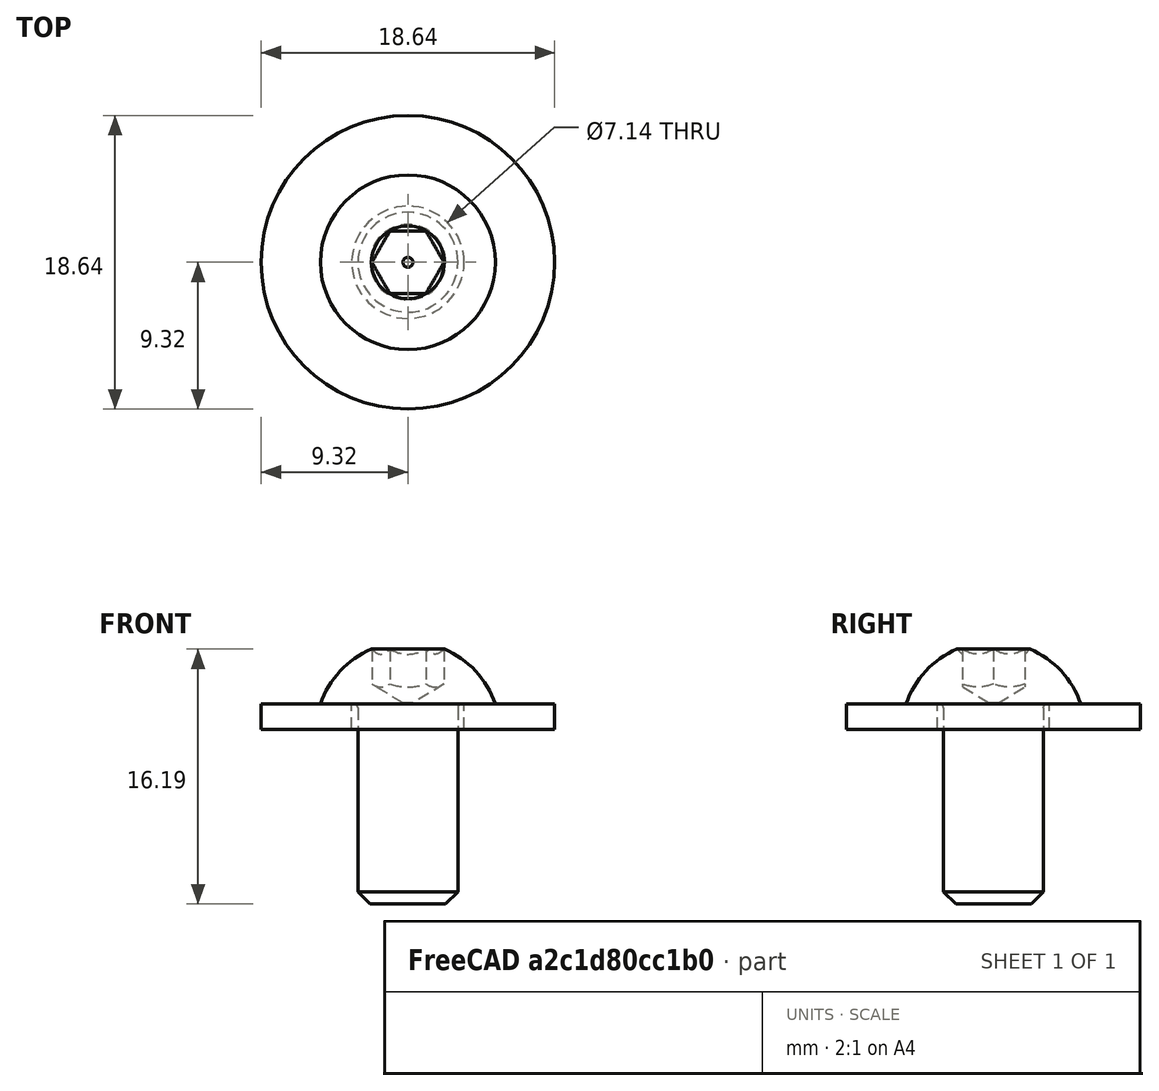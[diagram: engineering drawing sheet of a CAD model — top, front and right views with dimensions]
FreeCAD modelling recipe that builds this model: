
FCSTD DOCUMENT  (FreeCAD 2021.717R24301 +3842 (Git))
Label: X-axis
License: Creative Commons Attribution
LicenseURL: http://creativecommons.org/licenses/by/4.0/
objects: App::FeaturePython×78, Part::FeaturePython×72, App::Link×20, App::LinkElement×4, App::DocumentObjectGroup×1
note: 69 computed .brp shape members not serialized (recipe doc carries the construction recipe); baked Part::Feature solids carry a one-line shape summary decoded from their .brp
EXTERNAL_REF file=parts/HGR20.FCStd obj=Assembly001
EXTERNAL_REF file=parts/X axis plates.FCStd obj=Assembly001
EXTERNAL_REF file=parts/X axis plates.FCStd obj=Assembly
EXTERNAL_REF file=parts/Ballscrew.FCStd obj=Assembly003
EXTERNAL_REF file=parts/NEMA23-76.FCStd obj=Assembly001
EXTERNAL_REF file=parts/NEMA23-76.FCStd obj=Assembly
EXTERNAL_REF file=parts/X axis plates.FCStd obj=Assembly003
EXTERNAL_REF file=parts/HGH20CA.FCStd obj=Assembly
EXTERNAL_REF file=parts/HGH20CA.FCStd obj=Assembly001
EXTERNAL_REF file=parts/BallNut.FCStd obj=Assembly
EXTERNAL_REF file=parts/X axis plates.FCStd obj=Assembly005
EXTERNAL_REF file=parts/Extrusion.FCStd obj=Body001
EXTERNAL_REF file=parts/LimitSensor.FCStd obj=Assembly

FEATURE [App::Link] Link  label="HGR20-600"
  AutoLinkLabel = true
  AutoPlacement = true
  LinkPlacement = pos=(-97.7,1.41e-14,25.4) rot=(0,0,1;0rad)
  LinkedObject = -> <external parts/HGR20.FCStd>#Assembly001
  Placement = pos=(-97.7,1.41e-14,25.4) rot=(0,0,1;0rad)
  SyncGroupVisibility = false
  _LinkVersion = 1
FEATURE [App::Link] Link002  label="Top beam"
  AutoLinkLabel = true
  AutoPlacement = true
  LinkedObject = -> Assembly
  SyncGroupVisibility = false
  _LinkVersion = 1
FEATURE [App::Link] Link003  label="Bottom beam"
  AutoLinkLabel = true
  AutoPlacement = true
  LinkPlacement = pos=(-55.7,-2.274e-13,1.776e-13) rot=(0,0,-1;3.14159rad)
  LinkedObject = -> Assembly
  Placement = pos=(-55.7,-2.274e-13,1.776e-13) rot=(0,0,-1;3.14159rad)
  SyncGroupVisibility = false
  _LinkVersion = 1
FEATURE [App::Link] Link004  label="Left plate"
  AutoLinkLabel = true
  AutoPlacement = true
  LinkPlacement = pos=(166.3,-323.85,58.6) rot=(0,1,0;4.71239rad)
  LinkedObject = -> <external parts/X axis plates.FCStd>#Assembly001
  Placement = pos=(166.3,-323.85,58.6) rot=(0,1,0;4.71239rad)
  SyncGroupVisibility = false
  _LinkVersion = 1
FEATURE [App::Link] Link005  label="Right plate"
  AutoLinkLabel = true
  AutoPlacement = true
  LinkPlacement = pos=(166.3,69.85,58.6) rot=(0,1,0;4.71239rad)
  LinkedObject = -> <external parts/X axis plates.FCStd>#Assembly
  Placement = pos=(166.3,69.85,58.6) rot=(0,1,0;4.71239rad)
  SyncGroupVisibility = false
  _LinkVersion = 1
FEATURE [App::Link] Link006  label="Ballscrew-600"
  AutoLinkLabel = true
  AutoPlacement = true
  LinkPlacement = pos=(-27.85,251.9,-6.35) rot=(0,0,-1;3.14159rad)
  LinkedObject = -> <external parts/Ballscrew.FCStd>#Assembly003
  Placement = pos=(-27.85,251.9,-6.35) rot=(0,0,-1;3.14159rad)
  SyncGroupVisibility = false
  _LinkVersion = 1
FEATURE [App::Link] Link007  label="Coupling"
  AutoLinkLabel = true
  AutoPlacement = true
  LinkPlacement = pos=(-27.85,-296.25,18.65) rot=(-0.57735,-0.57735,-0.57735;2.0944rad)
  LinkedObject = -> <external parts/NEMA23-76.FCStd>#Assembly001
  Placement = pos=(-27.85,-296.25,18.65) rot=(-0.57735,-0.57735,-0.57735;2.0944rad)
  SyncGroupVisibility = false
  _LinkVersion = 1
FEATURE [App::Link] Link008  label="NEMA23-76"
  AutoLinkLabel = true
  AutoPlacement = true
  LinkPlacement = pos=(-27.85,-323.85,18.65) rot=(0.57735,-0.57735,0.57735;2.0944rad)
  LinkedObject = -> <external parts/NEMA23-76.FCStd>#Assembly
  Placement = pos=(-27.85,-323.85,18.65) rot=(0.57735,-0.57735,0.57735;2.0944rad)
  SyncGroupVisibility = false
  _LinkVersion = 1
FEATURE [App::Link] Link009  label="Rear plate"
  AutoLinkLabel = true
  AutoPlacement = true
  LinkPlacement = pos=(209.15,-76,-12.7) rot=(0,1,0;4.71239rad)
  LinkedObject = -> <external parts/X axis plates.FCStd>#Assembly003
  Placement = pos=(209.15,-76,-12.7) rot=(0,1,0;4.71239rad)
  SyncGroupVisibility = false
  _LinkVersion = 1
FEATURE [App::Link] Link012  label="HGH20CA-L-L"
  AutoLinkLabel = true
  AutoPlacement = true
  LinkPlacement = pos=(166.3,-274.8,202.6) rot=(-1,0,0;4.71239rad)
  LinkedObject = -> <external parts/HGH20CA.FCStd>#Assembly
  Placement = pos=(166.3,-274.8,202.6) rot=(-1,0,0;4.71239rad)
  SyncGroupVisibility = false
  _LinkVersion = 1
FEATURE [App::Link] Link013  label="HGH20CA-L-R"
  AutoLinkLabel = true
  AutoPlacement = true
  LinkPlacement = pos=(166.3,-274.8,58.6) rot=(-1,0,0;4.71239rad)
  LinkedObject = -> <external parts/HGH20CA.FCStd>#Assembly001
  Placement = pos=(166.3,-274.8,58.6) rot=(-1,0,0;4.71239rad)
  SyncGroupVisibility = false
  _LinkVersion = 1
FEATURE [App::Link] Link014  label="HGH20CA-R-L"
  AutoLinkLabel = true
  AutoPlacement = true
  LinkPlacement = pos=(166.3,274.8,58.6) rot=(1,0,0;4.71239rad)
  LinkedObject = -> Link012
  Placement = pos=(166.3,274.8,58.6) rot=(1,0,0;4.71239rad)
  SyncGroupVisibility = false
  _LinkVersion = 1
FEATURE [App::Link] Link015  label="HGH20CA-R-R"
  AutoLinkLabel = true
  AutoPlacement = true
  LinkPlacement = pos=(166.3,274.8,202.6) rot=(1,0,0;4.71239rad)
  LinkedObject = -> Link013
  Placement = pos=(166.3,274.8,202.6) rot=(1,0,0;4.71239rad)
  SyncGroupVisibility = false
  _LinkVersion = 1
FEATURE [App::Link] Link020  label="Left nut"
  AutoLinkLabel = true
  AutoPlacement = true
  LinkPlacement = pos=(219.3,-305.675,131.475) rot=(0,0.707107,0.707107;3.14159rad)
  LinkedObject = -> <external parts/BallNut.FCStd>#Assembly
  Placement = pos=(219.3,-305.675,131.475) rot=(0,0.707107,0.707107;3.14159rad)
  SyncGroupVisibility = false
  _LinkVersion = 1
FEATURE [App::Link] Link021  label="Right nut"
  AutoLinkLabel = true
  AutoPlacement = true
  LinkPlacement = pos=(219.3,305.675,131.475) rot=(1,0,0;1.5708rad)
  LinkedObject = -> <external parts/BallNut.FCStd>#Assembly
  Placement = pos=(219.3,305.675,131.475) rot=(1,0,0;1.5708rad)
  SyncGroupVisibility = false
  _LinkVersion = 1
FEATURE [App::Link] Link022  label="Gouverner left"
  AutoLinkLabel = true
  AutoPlacement = true
  LinkPlacement = pos=(166.3,-323.85,130.6) rot=(0,1,0;4.71239rad)
  LinkedObject = -> <external parts/X axis plates.FCStd>#Assembly005
  Placement = pos=(166.3,-323.85,130.6) rot=(0,1,0;4.71239rad)
  SyncGroupVisibility = false
  _LinkVersion = 1
FEATURE [App::Link] Link023  label="Gouverner right"
  AutoLinkLabel = true
  AutoPlacement = true
  LinkPlacement = pos=(166.3,323.85,130.6) rot=(0.707107,0,-0.707107;3.14159rad)
  LinkedObject = -> <external parts/X axis plates.FCStd>#Assembly005
  Placement = pos=(166.3,323.85,130.6) rot=(0.707107,0,-0.707107;3.14159rad)
  SyncGroupVisibility = false
  _LinkVersion = 1
FEATURE [App::Link] Link024  label="Extrusion"
  AutoLinkLabel = true
  AutoPlacement = true
  LinkPlacement = pos=(-85,0,0) rot=(0,0,1;0rad)
  LinkedObject = -> <external parts/Extrusion.FCStd>#Body001
  Placement = pos=(-85,0,0) rot=(0,0,1;0rad)
  SyncGroupVisibility = false
  _LinkVersion = 1
FEATURE [Part::FeaturePython] Washer  label="1/4in-Washer"  # Fasteners workbench fastener (typed FeaturePython)
  Placement = pos=(0,0,-1.6002) rot=(0,0,1;0rad)
  diameter = 11
  invert = false
  matchOuter = false
  offset = 0
  type = 1
FEATURE [Part::FeaturePython] Screw  label="1/4inx1/2in-Screw"  # Fasteners workbench fastener (typed FeaturePython)
  diameter = 11
  invert = false
  length = 4
  lengthCustom = 12.7
  matchOuter = false
  offset = 0
  thread = false
  type = 4
FEATURE [Part::FeaturePython] Parts002  # WARN: FeaturePython — macro-defined, semantics opaque (R4)
  Group = -> [Washer,Screw]
  GroupMode = 0
  _LinkVersion = 1
FEATURE [App::LinkElement] Link025_i0
  LinkPlacement = pos=(-63.4102,-234.8,-12.7) rot=(-0.57735,-0.57735,0.57735;2.0944rad)
  LinkedObject = -> Assembly002
  Placement = pos=(-63.4102,-234.8,-12.7) rot=(-0.57735,-0.57735,0.57735;2.0944rad)
  _LinkVersion = 1
FEATURE [App::LinkElement] Link025_i1
  LinkPlacement = pos=(-63.4102,-78.2667,-12.7) rot=(-0.57735,-0.57735,0.57735;2.0944rad)
  LinkedObject = -> Assembly002
  Placement = pos=(-63.4102,-78.2667,-12.7) rot=(-0.57735,-0.57735,0.57735;2.0944rad)
  _LinkVersion = 1
FEATURE [App::LinkElement] Link025_i2
  LinkPlacement = pos=(-63.4102,78.2667,-12.7) rot=(-0.57735,-0.57735,0.57735;2.0944rad)
  LinkedObject = -> Assembly002
  Placement = pos=(-63.4102,78.2667,-12.7) rot=(-0.57735,-0.57735,0.57735;2.0944rad)
  _LinkVersion = 1
FEATURE [App::LinkElement] Link025_i3
  LinkPlacement = pos=(-63.4102,234.8,-12.7) rot=(-0.57735,-0.57735,0.57735;2.0944rad)
  LinkedObject = -> Assembly002
  Placement = pos=(-63.4102,234.8,-12.7) rot=(-0.57735,-0.57735,0.57735;2.0944rad)
  _LinkVersion = 1
FEATURE [App::Link] Link025  label="1/4x1/2 screw and washer Assembly 4ct"
  AutoLinkLabel = true
  AutoPlacement = true
  ElementCount = 4
  ElementList = -> [Link025_i0,Link025_i1,Link025_i2,Link025_i3]
  LinkedObject = -> Assembly002
  SyncGroupVisibility = false
  _LinkVersion = 1
FEATURE [Part::FeaturePython] Parts  # WARN: FeaturePython — macro-defined, semantics opaque (R4)
  Group = -> [Link,Link024,Link025]
  GroupMode = 0
  _LinkVersion = 1
FEATURE [App::Link] Link026  label="Limit sensor"
  AutoLinkLabel = true
  AutoPlacement = true
  LinkPlacement = pos=(-62.4,-304.8,56.1) rot=(-1,0,0;3.14159rad)
  LinkedObject = -> <external parts/LimitSensor.FCStd>#Assembly
  Placement = pos=(-62.4,-304.8,56.1) rot=(-1,0,0;3.14159rad)
  SyncGroupVisibility = false
  _LinkVersion = 1
FEATURE [Part::FeaturePython] Parts001  # WARN: FeaturePython — macro-defined, semantics opaque (R4)
  Group = -> [Link002,Link003,Link004,Link005,Link006,Link007,Link008,Link009,Link012,Link013,Link014,Link015,Link020,Link021,Link022,Link023,Link026]
  GroupMode = 0
  _LinkVersion = 1
FEATURE [Part::FeaturePython] Assembly  label="X-beam Assembly"  # WARN: FeaturePython — macro-defined, semantics opaque (R4)
  AutoRelax = true
  BuildShape = 0
  Freeze = false
  Group = -> [Constraints,Elements,Parts]
  Verbose = false
  _LinkVersion = 1
  _SolverType = 1
  _Version = 1
FEATURE [App::FeaturePython] Constraints  # WARN: FeaturePython — macro-defined, semantics opaque (R4)
  Group = -> [Constraint,Constraint001,Constraint032,Constraint033,Constraint034,Constraint035]
  _LinkVersion = 1
  _Version = 1
FEATURE [App::FeaturePython] Elements  # WARN: FeaturePython — macro-defined, semantics opaque (R4)
  Group = -> [Element,Element001,Element002,Element003,Element007,Element008,Element012,Element013,_Element002,_Element003,_Element004,_Element005,_Element006,_Element007,_Element008,_Element009]
  _LinkVersion = 1
FEATURE [Part::FeaturePython] Element  label="center-mate@HGR20-600-Assembly"  # link proxy (typed FeaturePython)
  Detach = false
  LinkTransform = true
  LinkedObject = -> Link [1.$center-mate.]
  _LinkVersion = 1
  _Parent = -> Elements
FEATURE [Part::FeaturePython] Element001  label="extrusion center"  # link proxy (typed FeaturePython)
  Detach = false
  LinkTransform = true
  LinkedObject = -> Link024 [Sketch001.]
  _LinkVersion = 1
  _Parent = -> Elements
FEATURE [App::FeaturePython] Constraint  label="Locked"  # WARN: FeaturePython — macro-defined, semantics opaque (R4)
  Disabled = false
  Group = -> [ElementLink]
  _ConstraintType = 0
  _LinkVersion = 1
  _Parent = -> Constraints
FEATURE [App::FeaturePython] ElementLink  label="extrusion center"  # link proxy (typed FeaturePython)
  LinkTransform = true
  LinkedObject = -> Element001
  _LinkVersion = 1
  _Parent = -> Constraint
FEATURE [App::FeaturePython] Constraint001  label="Attachment"  # WARN: FeaturePython — macro-defined, semantics opaque (R4)
  Cascade = false
  Disabled = false
  Group = -> [ElementLink001,ElementLink002]
  Multiply = false
  _ConstraintType = 45
  _LinkVersion = 1
  _Parent = -> Constraints
FEATURE [App::FeaturePython] ElementLink001  label="extrusion center"  # link proxy (typed FeaturePython)
  LinkTransform = true
  LinkedObject = -> Element001
  _LinkVersion = 1
  _Parent = -> Constraint001
FEATURE [App::FeaturePython] ElementLink002  label="center-mate@HGR20-600-Assembly"  # link proxy (typed FeaturePython)
  LinkTransform = true
  LinkedObject = -> Element
  Offset = pos=(0,0,0) rot=(1,0,0;3.14159rad)
  Placement = pos=(1.42e-14,3.13e-14,50.8) rot=(1,0,0;3.14159rad)
  _LinkVersion = 1
  _Parent = -> Constraint001
FEATURE [Part::FeaturePython] Element002  label="top-cart-mate"  # link proxy (typed FeaturePython)
  Detach = false
  LinkTransform = true
  LinkedObject = -> Link [1.$top-mate.]
  _LinkVersion = 1
  _Parent = -> Elements
FEATURE [Part::FeaturePython] Element003  label="side-cart-mate"  # link proxy (typed FeaturePython)
  Detach = false
  LinkTransform = true
  LinkedObject = -> Link [1.$side-mate.]
  _LinkVersion = 1
  _Parent = -> Elements
FEATURE [Part::FeaturePython] Assembly001  label="X-axis Assembly"  # WARN: FeaturePython — macro-defined, semantics opaque (R4)
  AutoRelax = true
  BuildShape = 0
  Freeze = false
  Group = -> [Constraints001,Elements001,Parts001]
  Placement = pos=(79.15,3.69183,42.8418) rot=(-0.57735,-0.57735,0.57735;4.18879rad)
  Verbose = false
  _LinkVersion = 1
  _SolverType = 1
  _Version = 1
FEATURE [App::FeaturePython] Constraints001  # WARN: FeaturePython — macro-defined, semantics opaque (R4)
  Group = -> [Constraint002,Constraint003,Constraint004,Constraint005,Constraint011,Constraint012,Constraint013,Constraint021,Constraint022,Constraint023,Constraint024,Constraint025,Constraint026,Constraint027,Constraint028,Constraint029,Constraint036]
  _LinkVersion = 1
  _Version = 1
FEATURE [App::FeaturePython] Elements001  # WARN: FeaturePython — macro-defined, semantics opaque (R4)
  Group = -> [Element004,Element005,Element006,Element009,Element010,Element011,Element014,Element015,Element016,Element017,Element018,Element019,Element020,Element021,Element022,Element023,Element024,Element025,Element026,Element027,Element028,Element030,Element031,Element034,Element036,Element038,Element040,Element046,Element047,Element048,Element049,Element054,Element055,Element056,Element057,Element058,+9 more]
  _LinkVersion = 1
FEATURE [Part::FeaturePython] Element004  label="top-cart-mate@X-beam Assembly"  # link proxy (typed FeaturePython)
  Detach = false
  LinkTransform = true
  LinkedObject = -> Link002 [1.$top-cart-mate.]
  _LinkVersion = 1
  _Parent = -> Elements001
FEATURE [Part::FeaturePython] Element005  label="side-cart-mate@X-beam Assembly"  # link proxy (typed FeaturePython)
  Detach = false
  LinkTransform = true
  LinkedObject = -> Link002 [1.$side-cart-mate.]
  _LinkVersion = 1
  _Parent = -> Elements001
FEATURE [Part::FeaturePython] Element006  label="extrusion center@X-beam Assembly"  # link proxy (typed FeaturePython)
  Detach = false
  LinkTransform = true
  LinkedObject = -> Link002 [1.$extrusion center.]
  _LinkVersion = 1
  _Parent = -> Elements001
FEATURE [App::FeaturePython] Constraint002  label="Locked001"  # WARN: FeaturePython — macro-defined, semantics opaque (R4)
  Disabled = false
  Group = -> [ElementLink003]
  _ConstraintType = 0
  _LinkVersion = 1
  _Parent = -> Constraints001
FEATURE [App::FeaturePython] ElementLink003  label="extrusion center@X-beam Assembly"  # link proxy (typed FeaturePython)
  LinkTransform = true
  LinkedObject = -> Element006
  _LinkVersion = 1
  _Parent = -> Constraint002
FEATURE [Part::FeaturePython] Element007  label="left-point@HGR20-600-Assembly"  # link proxy (typed FeaturePython)
  Detach = false
  LinkTransform = true
  LinkedObject = -> Link [1.$left-point.]
  _LinkVersion = 1
  _Parent = -> Elements
FEATURE [Part::FeaturePython] Element008  label="right-point@HGR20-600-Assembly"  # link proxy (typed FeaturePython)
  Detach = false
  LinkTransform = true
  LinkedObject = -> Link [1.$right-point.]
  _LinkVersion = 1
  _Parent = -> Elements
FEATURE [Part::FeaturePython] Element009  label="left-point@X-beam Assembly"  # link proxy (typed FeaturePython)
  Detach = false
  LinkTransform = true
  LinkedObject = -> Link002 [1.$left-point@HGR20-600-Assembly.]
  _LinkVersion = 1
  _Parent = -> Elements001
FEATURE [Part::FeaturePython] Element010  label="right-point@X-beam Assembly"  # link proxy (typed FeaturePython)
  Detach = false
  LinkTransform = true
  LinkedObject = -> Link003 [1.$right-point@HGR20-600-Assembly.]
  _LinkVersion = 1
  _Parent = -> Elements001
FEATURE [Part::FeaturePython] Element011  label="side-cart-mate@X-beam Assembly001"  # link proxy (typed FeaturePython)
  Detach = false
  LinkTransform = true
  LinkedObject = -> Link003 [1.$side-cart-mate.]
  _LinkVersion = 1
  _Parent = -> Elements001
FEATURE [Part::FeaturePython] Element012  label="plate-mate-1"  # link proxy (typed FeaturePython)
  Detach = false
  LinkTransform = true
  LinkedObject = -> Link024 [Pocket004.Edge345]
  _LinkVersion = 1
  _Parent = -> Elements
FEATURE [Part::FeaturePython] Element013  label="plate-mate-2"  # link proxy (typed FeaturePython)
  Detach = false
  LinkTransform = true
  LinkedObject = -> Link024 [Pocket004.Edge176]
  _LinkVersion = 1
  _Parent = -> Elements
FEATURE [Part::FeaturePython] Element014  label="plate-mate-tl@X-beam Assembly"  # link proxy (typed FeaturePython)
  Detach = false
  LinkTransform = true
  LinkedObject = -> Link002 [1.$plate-mate-1.]
  _LinkVersion = 1
  _Parent = -> Elements001
FEATURE [Part::FeaturePython] Element015  label="plate-mate-tr@X-beam Assembly"  # link proxy (typed FeaturePython)
  Detach = false
  LinkTransform = true
  LinkedObject = -> Link002 [1.$plate-mate-2.]
  _LinkVersion = 1
  _Parent = -> Elements001
FEATURE [Part::FeaturePython] Element016  label="plate-mate-br@X-beam Assembly"  # link proxy (typed FeaturePython)
  Detach = false
  LinkTransform = true
  LinkedObject = -> Link003 [1.$plate-mate-1.]
  _LinkVersion = 1
  _Parent = -> Elements001
FEATURE [Part::FeaturePython] Element017  label="plate-mate-bl@X-beam Assembly"  # link proxy (typed FeaturePython)
  Detach = false
  LinkTransform = true
  LinkedObject = -> Link003 [1.$plate-mate-2.]
  _LinkVersion = 1
  _Parent = -> Elements001
FEATURE [Part::FeaturePython] Element018  label="bottom-beam-mate@Left plate Assembly"  # link proxy (typed FeaturePython)
  Detach = false
  LinkTransform = true
  LinkedObject = -> Link004 [1.$bottom-beam-mate.]
  _LinkVersion = 1
  _Parent = -> Elements001
FEATURE [Part::FeaturePython] Element019  label="top-beam-mate@Left plate Assembly"  # link proxy (typed FeaturePython)
  Detach = false
  LinkTransform = true
  LinkedObject = -> Link004 [1.$top-beam-mate.]
  _LinkVersion = 1
  _Parent = -> Elements001
FEATURE [Part::FeaturePython] Element020  label="top-beam-mate@Right plate Assembly"  # link proxy (typed FeaturePython)
  Detach = false
  LinkTransform = true
  LinkedObject = -> Link005 [1.$top-beam-mate.]
  _LinkVersion = 1
  _Parent = -> Elements001
FEATURE [App::FeaturePython] Constraint003  label="Attachment-beam-tr"  # WARN: FeaturePython — macro-defined, semantics opaque (R4)
  Cascade = false
  Disabled = false
  Group = -> [ElementLink004,ElementLink005]
  Multiply = false
  _ConstraintType = 45
  _LinkVersion = 1
  _Parent = -> Constraints001
FEATURE [App::FeaturePython] ElementLink004  label="_top-beam-mate@Right plate Assembly"  # link proxy (typed FeaturePython)
  LinkTransform = true
  LinkedObject = -> _Element010
  _LinkVersion = 1
  _Parent = -> Constraint003
FEATURE [App::FeaturePython] ElementLink005  label="plate-mate-tr@X-beam Assembly"  # link proxy (typed FeaturePython)
  LinkTransform = true
  LinkedObject = -> Element015
  Offset = pos=(0,0,0) rot=(0,0,1;1.5708rad)
  Placement = pos=(-110.4,0,85) rot=(0,-1,0;1.5708rad)
  _LinkVersion = 1
  _Parent = -> Constraint003
FEATURE [App::FeaturePython] Constraint004  label="Attachment-beam-tl"  # WARN: FeaturePython — macro-defined, semantics opaque (R4)
  Cascade = false
  Disabled = false
  Group = -> [ElementLink006,ElementLink007]
  Multiply = false
  _ConstraintType = 45
  _LinkVersion = 1
  _Parent = -> Constraints001
FEATURE [App::FeaturePython] ElementLink006  label="top-beam-mate@Left plate Assembly"  # link proxy (typed FeaturePython)
  LinkTransform = true
  LinkedObject = -> Element019
  _LinkVersion = 1
  _Parent = -> Constraint004
FEATURE [App::FeaturePython] ElementLink007  label="plate-mate-tl@X-beam Assembly"  # link proxy (typed FeaturePython)
  LinkTransform = true
  LinkedObject = -> Element014
  Offset = pos=(0,0,0) rot=(0,0,1;1.5708rad)
  Placement = pos=(-110.4,0,85) rot=(0,-1,0;1.5708rad)
  _LinkVersion = 1
  _Parent = -> Constraint004
FEATURE [App::FeaturePython] Constraint005  label="Attachment-beam-bl"  # WARN: FeaturePython — macro-defined, semantics opaque (R4)
  Cascade = false
  Disabled = false
  Group = -> [ElementLink008,ElementLink009]
  Multiply = false
  _ConstraintType = 45
  _LinkVersion = 1
  _Parent = -> Constraints001
FEATURE [App::FeaturePython] ElementLink008  label="bottom-beam-mate@Left plate Assembly"  # link proxy (typed FeaturePython)
  LinkTransform = true
  LinkedObject = -> Element018
  Offset = pos=(0,0,0) rot=(0,0,1;1.5708rad)
  Placement = pos=(29.3,0,-54.7) rot=(0,-1,0;1.5708rad)
  _LinkVersion = 1
  _Parent = -> Constraint005
FEATURE [App::FeaturePython] ElementLink009  label="plate-mate-bl@X-beam Assembly"  # link proxy (typed FeaturePython)
  LinkTransform = true
  LinkedObject = -> Element017
  Offset = pos=(0,0,0) rot=(1,0,0;3.14159rad)
  Placement = pos=(-8.53e-14,-609.6,-25.4) rot=(1,0,0;3.14159rad)
  _LinkVersion = 1
  _Parent = -> Constraint005
FEATURE [Part::FeaturePython] Element021  label="screw-mate@Coupling-Assembly"  # link proxy (typed FeaturePython)
  Detach = false
  LinkTransform = true
  LinkedObject = -> Link007 [1.$screw-mate.]
  _LinkVersion = 1
  _Parent = -> Elements001
FEATURE [Part::FeaturePython] Element022  label="coupling-mate@Ballscrew-600-Assembly"  # link proxy (typed FeaturePython)
  Detach = false
  LinkTransform = true
  LinkedObject = -> Link006 [1.$coupling-mate.]
  _LinkVersion = 1
  _Parent = -> Elements001
FEATURE [Part::FeaturePython] Element023  label="motor-mate@Coupling-Assembly"  # link proxy (typed FeaturePython)
  Detach = false
  LinkTransform = true
  LinkedObject = -> Link007 [1.$motor-mate.]
  _LinkVersion = 1
  _Parent = -> Elements001
FEATURE [Part::FeaturePython] Element024  label="coupling-mate@NEMA23-76-Assembly"  # link proxy (typed FeaturePython)
  Detach = false
  LinkTransform = true
  LinkedObject = -> Link008 [1.$coupling-mate.]
  _LinkVersion = 1
  _Parent = -> Elements001
FEATURE [Part::FeaturePython] Element025  label="plate-mate@NEMA23-76-Assembly"  # link proxy (typed FeaturePython)
  Detach = false
  LinkTransform = true
  LinkedObject = -> Link008 [1.$bracket-mate.]
  _LinkVersion = 1
  _Parent = -> Elements001
FEATURE [Part::FeaturePython] Element026  label="motor-mate@Left plate Assembly"  # link proxy (typed FeaturePython)
  Detach = false
  LinkTransform = true
  LinkedObject = -> Link004 [1.$motor-mate.]
  _LinkVersion = 1
  _Parent = -> Elements001
FEATURE [Part::FeaturePython] Element027  label="bf-base@Ballscrew-600-Assembly"  # link proxy (typed FeaturePython)
  Detach = false
  LinkTransform = true
  LinkedObject = -> Link006 [1.$bf-base.]
  _LinkVersion = 1
  _Parent = -> Elements001
FEATURE [App::FeaturePython] Constraint011  label="Attachment-motor-coupling"  # WARN: FeaturePython — macro-defined, semantics opaque (R4)
  Cascade = false
  Disabled = false
  Group = -> [ElementLink019,ElementLink020]
  Multiply = false
  _ConstraintType = 45
  _LinkVersion = 1
  _Parent = -> Constraints001
FEATURE [App::FeaturePython] ElementLink019  label="coupling-mate@NEMA23-76-Assembly"  # link proxy (typed FeaturePython)
  LinkTransform = true
  LinkedObject = -> Element024
  _LinkVersion = 1
  _Parent = -> Constraint011
FEATURE [App::FeaturePython] ElementLink020  label="motor-mate@Coupling-Assembly"  # link proxy (typed FeaturePython)
  LinkTransform = true
  LinkedObject = -> Element023
  _LinkVersion = 1
  _Parent = -> Constraint011
FEATURE [App::FeaturePython] Constraint012  label="Attachment-screw-coupling"  # WARN: FeaturePython — macro-defined, semantics opaque (R4)
  Cascade = false
  Disabled = false
  Group = -> [ElementLink021,ElementLink022]
  Multiply = false
  _ConstraintType = 45
  _LinkVersion = 1
  _Parent = -> Constraints001
FEATURE [App::FeaturePython] ElementLink021  label="coupling-mate@Ballscrew-600-Assembly"  # link proxy (typed FeaturePython)
  LinkTransform = true
  LinkedObject = -> Element022
  Offset = pos=(0,0,0) rot=(1,0,0;3.14159rad)
  Placement = pos=(1.51559e-11,-582.5,37.3) rot=(1,0,0;3.14159rad)
  _LinkVersion = 1
  _Parent = -> Constraint012
FEATURE [App::FeaturePython] ElementLink022  label="screw-mate@Coupling-Assembly"  # link proxy (typed FeaturePython)
  LinkTransform = true
  LinkedObject = -> Element021
  Offset = pos=(0,0,0) rot=(0,0,1;4.71239rad)
  Placement = pos=(-9.2,1.53936e-08,46.5) rot=(0,-1,0;1.5708rad)
  _LinkVersion = 1
  _Parent = -> Constraint012
FEATURE [Part::FeaturePython] Element028  label="side-mate@Rear plate left Assembly"  # link proxy (typed FeaturePython)
  Detach = false
  LinkTransform = true
  LinkedObject = -> Link009 [1.$side-mate-L.]
  _LinkVersion = 1
  _Parent = -> Elements001
FEATURE [Part::FeaturePython] Element030  label="rear-mate@Left plate Assembly"  # link proxy (typed FeaturePython)
  Detach = false
  LinkTransform = true
  LinkedObject = -> Link004 [1.$rear-mate.]
  _LinkVersion = 1
  _Parent = -> Elements001
FEATURE [Part::FeaturePython] Element031  label="rear-mate@Right plate Assembly"  # link proxy (typed FeaturePython)
  Detach = false
  LinkTransform = true
  LinkedObject = -> Link005 [1.$rear-mate.]
  _LinkVersion = 1
  _Parent = -> Elements001
FEATURE [App::FeaturePython] Constraint013  label="Attachment-left-rear"  # WARN: FeaturePython — macro-defined, semantics opaque (R4)
  Cascade = false
  Disabled = false
  Group = -> [ElementLink023,ElementLink024]
  Multiply = false
  _ConstraintType = 45
  _LinkVersion = 1
  _Parent = -> Constraints001
FEATURE [App::FeaturePython] ElementLink023  label="rear-mate@Left plate Assembly"  # link proxy (typed FeaturePython)
  LinkTransform = true
  LinkedObject = -> Element030
  Offset = pos=(0,0,0) rot=(1,0,0;3.14159rad)
  Placement = pos=(-55.7,-609.6,-1.634e-13) rot=(0,0,1;3.14159rad)
  _LinkVersion = 1
  _Parent = -> Constraint013
FEATURE [App::FeaturePython] ElementLink024  label="side-mate@Rear plate left Assembly"  # link proxy (typed FeaturePython)
  LinkTransform = true
  LinkedObject = -> Element028
  Offset = pos=(0,0,0) rot=(0,0,1;1.5708rad)
  Placement = pos=(-40.55,5.68e-14,15.15) rot=(0,-1,0;1.5708rad)
  _LinkVersion = 1
  _Parent = -> Constraint013
FEATURE [Part::FeaturePython] Element034  label="shim-L-L@HGH20CA-L-Assembly"  # link proxy (typed FeaturePython)
  Detach = false
  LinkTransform = true
  LinkedObject = -> Link012 [1.$shim-tr.]
  _LinkVersion = 1
  _Parent = -> Elements001
FEATURE [Part::FeaturePython] Element036  label="shim-L-R@HGH20CA-R-Assembly"  # link proxy (typed FeaturePython)
  Detach = false
  LinkTransform = true
  LinkedObject = -> Link013 [1.$shim-br.]
  _LinkVersion = 1
  _Parent = -> Elements001
FEATURE [Part::FeaturePython] Element038  label="shim-R-L@HGH20CA-L-Assembly"  # link proxy (typed FeaturePython)
  Detach = false
  LinkTransform = true
  LinkedObject = -> Link014 [1.$shim-tr.]
  _LinkVersion = 1
  _Parent = -> Elements001
FEATURE [Part::FeaturePython] Element040  label="shim-R-R@HGH20CA-R-Assembly"  # link proxy (typed FeaturePython)
  Detach = false
  LinkTransform = true
  LinkedObject = -> Link015 [1.$shim-br.]
  _LinkVersion = 1
  _Parent = -> Elements001
FEATURE [Part::FeaturePython] Element046  label="shim-R-L@Right plate Assembly"  # link proxy (typed FeaturePython)
  Detach = false
  LinkTransform = true
  LinkedObject = -> Link005 [1.$cart-L.]
  _LinkVersion = 1
  _Parent = -> Elements001
FEATURE [Part::FeaturePython] Element047  label="shim-R-R@Right plate Assembly"  # link proxy (typed FeaturePython)
  Detach = false
  LinkTransform = true
  LinkedObject = -> Link005 [1.$cart-R.]
  _LinkVersion = 1
  _Parent = -> Elements001
FEATURE [Part::FeaturePython] Element048  label="shim-L-L@Left plate Assembly"  # link proxy (typed FeaturePython)
  Detach = false
  LinkTransform = true
  LinkedObject = -> Link004 [1.$cart-L.]
  _LinkVersion = 1
  _Parent = -> Elements001
FEATURE [Part::FeaturePython] Element049  label="shim-L-R@Left plate Assembly"  # link proxy (typed FeaturePython)
  Detach = false
  LinkTransform = true
  LinkedObject = -> Link004 [1.$cart-R.]
  _LinkVersion = 1
  _Parent = -> Elements001
FEATURE [App::FeaturePython] Constraint021  label="Attachment-cart-R-R"  # WARN: FeaturePython — macro-defined, semantics opaque (R4)
  Cascade = false
  Disabled = false
  Group = -> [ElementLink039,ElementLink040]
  Multiply = false
  _ConstraintType = 45
  _LinkVersion = 1
  _Parent = -> Constraints001
FEATURE [App::FeaturePython] ElementLink039  label="shim-R-R@Right plate Assembly"  # link proxy (typed FeaturePython)
  LinkTransform = true
  LinkedObject = -> Element047
  Offset = pos=(0,0,0) rot=(1,0,0;3.14159rad)
  Placement = pos=(364.6,609.6,2.274e-13) rot=(0,0,1;3.14159rad)
  _LinkVersion = 1
  _Parent = -> Constraint021
FEATURE [App::FeaturePython] ElementLink040  label="shim-R-R@HGH20CA-R-Assembly"  # link proxy (typed FeaturePython)
  LinkTransform = true
  LinkedObject = -> Element040
  Offset = pos=(0,0,0) rot=(0,0,1;1.5708rad)
  Placement = pos=(-38.3,1.705e-13,402.9) rot=(0,1,0;1.5708rad)
  _LinkVersion = 1
  _Parent = -> Constraint021
FEATURE [App::FeaturePython] Constraint022  label="Attachment-cart-R-L"  # WARN: FeaturePython — macro-defined, semantics opaque (R4)
  Cascade = false
  Disabled = false
  Group = -> [ElementLink041,ElementLink042]
  Multiply = false
  _ConstraintType = 45
  _LinkVersion = 1
  _Parent = -> Constraints001
FEATURE [App::FeaturePython] ElementLink041  label="shim-R-L@Right plate Assembly"  # link proxy (typed FeaturePython)
  LinkTransform = true
  LinkedObject = -> Element046
  Offset = pos=(0,0,0) rot=(1,0,0;3.14159rad)
  Placement = pos=(364.6,609.6,2.274e-13) rot=(0,0,1;3.14159rad)
  _LinkVersion = 1
  _Parent = -> Constraint022
FEATURE [App::FeaturePython] ElementLink042  label="shim-R-L@HGH20CA-L-Assembly"  # link proxy (typed FeaturePython)
  LinkTransform = true
  LinkedObject = -> Element038
  Offset = pos=(0,0,0) rot=(0,0,1;1.5708rad)
  Placement = pos=(141.7,5.68e-14,222.9) rot=(0,1,0;1.5708rad)
  _LinkVersion = 1
  _Parent = -> Constraint022
FEATURE [App::FeaturePython] Constraint023  label="Attachment-cart-L-R"  # WARN: FeaturePython — macro-defined, semantics opaque (R4)
  Cascade = false
  Disabled = false
  Group = -> [ElementLink043,ElementLink044]
  Multiply = false
  _ConstraintType = 45
  _LinkVersion = 1
  _Parent = -> Constraints001
FEATURE [App::FeaturePython] ElementLink043  label="shim-L-R@Left plate Assembly"  # link proxy (typed FeaturePython)
  LinkTransform = true
  LinkedObject = -> Element049
  Placement = pos=(1.137e-13,0,-7.1e-15) rot=(0,0,1;0rad)
  _LinkVersion = 1
  _Parent = -> Constraint023
FEATURE [App::FeaturePython] ElementLink044  label="shim-L-R@HGH20CA-R-Assembly"  # link proxy (typed FeaturePython)
  LinkTransform = true
  LinkedObject = -> Element036
  Offset = pos=(0,0,0) rot=(0,0,1;4.71239rad)
  Placement = pos=(141.7,5.68e-14,222.9) rot=(0,1,0;1.5708rad)
  _LinkVersion = 1
  _Parent = -> Constraint023
FEATURE [App::FeaturePython] Constraint024  label="Attachment-cart-L-L"  # WARN: FeaturePython — macro-defined, semantics opaque (R4)
  Cascade = false
  Disabled = false
  Group = -> [ElementLink045,ElementLink046]
  Multiply = false
  _ConstraintType = 45
  _LinkVersion = 1
  _Parent = -> Constraints001
FEATURE [App::FeaturePython] ElementLink045  label="shim-L-L@HGH20CA-L-Assembly"  # link proxy (typed FeaturePython)
  LinkTransform = true
  LinkedObject = -> Element034
  Offset = pos=(0,0,0) rot=(0,0,1;3.14159rad)
  Placement = pos=(364.6,-4.547e-13,441.2) rot=(0,1,0;3.14159rad)
  _LinkVersion = 1
  _Parent = -> Constraint024
FEATURE [App::FeaturePython] ElementLink046  label="shim-L-L@Left plate Assembly"  # link proxy (typed FeaturePython)
  LinkTransform = true
  LinkedObject = -> Element048
  Offset = pos=(0,0,0) rot=(0,0,1;4.71239rad)
  Placement = pos=(-38.3,-5.68e-14,402.9) rot=(0,1,0;1.5708rad)
  _LinkVersion = 1
  _Parent = -> Constraint024
FEATURE [Part::FeaturePython] Element054  label="point@HGH20CA-R-Assembly"  # link proxy (typed FeaturePython)
  Detach = false
  LinkTransform = true
  LinkedObject = -> Link015 [1.$point.]
  _LinkVersion = 1
  _Parent = -> Elements001
FEATURE [Part::FeaturePython] Element055  label="side-mate@HGH20CA-R-Assembly"  # link proxy (typed FeaturePython)
  Detach = false
  LinkTransform = true
  LinkedObject = -> Link015 [1.$side-mate.]
  _LinkVersion = 1
  _Parent = -> Elements001
FEATURE [Part::FeaturePython] Element056  label="top-mate@HGH20CA-R-Assembly"  # link proxy (typed FeaturePython)
  Detach = false
  LinkTransform = true
  LinkedObject = -> Link015 [1.$top-mate.]
  _LinkVersion = 1
  _Parent = -> Elements001
FEATURE [Part::FeaturePython] Element057  label="plate-mate@Gouverner Assembly Left"  # link proxy (typed FeaturePython)
  Detach = false
  LinkTransform = true
  LinkedObject = -> Link022 [1.$plate-mate.]
  _LinkVersion = 1
  _Parent = -> Elements001
FEATURE [Part::FeaturePython] Element058  label="nut-mate@Gouverner Assembly Left"  # link proxy (typed FeaturePython)
  Detach = false
  LinkTransform = true
  LinkedObject = -> Link022 [1.$nut-mate.]
  _LinkVersion = 1
  _Parent = -> Elements001
FEATURE [Part::FeaturePython] Element059  label="plate-mate@Gouverner Assembly Right"  # link proxy (typed FeaturePython)
  Detach = false
  LinkTransform = true
  LinkedObject = -> Link023 [1.$plate-mate.]
  _LinkVersion = 1
  _Parent = -> Elements001
FEATURE [Part::FeaturePython] Element060  label="nut-mate@Gouverner Assembly Right"  # link proxy (typed FeaturePython)
  Detach = false
  LinkTransform = true
  LinkedObject = -> Link023 [1.$nut-mate.]
  _LinkVersion = 1
  _Parent = -> Elements001
FEATURE [Part::FeaturePython] Element061  label="gov-mate@Left plate Assembly"  # link proxy (typed FeaturePython)
  Detach = false
  LinkTransform = true
  LinkedObject = -> Link004 [1.$gov-mate.]
  _LinkVersion = 1
  _Parent = -> Elements001
FEATURE [Part::FeaturePython] Element062  label="gov-mate@Right plate Assembly"  # link proxy (typed FeaturePython)
  Detach = false
  LinkTransform = true
  LinkedObject = -> Link005 [1.$gov-mate.]
  _LinkVersion = 1
  _Parent = -> Elements001
FEATURE [App::FeaturePython] Constraint025  label="Attachment-governer-left"  # WARN: FeaturePython — macro-defined, semantics opaque (R4)
  Cascade = false
  Disabled = false
  Group = -> [ElementLink047,ElementLink048]
  Multiply = false
  _ConstraintType = 45
  _LinkVersion = 1
  _Parent = -> Constraints001
FEATURE [App::FeaturePython] ElementLink047  label="gov-mate@Left plate Assembly"  # link proxy (typed FeaturePython)
  LinkTransform = true
  LinkedObject = -> Element061
  _LinkVersion = 1
  _Parent = -> Constraint025
FEATURE [App::FeaturePython] ElementLink048  label="plate-mate@Gouverner Assembly Left"  # link proxy (typed FeaturePython)
  LinkTransform = true
  LinkedObject = -> Element057
  _LinkVersion = 1
  _Parent = -> Constraint025
FEATURE [App::FeaturePython] Constraint026  label="Attachment-governer-right"  # WARN: FeaturePython — macro-defined, semantics opaque (R4)
  Cascade = false
  Disabled = false
  Group = -> [ElementLink049,ElementLink050]
  Multiply = false
  _ConstraintType = 45
  _LinkVersion = 1
  _Parent = -> Constraints001
FEATURE [App::FeaturePython] ElementLink049  label="gov-mate@Right plate Assembly"  # link proxy (typed FeaturePython)
  LinkTransform = true
  LinkedObject = -> Element062
  _LinkVersion = 1
  _Parent = -> Constraint026
FEATURE [App::FeaturePython] ElementLink050  label="plate-mate@Gouverner Assembly Right"  # link proxy (typed FeaturePython)
  LinkTransform = true
  LinkedObject = -> Element059
  _LinkVersion = 1
  _Parent = -> Constraint026
FEATURE [Part::FeaturePython] Element063  label="gov-mate@NUT Assembly"  # link proxy (typed FeaturePython)
  Detach = false
  LinkTransform = true
  LinkedObject = -> Link020 [1.$gov-mate.]
  _LinkVersion = 1
  _Parent = -> Elements001
FEATURE [App::FeaturePython] Constraint027  label="Attachment-nut-governer-left"  # WARN: FeaturePython — macro-defined, semantics opaque (R4)
  Cascade = false
  Disabled = false
  Group = -> [ElementLink051,ElementLink052]
  Multiply = false
  _ConstraintType = 45
  _LinkVersion = 1
  _Parent = -> Constraints001
FEATURE [App::FeaturePython] ElementLink051  label="gov-mate@NUT Assembly"  # link proxy (typed FeaturePython)
  LinkTransform = true
  LinkedObject = -> Element063
  _LinkVersion = 1
  _Parent = -> Constraint027
FEATURE [App::FeaturePython] ElementLink052  label="nut-mate@Gouverner Assembly Left"  # link proxy (typed FeaturePython)
  LinkTransform = true
  LinkedObject = -> Element058
  Offset = pos=(0,0,0) rot=(0,0,1;1.5708rad)
  Placement = pos=(341.9,2.274e-13,-56.7) rot=(0,-1,0;1.5708rad)
  _LinkVersion = 1
  _Parent = -> Constraint027
FEATURE [Part::FeaturePython] Element064  label="gov-mate-r@NUT Assembly"  # link proxy (typed FeaturePython)
  Detach = false
  LinkTransform = true
  LinkedObject = -> Link021 [1.$gov-mate-r.]
  _LinkVersion = 1
  _Parent = -> Elements001
FEATURE [App::FeaturePython] Constraint028  label="Attachment-nut-governer-right"  # WARN: FeaturePython — macro-defined, semantics opaque (R4)
  Cascade = false
  Disabled = false
  Group = -> [ElementLink053,ElementLink054]
  Multiply = false
  _ConstraintType = 45
  _LinkVersion = 1
  _Parent = -> Constraints001
FEATURE [App::FeaturePython] ElementLink053  label="gov-mate-r@NUT Assembly"  # link proxy (typed FeaturePython)
  LinkTransform = true
  LinkedObject = -> Element064
  _LinkVersion = 1
  _Parent = -> Constraint028
FEATURE [App::FeaturePython] ElementLink054  label="nut-mate@Gouverner Assembly Right"  # link proxy (typed FeaturePython)
  LinkTransform = true
  LinkedObject = -> Element060
  Offset = pos=(0,0,0) rot=(0,0,1;4.71239rad)
  Placement = pos=(317.9,-5.68e-14,-80.7) rot=(0,-1,0;1.5708rad)
  _LinkVersion = 1
  _Parent = -> Constraint028
FEATURE [App::FeaturePython] Constraint029  label="Attachment-stepper-plate"  # WARN: FeaturePython — macro-defined, semantics opaque (R4)
  Cascade = false
  Disabled = false
  Group = -> [ElementLink055,ElementLink056]
  Multiply = false
  _ConstraintType = 45
  _LinkVersion = 1
  _Parent = -> Constraints001
FEATURE [App::FeaturePython] ElementLink055  label="plate-mate@NEMA23-76-Assembly"  # link proxy (typed FeaturePython)
  LinkTransform = true
  LinkedObject = -> Element025
  _LinkVersion = 1
  _Parent = -> Constraint029
FEATURE [App::FeaturePython] ElementLink056  label="motor-mate@Left plate Assembly"  # link proxy (typed FeaturePython)
  LinkTransform = true
  LinkedObject = -> Element026
  Offset = pos=(0,0,0) rot=(1,0,0;3.14159rad)
  Placement = pos=(-55.7,-647.7,-1.705e-13) rot=(0,0,1;3.14159rad)
  _LinkVersion = 1
  _Parent = -> Constraint029
FEATURE [App::DocumentObjectGroup] Group  label="Components"
  ExportMode = 1
  Group = -> [Assembly,Assembly002]
  _GroupVersion = 1
FEATURE [Part::FeaturePython] Assembly002  label="1/4x1/2 screw and washer Assembly"  # WARN: FeaturePython — macro-defined, semantics opaque (R4)
  AutoRelax = true
  BuildShape = 0
  Freeze = false
  Group = -> [Constraints002,Elements002,Parts002]
  Verbose = false
  _LinkVersion = 1
  _SolverType = 1
  _Version = 1
FEATURE [App::FeaturePython] Constraints002  # WARN: FeaturePython — macro-defined, semantics opaque (R4)
  Group = -> [Constraint030,Constraint031]
  _LinkVersion = 1
  _Version = 1
FEATURE [App::FeaturePython] Elements002  # WARN: FeaturePython — macro-defined, semantics opaque (R4)
  Group = -> [_Element,_Element001,Element065]
  _LinkVersion = 1
FEATURE [App::FeaturePython] Constraint030  label="Locked002"  # WARN: FeaturePython — macro-defined, semantics opaque (R4)
  Disabled = false
  Group = -> [ElementLink057]
  _ConstraintType = 0
  _LinkVersion = 1
  _Parent = -> Constraints002
FEATURE [App::FeaturePython] ElementLink057  label="_Element"  # link proxy (typed FeaturePython)
  LinkTransform = true
  LinkedObject = -> _Element
  _LinkVersion = 1
  _Parent = -> Constraint030
FEATURE [Part::FeaturePython] _Element  # link proxy (typed FeaturePython)
  Detach = false
  LinkTransform = true
  LinkedObject = -> Screw [Edge4]
  _LinkVersion = 1
  _Parent = -> Elements002
FEATURE [App::FeaturePython] Constraint031  label="Attachment001"  # WARN: FeaturePython — macro-defined, semantics opaque (R4)
  Cascade = false
  Disabled = false
  Group = -> [ElementLink058,ElementLink059]
  Multiply = false
  _ConstraintType = 45
  _LinkVersion = 1
  _Parent = -> Constraints002
FEATURE [App::FeaturePython] ElementLink058  label="_Element001"  # link proxy (typed FeaturePython)
  LinkTransform = true
  LinkedObject = -> _Element001
  _LinkVersion = 1
  _Parent = -> Constraint031
FEATURE [Part::FeaturePython] _Element001  # link proxy (typed FeaturePython)
  Detach = false
  LinkTransform = true
  LinkedObject = -> Washer [Edge1]
  _LinkVersion = 1
  _Parent = -> Elements002
FEATURE [App::FeaturePython] ElementLink059  label="_Element"  # link proxy (typed FeaturePython)
  LinkTransform = true
  LinkedObject = -> _Element
  _LinkVersion = 1
  _Parent = -> Constraint031
FEATURE [Part::FeaturePython] Element065  label="mate"  # link proxy (typed FeaturePython)
  Detach = false
  LinkTransform = true
  LinkedObject = -> Washer [Edge5]
  _LinkVersion = 1
  _Parent = -> Elements002
FEATURE [App::FeaturePython] Constraint032  label="Attachment002"  # WARN: FeaturePython — macro-defined, semantics opaque (R4)
  Cascade = false
  Disabled = false
  Group = -> [ElementLink060,ElementLink061]
  Multiply = false
  _ConstraintType = 45
  _LinkVersion = 1
  _Parent = -> Constraints
FEATURE [App::FeaturePython] ElementLink060  label="_Element002"  # link proxy (typed FeaturePython)
  LinkTransform = true
  LinkedObject = -> _Element002
  Offset = pos=(0,0,0) rot=(1,0,0;3.14159rad)
  Placement = pos=(-123.62,0,-25.4) rot=(0,1,0;3.14159rad)
  _LinkVersion = 1
  _Parent = -> Constraint032
FEATURE [Part::FeaturePython] _Element002  # link proxy (typed FeaturePython)
  Detach = false
  LinkTransform = true
  LinkedObject = -> Link025 [Link025_i0.1.$mate.]
  _LinkVersion = 1
  _Parent = -> Elements
FEATURE [App::FeaturePython] ElementLink061  label="_Element003"  # link proxy (typed FeaturePython)
  LinkTransform = true
  LinkedObject = -> _Element003
  _LinkVersion = 1
  _Parent = -> Constraint032
FEATURE [Part::FeaturePython] _Element003  # link proxy (typed FeaturePython)
  Detach = false
  LinkTransform = true
  LinkedObject = -> Link024 [Sketch007.Edge2]
  _LinkVersion = 1
  _Parent = -> Elements
FEATURE [App::FeaturePython] Constraint033  label="Attachment003"  # WARN: FeaturePython — macro-defined, semantics opaque (R4)
  Cascade = false
  Disabled = false
  Group = -> [ElementLink062,ElementLink063]
  Multiply = false
  _ConstraintType = 45
  _LinkVersion = 1
  _Parent = -> Constraints
FEATURE [App::FeaturePython] ElementLink062  label="_Element004"  # link proxy (typed FeaturePython)
  LinkTransform = true
  LinkedObject = -> _Element004
  Offset = pos=(0,0,0) rot=(1,0,0;3.14159rad)
  Placement = pos=(-123.62,0,-25.4) rot=(0,1,0;3.14159rad)
  _LinkVersion = 1
  _Parent = -> Constraint033
FEATURE [Part::FeaturePython] _Element004  # link proxy (typed FeaturePython)
  Detach = false
  LinkTransform = true
  LinkedObject = -> Link025 [Link025_i1.1.$mate.]
  _LinkVersion = 1
  _Parent = -> Elements
FEATURE [App::FeaturePython] ElementLink063  label="_Element005"  # link proxy (typed FeaturePython)
  LinkTransform = true
  LinkedObject = -> _Element005
  _LinkVersion = 1
  _Parent = -> Constraint033
FEATURE [Part::FeaturePython] _Element005  # link proxy (typed FeaturePython)
  Detach = false
  LinkTransform = true
  LinkedObject = -> Link024 [Sketch007.Edge6]
  _LinkVersion = 1
  _Parent = -> Elements
FEATURE [App::FeaturePython] Constraint034  label="Attachment004"  # WARN: FeaturePython — macro-defined, semantics opaque (R4)
  Cascade = false
  Disabled = false
  Group = -> [ElementLink064,ElementLink065]
  Multiply = false
  _ConstraintType = 45
  _LinkVersion = 1
  _Parent = -> Constraints
FEATURE [App::FeaturePython] ElementLink064  label="_Element006"  # link proxy (typed FeaturePython)
  LinkTransform = true
  LinkedObject = -> _Element006
  Offset = pos=(0,0,0) rot=(1,0,0;3.14159rad)
  Placement = pos=(-123.62,0,-25.4) rot=(0,1,0;3.14159rad)
  _LinkVersion = 1
  _Parent = -> Constraint034
FEATURE [Part::FeaturePython] _Element006  # link proxy (typed FeaturePython)
  Detach = false
  LinkTransform = true
  LinkedObject = -> Link025 [Link025_i2.1.$mate.]
  _LinkVersion = 1
  _Parent = -> Elements
FEATURE [App::FeaturePython] ElementLink065  label="_Element007"  # link proxy (typed FeaturePython)
  LinkTransform = true
  LinkedObject = -> _Element007
  _LinkVersion = 1
  _Parent = -> Constraint034
FEATURE [Part::FeaturePython] _Element007  # link proxy (typed FeaturePython)
  Detach = false
  LinkTransform = true
  LinkedObject = -> Link024 [Sketch007.Edge4]
  _LinkVersion = 1
  _Parent = -> Elements
FEATURE [App::FeaturePython] Constraint035  label="Attachment005"  # WARN: FeaturePython — macro-defined, semantics opaque (R4)
  Cascade = false
  Disabled = false
  Group = -> [ElementLink066,ElementLink067]
  Multiply = false
  _ConstraintType = 45
  _LinkVersion = 1
  _Parent = -> Constraints
FEATURE [App::FeaturePython] ElementLink066  label="_Element008"  # link proxy (typed FeaturePython)
  LinkTransform = true
  LinkedObject = -> _Element008
  Offset = pos=(0,0,0) rot=(1,0,0;3.14159rad)
  Placement = pos=(-123.62,0,-25.4) rot=(0,1,0;3.14159rad)
  _LinkVersion = 1
  _Parent = -> Constraint035
FEATURE [Part::FeaturePython] _Element008  # link proxy (typed FeaturePython)
  Detach = false
  LinkTransform = true
  LinkedObject = -> Link025 [Link025_i3.1.$mate.]
  _LinkVersion = 1
  _Parent = -> Elements
FEATURE [App::FeaturePython] ElementLink067  label="_Element009"  # link proxy (typed FeaturePython)
  LinkTransform = true
  LinkedObject = -> _Element009
  _LinkVersion = 1
  _Parent = -> Constraint035
FEATURE [Part::FeaturePython] _Element009  # link proxy (typed FeaturePython)
  Detach = false
  LinkTransform = true
  LinkedObject = -> Link024 [Sketch007.Edge1]
  _LinkVersion = 1
  _Parent = -> Elements
FEATURE [Part::FeaturePython] Element066  label="limit-mate@Left plate Assembly"  # link proxy (typed FeaturePython)
  Detach = false
  LinkTransform = true
  LinkedObject = -> Link004 [1.$limit-mate.]
  _LinkVersion = 1
  _Parent = -> Elements001
FEATURE [Part::FeaturePython] Element067  label="mate l@Limit sensor Assembly"  # link proxy (typed FeaturePython)
  Detach = false
  LinkTransform = true
  LinkedObject = -> Link026 [1.$mate l.]
  _LinkVersion = 1
  _Parent = -> Elements001
FEATURE [App::FeaturePython] Constraint036  label="Attachment-limit-sensor"  # WARN: FeaturePython — macro-defined, semantics opaque (R4)
  Cascade = false
  Disabled = false
  Group = -> [ElementLink068,ElementLink069]
  Multiply = false
  _ConstraintType = 45
  _LinkVersion = 1
  _Parent = -> Constraints001
FEATURE [App::FeaturePython] ElementLink068  label="mate l@Limit sensor Assembly"  # link proxy (typed FeaturePython)
  LinkTransform = true
  LinkedObject = -> Element067
  Offset = pos=(0,0,0) rot=(0,0,1;1.5708rad)
  Placement = pos=(-22.8,0,114) rot=(0,-1,0;1.5708rad)
  _LinkVersion = 1
  _Parent = -> Constraint036
FEATURE [App::FeaturePython] ElementLink069  label="limit-mate@Left plate Assembly"  # link proxy (typed FeaturePython)
  LinkTransform = true
  LinkedObject = -> Element066
  Offset = pos=(0,0,0) rot=(1,0,0;3.14159rad)
  Placement = pos=(-136.8,-609.6,-1.563e-13) rot=(0,0,1;3.14159rad)
  _LinkVersion = 1
  _Parent = -> Constraint036
FEATURE [Part::FeaturePython] _Element010  label="_top-beam-mate@Right plate Assembly"  # link proxy (typed FeaturePython)
  Detach = false
  LinkTransform = true
  LinkedObject = -> Link005 [1.$Element044.]
  _LinkVersion = 0
  _Parent = -> Elements001

RESOLVED EXTERNAL PARTS (link-assembly join: the EXTERNAL_REF files above that resolve inside this repo's crawl, each included once):
---- part parts/BallNut.FCStd = doc fcstd_aec63517059e ----
FCSTD DOCUMENT  (FreeCAD 2021.614R24301 +3747 (Git))
Label: BallNut
License: Creative Commons Attribution
LicenseURL: http://creativecommons.org/licenses/by/4.0/
objects: App::FeaturePython×25, Part::FeaturePython×22, Sketcher::SketchObject×9, PartDesign::Pocket×6, App::LinkElement×6, PartDesign::Pad×3, App::Link×3, PartDesign::Chamfer×2, PartDesign::Body×2, PartDesign::Plane×1, PartDesign::Line×1, App::DocumentObjectGroup×1
note: 67 computed .brp shape members not serialized (recipe doc carries the construction recipe); baked Part::Feature solids carry a one-line shape summary decoded from their .brp

FEATURE [Sketcher::SketchObject] Sketch
  FullyConstrained = true
  MapMode = 5
  Placement = pos=(0,0,0) rot=(1,0,0;1.5708rad)
  Support = -> [XZ_Plane]
  sketch-geometry (9):
    g0: Circle CenterX=0 CenterY=0 CenterZ=0 NormalX=0 NormalY=0 NormalZ=1 AngleXU=0 Radius=14
    g1: LineSegment StartX=-26.125 StartY=-20 StartZ=0 EndX=26.125 EndY=-20 EndZ=0
    g2: LineSegment StartX=26.125 StartY=-20 StartZ=0 EndX=26.125 EndY=8 EndZ=0
    g3: LineSegment StartX=26.125 StartY=8 StartZ=0 EndX=14 EndY=20 EndZ=0
    g4: LineSegment StartX=14 StartY=20 StartZ=0 EndX=-14 EndY=20 EndZ=0
    g5: LineSegment StartX=-14 StartY=20 StartZ=0 EndX=-26.125 EndY=8 EndZ=0
    g6: LineSegment StartX=-26.125 StartY=8 StartZ=0 EndX=-26.125 EndY=-20 EndZ=0
    g7: GeomPoint [constr] X=0 Y=-20 Z=0
    g8: GeomPoint [constr] X=2e-16 Y=20 Z=0
  constraints (21):
    c: Coincident(g0,g-1)
    c: Horizontal(g1)
    c: Coincident(g1,g2)
    c: Vertical(g2)
    c: Coincident(g2,g3)
    c: Coincident(g3,g4)
    c: Horizontal(g4)
    c: Coincident(g4,g5)
    c: Coincident(g5,g6)
    c: Coincident(g6,g1)
    c: Vertical(g6)
    c: Horizontal(g5,g2)
    c: PointOnObject(g7,g-2)
    c: Symmetric(g4,g3,g8)
    c: Symmetric(g1,g1,g7)
    c: DistanceY(g1,g3) = 40
    c: Symmetric(g8,g7,g0)
    c: DistanceX(g1,g1) = 52.25
    c: DistanceY(g2,g2) = 28
    c: DistanceX(g4,g4) = 28
    c: Diameter(g0) = 28
FEATURE [PartDesign::Pad] Pad
  ClaimChildren = false
  Direction = (1,1,1)
  Fit = 0
  FitJoin = 0
  InnerFit = 0
  InnerFitJoin = 0
  InnerTaperAngle = 0
  InnerTaperAngleRev = 0
  Length = 40.25
  Length2 = 100
  Linearize = true
  Midplane = true
  NewSolid = false
  Placement = pos=(0,0,0) rot=(1,0,0;1.5708rad)
  Profile = -> Sketch
  Refine = true
  Suppress = false
  Type = 0
FEATURE [Sketcher::SketchObject] Sketch001
  FullyConstrained = true
  MapMode = 5
  Placement = pos=(0,-20.125,4.4e-15) rot=(1,0,0;1.5708rad)
  Support = -> [Pad]
  sketch-geometry (8):
    g0: Circle CenterX=-19 CenterY=0 CenterZ=0 NormalX=0 NormalY=0 NormalZ=1 AngleXU=0 Radius=2.1
    g1: Circle CenterX=19 CenterY=0 CenterZ=0 NormalX=0 NormalY=0 NormalZ=1 AngleXU=0 Radius=2.1
    g2: Circle CenterX=13.435 CenterY=-13.435 CenterZ=0 NormalX=0 NormalY=0 NormalZ=1 AngleXU=0 Radius=2.1
    g3: Circle CenterX=-13.435 CenterY=-13.435 CenterZ=0 NormalX=0 NormalY=0 NormalZ=1 AngleXU=0 Radius=2.1
    g4: Circle CenterX=-13.435 CenterY=13.435 CenterZ=0 NormalX=0 NormalY=0 NormalZ=1 AngleXU=0 Radius=2.1
    g5: Circle CenterX=13.435 CenterY=13.435 CenterZ=0 NormalX=0 NormalY=0 NormalZ=1 AngleXU=0 Radius=2.1
    g6: Circle [constr] CenterX=0 CenterY=0 CenterZ=0 NormalX=0 NormalY=0 NormalZ=1 AngleXU=0 Radius=19
    g7: LineSegment [constr] StartX=0 StartY=0 StartZ=0 EndX=13.435 EndY=13.435 EndZ=0
  constraints (22):
    c: PointOnObject(g0,g-1)
    c: PointOnObject(g1,g-1)
    c: Coincident(g6,g-1)
    c: Diameter(g6) = 38
    c: Equal(g1,g5)
    c: Equal(g5,g4)
    c: Equal(g4,g0)
    c: Equal(g0,g3)
    c: Equal(g3,g2)
    c: PointOnObject(g5,g6)
    c: PointOnObject(g4,g6)
    c: PointOnObject(g0,g6)
    c: PointOnObject(g1,g6)
    c: PointOnObject(g2,g6)
    c: PointOnObject(g3,g6)
    c: Vertical(g4,g3)
    c: Vertical(g5,g2)
    c: Horizontal(g4,g5)
    c: Diameter(g4) = 4.2
    c: Coincident(g7,g6)
    c: Coincident(g7,g5)
    c: Angle(g-1,g7) = 0.785398
FEATURE [PartDesign::Pocket] Pocket
  BaseFeature = -> Pad
  ClaimChildren = false
  Fit = 0
  FitJoin = 0
  InnerFit = 0
  InnerFitJoin = 0
  InnerTaperAngle = 0
  InnerTaperAngleRev = 0
  Length = 16
  Length2 = 100
  Linearize = true
  NewSolid = false
  Placement = pos=(0,0,0) rot=(1,0,0;1.5708rad)
  Profile = -> Sketch001
  Refine = true
  Suppress = false
  Type = 0
FEATURE [Sketcher::SketchObject] Sketch002
  FullyConstrained = true
  MapMode = 5
  Placement = pos=(0,-8.8e-15,-20) rot=(1,0,0;3.14159rad)
  Support = -> [Pocket]
  sketch-geometry (4):
    g0: Circle CenterX=-20 CenterY=12 CenterZ=0 NormalX=0 NormalY=0 NormalZ=1 AngleXU=0 Radius=2.1
    g1: Circle CenterX=20 CenterY=12 CenterZ=0 NormalX=0 NormalY=0 NormalZ=1 AngleXU=0 Radius=2.1
    g2: Circle CenterX=-20 CenterY=-12 CenterZ=0 NormalX=0 NormalY=0 NormalZ=1 AngleXU=0 Radius=2.1
    g3: Circle CenterX=20 CenterY=-12 CenterZ=0 NormalX=0 NormalY=0 NormalZ=1 AngleXU=0 Radius=2.1
  constraints (11):
    c: Equal(g3,g1)
    c: Equal(g1,g0)
    c: Equal(g0,g2)
    c: Diameter(g0) = 4.2
    c: Symmetric(g0,g3,g-1)
    c: Horizontal(g0,g1)
    c: Vertical(g0,g2)
    c: Vertical(g1,g3)
    c: Horizontal(g3,g2)
    c: DistanceY(g2,g0) = 24
    c: DistanceX(g0,g1) = 40
FEATURE [PartDesign::Pocket] Pocket001
  BaseFeature = -> Pocket
  ClaimChildren = false
  Fit = 0
  FitJoin = 0
  InnerFit = 0
  InnerFitJoin = 0
  InnerTaperAngle = 0
  InnerTaperAngleRev = 0
  Length = 16
  Length2 = 100
  Linearize = true
  NewSolid = false
  Placement = pos=(0,0,0) rot=(1,0,0;1.5708rad)
  Profile = -> Sketch002
  Refine = true
  Suppress = false
  Type = 0
FEATURE [PartDesign::Chamfer] Chamfer
  Angle = 45
  Base = -> Pocket001 [Edge10,Edge2,Edge15,Edge14,Edge13,Edge12,Edge37,Edge9,Edge1,Edge4,Edge28,Edge38,Edge16,Edge3,Edge17,Edge19,Edge20,Edge18,Edge11,Edge25,Edge22,Edge21,Edge24,Edge26,Edge27,Edge23,Edge5,Edge7,Edge8,Edge6]
  BaseFeature = -> Pocket001
  ChamferType = 0
  FlipDirection = false
  NewSolid = false
  Placement = pos=(0,0,0) rot=(1,0,0;1.5708rad)
  Refine = true
  Size = 1
  Size2 = 1
  SupportTransform = false
  Suppress = false
FEATURE [Sketcher::SketchObject] Sketch003
  FullyConstrained = true
  MapMode = 5
  Placement = pos=(0,0,0) rot=(1,0,0;1.5708rad)
  Support = -> [XZ_Plane001]
  sketch-geometry (1):
    g0: Circle CenterX=0 CenterY=0 CenterZ=0 NormalX=0 NormalY=0 NormalZ=1 AngleXU=0 Radius=14
  constraints (2):
    c: Coincident(g0,g-1)
    c: Diameter(g0) = 28
FEATURE [PartDesign::Pad] Pad001
  ClaimChildren = false
  Direction = (1,1,1)
  Fit = 0
  FitJoin = 0
  InnerFit = 0
  InnerFitJoin = 0
  InnerTaperAngle = 0
  InnerTaperAngleRev = 0
  Length = 32
  Length2 = 100
  Linearize = true
  Midplane = true
  NewSolid = false
  Placement = pos=(0,0,0) rot=(1,0,0;1.5708rad)
  Profile = -> Sketch003
  Refine = true
  Suppress = false
  Type = 0
FEATURE [Sketcher::SketchObject] Sketch004
  FullyConstrained = true
  MapMode = 5
  Placement = pos=(0,-16,3.5e-15) rot=(1,0,0;1.5708rad)
  Support = -> [Pad001]
  sketch-geometry (12):
    g0: ArcOfCircle CenterX=0 CenterY=0 CenterZ=0 NormalX=0 NormalY=0 NormalZ=1 AngleXU=0 Radius=24 StartAngle=2.15648 EndAngle=4.1267
    g1: Circle [constr] CenterX=0 CenterY=0 CenterZ=0 NormalX=0 NormalY=0 NormalZ=1 AngleXU=0 Radius=19
    g2: LineSegment StartX=-13.2665 StartY=20 StartZ=0 EndX=13.2665 EndY=20 EndZ=0
    g3: LineSegment StartX=-13.2665 StartY=-20 StartZ=0 EndX=13.2665 EndY=-20 EndZ=0
    g4: ArcOfCircle CenterX=0 CenterY=0 CenterZ=0 NormalX=0 NormalY=0 NormalZ=1 AngleXU=0 Radius=24 StartAngle=5.29807 EndAngle=7.2683
    g5: Circle CenterX=-19 CenterY=0 CenterZ=0 NormalX=0 NormalY=0 NormalZ=1 AngleXU=0 Radius=2.75
    g6: Circle CenterX=-13.435 CenterY=13.435 CenterZ=0 NormalX=0 NormalY=0 NormalZ=1 AngleXU=0 Radius=2.75
    g7: Circle CenterX=13.435 CenterY=13.435 CenterZ=0 NormalX=0 NormalY=0 NormalZ=1 AngleXU=0 Radius=2.75
    g8: Circle CenterX=19 CenterY=0 CenterZ=0 NormalX=0 NormalY=0 NormalZ=1 AngleXU=0 Radius=2.75
    g9: Circle CenterX=13.435 CenterY=-13.435 CenterZ=0 NormalX=0 NormalY=0 NormalZ=1 AngleXU=0 Radius=2.75
    g10: Circle CenterX=-13.435 CenterY=-13.435 CenterZ=0 NormalX=0 NormalY=0 NormalZ=1 AngleXU=0 Radius=2.75
    g11: LineSegment [constr] StartX=0 StartY=0 StartZ=0 EndX=13.435 EndY=13.435 EndZ=0
  constraints (34):
    c: Coincident(g0,g-1)
    c: Coincident(g1,g0)
    c: Diameter(g1) = 38
    c: Diameter(g0) = 48
    c: Horizontal(g2)
    c: Horizontal(g3)
    c: Symmetric(g3,g2,g0)
    c: DistanceY(g3,g2) = 40
    c: Coincident(g0,g2)
    c: Coincident(g4,g2)
    c: Equal(g0,g4)
    c: Coincident(g0,g3)
    c: PointOnObject(g4,g3)
    c: Coincident(g0,g4)
    c: PointOnObject(g5,g1)
    c: PointOnObject(g6,g1)
    c: PointOnObject(g7,g1)
    c: PointOnObject(g8,g1)
    c: PointOnObject(g9,g1)
    c: PointOnObject(g8,g-1)
    c: PointOnObject(g5,g-1)
    c: PointOnObject(g10,g1)
    c: Vertical(g10,g6)
    c: Vertical(g7,g9)
    c: Horizontal(g7,g6)
    c: Equal(g7,g8)
    c: Equal(g8,g9)
    c: Equal(g9,g6)
    c: Equal(g6,g5)
    c: Equal(g5,g10)
    c: Diameter(g6) = 5.5
    c: Coincident(g11,g0)
    c: Coincident(g11,g7)
    c: Angle(g-1,g11) = 0.785398
FEATURE [PartDesign::Pad] Pad002
  BaseFeature = -> Pad001
  ClaimChildren = false
  Direction = (1,1,1)
  Fit = 0
  FitJoin = 0
  InnerFit = 0
  InnerFitJoin = 0
  InnerTaperAngle = 0
  InnerTaperAngleRev = 0
  Length = 10
  Length2 = 100
  Linearize = true
  NewSolid = false
  Placement = pos=(0,0,0) rot=(1,0,0;1.5708rad)
  Profile = -> Sketch004
  Refine = true
  Suppress = false
  Type = 0
FEATURE [Sketcher::SketchObject] Sketch005
  FullyConstrained = true
  MapMode = 5
  Placement = pos=(0,-26,2.03e-14) rot=(1,0,0;1.5708rad)
  Support = -> [Pad002]
  sketch-geometry (1):
    g0: Circle CenterX=0 CenterY=0 CenterZ=0 NormalX=0 NormalY=0 NormalZ=1 AngleXU=0 Radius=8
  constraints (2):
    c: Coincident(g0,g-1)
    c: Diameter(g0) = 16
FEATURE [PartDesign::Pocket] Pocket002
  BaseFeature = -> Pad002
  ClaimChildren = false
  Fit = 0
  FitJoin = 0
  InnerFit = 0
  InnerFitJoin = 0
  InnerTaperAngle = 0
  InnerTaperAngleRev = 0
  Length = 5
  Length2 = 100
  Linearize = true
  NewSolid = false
  Placement = pos=(0,0,0) rot=(1,0,0;1.5708rad)
  Profile = -> Sketch005
  Refine = true
  Suppress = false
  Type = 1
FEATURE [Sketcher::SketchObject] Sketch006
  FullyConstrained = true
  MapMode = 5
  Placement = pos=(0,-26,2.03e-14) rot=(1,0,0;1.5708rad)
  Support = -> [Pocket002]
  sketch-geometry (1):
    g0: Circle CenterX=0 CenterY=0 CenterZ=0 NormalX=0 NormalY=0 NormalZ=1 AngleXU=0 Radius=11
  constraints (2):
    c: Coincident(g0,g-1)
    c: Diameter(g0) = 22
FEATURE [PartDesign::Pocket] Pocket003
  BaseFeature = -> Pocket002
  ClaimChildren = false
  Fit = 0
  FitJoin = 0
  InnerFit = 0
  InnerFitJoin = 0
  InnerTaperAngle = 0
  InnerTaperAngleRev = 0
  Length = 1
  Length2 = 100
  Linearize = true
  NewSolid = false
  Placement = pos=(0,0,0) rot=(1,0,0;1.5708rad)
  Profile = -> Sketch006
  Refine = true
  Suppress = false
  Type = 0
FEATURE [Sketcher::SketchObject] Sketch007
  FullyConstrained = true
  MapMode = 5
  Placement = pos=(0,16,-3.5e-15) rot=(-1,0,0;1.5708rad)
  Support = -> [Pocket003]
  sketch-geometry (1):
    g0: Circle CenterX=0 CenterY=0 CenterZ=0 NormalX=0 NormalY=0 NormalZ=1 AngleXU=0 Radius=11
  constraints (2):
    c: Coincident(g0,g-1)
    c: Diameter(g0) = 22
FEATURE [PartDesign::Pocket] Pocket004
  BaseFeature = -> Pocket003
  ClaimChildren = false
  Fit = 0
  FitJoin = 0
  InnerFit = 0
  InnerFitJoin = 0
  InnerTaperAngle = 0
  InnerTaperAngleRev = 0
  Length = 1
  Length2 = 100
  Linearize = true
  NewSolid = false
  Placement = pos=(0,0,0) rot=(1,0,0;1.5708rad)
  Profile = -> Sketch007
  Refine = true
  Suppress = false
  Type = 0
FEATURE [PartDesign::Plane] DatumPlane
  AttachmentOffset = pos=(0,0,0) rot=(1,0,0;0.392699rad)
  Length = 42
  MapMode = 5
  MinimumLength = 10
  MinimumWidth = 10
  Placement = pos=(0,0,0) rot=(0.639338,0.639338,0.427192;2.33414rad)
  ResizeMode = 0
  Support = -> [YZ_Plane001]
  Width = 55.324
FEATURE [Sketcher::SketchObject] Sketch008
  ExternalGeometry = -> [Pocket004]
  FullyConstrained = true
  MapMode = 5
  Placement = pos=(0,0,0) rot=(0.485653,-0.485653,-0.726831;1.88458rad)
  Support = -> [DatumPlane]
  sketch-geometry (3):
    g0: Circle CenterX=21 CenterY=0 CenterZ=0 NormalX=0 NormalY=0 NormalZ=1 AngleXU=0 Radius=2.5
    g1: LineSegment [constr] StartX=16 StartY=13.4007 StartZ=0 EndX=21 EndY=0 EndZ=0
    g2: LineSegment [constr] StartX=21 StartY=0 StartZ=0 EndX=26 EndY=13.4007 EndZ=0
  constraints (7):
    c: PointOnObject(g0,g-1)
    c: Coincident(g1,g-3)
    c: Coincident(g1,g0)
    c: Coincident(g2,g0)
    c: Coincident(g2,g-4)
    c: Equal(g2,g1)
    c: Diameter(g0) = 5
FEATURE [PartDesign::Pocket] Pocket005
  BaseFeature = -> Pocket004
  ClaimChildren = false
  Fit = 0
  FitJoin = 0
  InnerFit = 0
  InnerFitJoin = 0
  InnerTaperAngle = 0
  InnerTaperAngleRev = 0
  Length = 5
  Length2 = 100
  Linearize = true
  NewSolid = false
  Placement = pos=(0,0,0) rot=(1,0,0;1.5708rad)
  Profile = -> Sketch008
  Refine = true
  Reversed = true
  Suppress = false
  Type = 1
FEATURE [PartDesign::Chamfer] Chamfer001
  Angle = 45
  Base = -> Pocket005 [Edge35,Edge43,Edge24,Edge25,Edge26,Edge22,Edge21,Edge20,Edge23,Edge14,Edge16,Edge17,Edge11,Edge12,Edge13]
  BaseFeature = -> Pocket005
  ChamferType = 0
  FlipDirection = false
  NewSolid = false
  Placement = pos=(0,0,0) rot=(1,0,0;1.5708rad)
  Refine = true
  Size = 0.5
  Size2 = 1
  SupportTransform = false
  Suppress = false
FEATURE [PartDesign::Body] Body001  label="SFU1605"
  AutoGroupSolids = false
  ExportMode = 0
  Group = -> [Sketch003,Pad001,Sketch004,Pad002,Sketch005,Pocket002,Sketch006,Pocket003,Sketch007,Pocket004,DatumPlane,Sketch008,Pocket005,Chamfer001]
  Origin = -> Origin001
  Placement = pos=(0,-5,0) rot=(0,0,1;0rad)
  Tip = -> Chamfer001
  _ExportChildren = -> [Pad001,Pad002,Pocket002,Pocket003,Pocket004,DatumPlane,Pocket005,Chamfer001]
  _GroupVersion = 1
FEATURE [App::Link] Link  label="Link(SFU1605)"
  AutoLinkLabel = true
  LinkPlacement = pos=(4e-16,-5,-2.7e-15) rot=(0,0,1;0rad)
  LinkedObject = -> Body001
  Placement = pos=(4e-16,-5,-2.7e-15) rot=(0,0,1;0rad)
  SyncGroupVisibility = false
  _LinkVersion = 1
FEATURE [App::Link] Link001  label="Link001(DSG16)"
  AutoLinkLabel = true
  LinkPlacement = pos=(0,-0.875,-9.7e-15) rot=(0,0,1;0rad)
  LinkedObject = -> Body
  Placement = pos=(0,-0.875,-9.7e-15) rot=(0,0,1;0rad)
  SyncGroupVisibility = false
  _LinkVersion = 1
FEATURE [PartDesign::Line] DatumLine
  AttacherType = Attacher::AttachEngineLine
  Length = 40.25
  MapMode = 19
  MinimumLength = 10
  Placement = pos=(0,-19.125,4e-15) rot=(1,0,0;1.5708rad)
  ResizeMode = 0
  Support = -> [Chamfer]
FEATURE [PartDesign::Body] Body  label="DSG16"
  AutoGroupSolids = false
  ExportMode = 0
  Group = -> [Sketch,Pad,Sketch001,Pocket,Sketch002,Pocket001,Chamfer,DatumLine]
  Origin = -> Origin
  Tip = -> Chamfer
  _ExportChildren = -> [Pad,Pocket,Pocket001,Chamfer,DatumLine]
  _GroupVersion = 1
FEATURE [Part::FeaturePython] Screw  label="M5x20-Screw"  # Fasteners workbench fastener (typed FeaturePython)
  Placement = pos=(0,-51,0) rot=(0,0,1;0rad)
  diameter = 3
  invert = false
  length = 5
  lengthCustom = 20
  matchOuter = false
  offset = 0
  thread = false
  type = 39
FEATURE [App::DocumentObjectGroup] Group  label="Components"
  ExportMode = 1
  Group = -> [Body,Body001,Screw]
  _GroupVersion = 1
FEATURE [App::LinkElement] Link002_i0
  LinkPlacement = pos=(-13.435,20,13.435) rot=(1,0,0;1.5708rad)
  LinkedObject = -> Screw
  Placement = pos=(-13.435,20,13.435) rot=(1,0,0;1.5708rad)
  _LinkVersion = 0
FEATURE [App::LinkElement] Link002_i1
  LinkPlacement = pos=(13.435,20,13.435) rot=(1,0,0;1.5708rad)
  LinkedObject = -> Screw
  Placement = pos=(13.435,20,13.435) rot=(1,0,0;1.5708rad)
  _LinkVersion = 0
FEATURE [App::LinkElement] Link002_i2
  LinkPlacement = pos=(19,20,6.78e-14) rot=(1,0,0;1.5708rad)
  LinkedObject = -> Screw
  Placement = pos=(19,20,6.78e-14) rot=(1,0,0;1.5708rad)
  _LinkVersion = 0
FEATURE [App::LinkElement] Link002_i3
  LinkPlacement = pos=(13.435,20,-13.435) rot=(1,0,0;1.5708rad)
  LinkedObject = -> Screw
  Placement = pos=(13.435,20,-13.435) rot=(1,0,0;1.5708rad)
  _LinkVersion = 0
FEATURE [App::LinkElement] Link002_i4
  LinkPlacement = pos=(-19,20,6.78e-14) rot=(1,0,0;1.5708rad)
  LinkedObject = -> Screw
  Placement = pos=(-19,20,6.78e-14) rot=(1,0,0;1.5708rad)
  _LinkVersion = 0
FEATURE [App::LinkElement] Link002_i5
  LinkPlacement = pos=(-13.435,20,-13.435) rot=(1,0,0;1.5708rad)
  LinkedObject = -> Screw
  Placement = pos=(-13.435,20,-13.435) rot=(1,0,0;1.5708rad)
  _LinkVersion = 0
FEATURE [App::Link] Link002  label="M5x20-Screw 6ct"
  AutoLinkLabel = true
  ElementCount = 6
  ElementList = -> [Link002_i0,Link002_i1,Link002_i2,Link002_i3,Link002_i4,Link002_i5]
  LinkPlacement = pos=(0,-51,0) rot=(0,0,1;0rad)
  LinkedObject = -> Screw
  Placement = pos=(0,-51,0) rot=(0,0,1;0rad)
  SyncGroupVisibility = false
  _LinkVersion = 1
FEATURE [Part::FeaturePython] Parts  # WARN: FeaturePython — macro-defined, semantics opaque (R4)
  Group = -> [Link,Link001,Link002]
  GroupMode = 0
  _LinkVersion = 1
FEATURE [Part::FeaturePython] Assembly  label="NUT Assembly"  # WARN: FeaturePython — macro-defined, semantics opaque (R4)
  AutoRelax = true
  BuildShape = 0
  Freeze = false
  Group = -> [Constraints,Elements,Parts]
  Verbose = false
  _LinkVersion = 1
  _SolverType = 1
  _Version = 1
FEATURE [App::FeaturePython] Constraints  # WARN: FeaturePython — macro-defined, semantics opaque (R4)
  Group = -> [Constraint006,Constraint007,Constraint,Constraint008,Constraint009,Constraint010,Constraint011,Constraint012]
  _LinkVersion = 1
  _Version = 1
FEATURE [App::FeaturePython] Elements  # WARN: FeaturePython — macro-defined, semantics opaque (R4)
  Group = -> [_Element012,_Element013,_Element014,Element,Element001,Element002,Element003,_Element,_Element015,_Element016,_Element017,_Element018,_Element019,_Element020,_Element021,_Element022,_Element023,_Element024,_Element025]
  _LinkVersion = 1
FEATURE [App::FeaturePython] Constraint006  label="Attachment006"  # WARN: FeaturePython — macro-defined, semantics opaque (R4)
  Cascade = false
  Disabled = false
  Group = -> [ElementLink012,ElementLink013]
  Multiply = false
  _ConstraintType = 45
  _LinkVersion = 1
  _Parent = -> Constraints
FEATURE [App::FeaturePython] ElementLink012  label="_Element012"  # link proxy (typed FeaturePython)
  LinkTransform = true
  LinkedObject = -> _Element012
  _LinkVersion = 1
  _Parent = -> Constraint006
FEATURE [Part::FeaturePython] _Element012  # link proxy (typed FeaturePython)
  Detach = false
  LinkTransform = true
  LinkedObject = -> Link001 [Chamfer.Edge58]
  _LinkVersion = 1
  _Parent = -> Elements
FEATURE [App::FeaturePython] ElementLink013  label="Nut-mate"  # link proxy (typed FeaturePython)
  LinkTransform = true
  LinkedObject = -> _Element013
  _LinkVersion = 1
  _Parent = -> Constraint006
FEATURE [Part::FeaturePython] _Element013  label="Nut-mate"  # link proxy (typed FeaturePython)
  Detach = false
  LinkTransform = true
  LinkedObject = -> Link [Chamfer001.Edge6]
  _LinkVersion = 1
  _Parent = -> Elements
FEATURE [App::FeaturePython] Constraint007  label="Locked"  # WARN: FeaturePython — macro-defined, semantics opaque (R4)
  Disabled = false
  Group = -> [ElementLink014]
  _ConstraintType = 0
  _LinkVersion = 1
  _Parent = -> Constraints
FEATURE [App::FeaturePython] ElementLink014  label="_Element014"  # link proxy (typed FeaturePython)
  LinkTransform = true
  LinkedObject = -> _Element014
  _LinkVersion = 1
  _Parent = -> Constraint007
FEATURE [Part::FeaturePython] _Element014  # link proxy (typed FeaturePython)
  Detach = false
  LinkTransform = true
  LinkedObject = -> Link001 [Chamfer.Face1]
  _LinkVersion = 1
  _Parent = -> Elements
FEATURE [Part::FeaturePython] Element  label="gov-mate"  # link proxy (typed FeaturePython)
  Detach = false
  LinkTransform = true
  LinkedObject = -> Link001 [Chamfer.Edge7]
  _LinkVersion = 1
  _Parent = -> Elements
FEATURE [Part::FeaturePython] Element001  label="Axis"  # link proxy (typed FeaturePython)
  Detach = false
  LinkTransform = true
  LinkedObject = -> Link001 [DatumLine.]
  _LinkVersion = 1
  _Parent = -> Elements
FEATURE [Part::FeaturePython] Element002  label="gov-mate-r"  # link proxy (typed FeaturePython)
  Detach = false
  LinkTransform = true
  LinkedObject = -> Link001 [Chamfer.Edge5]
  _LinkVersion = 1
  _Parent = -> Elements
FEATURE [Part::FeaturePython] Element003  label="shim-mate"  # link proxy (typed FeaturePython)
  Detach = false
  LinkTransform = true
  LinkedObject = -> Link001 [Chamfer.Edge8]
  _LinkVersion = 1
  _Parent = -> Elements
FEATURE [App::FeaturePython] Constraint  label="Attachment"  # WARN: FeaturePython — macro-defined, semantics opaque (R4)
  Cascade = false
  Disabled = false
  Group = -> [ElementLink,ElementLink015]
  Multiply = false
  _ConstraintType = 45
  _LinkVersion = 0
  _Parent = -> Constraints
FEATURE [App::FeaturePython] ElementLink  label="_Element"  # link proxy (typed FeaturePython)
  LinkTransform = true
  LinkedObject = -> _Element
  _LinkVersion = 0
  _Parent = -> Constraint
FEATURE [Part::FeaturePython] _Element  # link proxy (typed FeaturePython)
  Detach = false
  LinkTransform = true
  LinkedObject = -> Link002 [0.Edge4]
  _LinkVersion = 0
  _Parent = -> Elements
FEATURE [App::FeaturePython] ElementLink015  label="_Element015"  # link proxy (typed FeaturePython)
  LinkTransform = true
  LinkedObject = -> _Element015
  _LinkVersion = 0
  _Parent = -> Constraint
FEATURE [Part::FeaturePython] _Element015  # link proxy (typed FeaturePython)
  Detach = false
  LinkTransform = true
  LinkedObject = -> Link [Chamfer001.Edge40]
  _LinkVersion = 0
  _Parent = -> Elements
FEATURE [App::FeaturePython] Constraint008  label="Attachment007"  # WARN: FeaturePython — macro-defined, semantics opaque (R4)
  Cascade = false
  Disabled = false
  Group = -> [ElementLink016,ElementLink017]
  Multiply = false
  _ConstraintType = 45
  _LinkVersion = 0
  _Parent = -> Constraints
FEATURE [App::FeaturePython] ElementLink016  label="_Element016"  # link proxy (typed FeaturePython)
  LinkTransform = true
  LinkedObject = -> _Element016
  _LinkVersion = 0
  _Parent = -> Constraint008
FEATURE [Part::FeaturePython] _Element016  # link proxy (typed FeaturePython)
  Detach = false
  LinkTransform = true
  LinkedObject = -> Link002 [1.Edge4]
  _LinkVersion = 0
  _Parent = -> Elements
FEATURE [App::FeaturePython] ElementLink017  label="_Element017"  # link proxy (typed FeaturePython)
  LinkTransform = true
  LinkedObject = -> _Element017
  _LinkVersion = 0
  _Parent = -> Constraint008
FEATURE [Part::FeaturePython] _Element017  # link proxy (typed FeaturePython)
  Detach = false
  LinkTransform = true
  LinkedObject = -> Link [Chamfer001.Edge39]
  _LinkVersion = 0
  _Parent = -> Elements
FEATURE [App::FeaturePython] Constraint009  label="Attachment008"  # WARN: FeaturePython — macro-defined, semantics opaque (R4)
  Cascade = false
  Disabled = false
  Group = -> [ElementLink018,ElementLink019]
  Multiply = false
  _ConstraintType = 45
  _LinkVersion = 0
  _Parent = -> Constraints
FEATURE [App::FeaturePython] ElementLink018  label="_Element018"  # link proxy (typed FeaturePython)
  LinkTransform = true
  LinkedObject = -> _Element018
  _LinkVersion = 0
  _Parent = -> Constraint009
FEATURE [Part::FeaturePython] _Element018  # link proxy (typed FeaturePython)
  Detach = false
  LinkTransform = true
  LinkedObject = -> Link002 [2.Edge4]
  _LinkVersion = 0
  _Parent = -> Elements
FEATURE [App::FeaturePython] ElementLink019  label="_Element019"  # link proxy (typed FeaturePython)
  LinkTransform = true
  LinkedObject = -> _Element019
  _LinkVersion = 0
  _Parent = -> Constraint009
FEATURE [Part::FeaturePython] _Element019  # link proxy (typed FeaturePython)
  Detach = false
  LinkTransform = true
  LinkedObject = -> Link [Chamfer001.Edge38]
  _LinkVersion = 0
  _Parent = -> Elements
FEATURE [App::FeaturePython] Constraint010  label="Attachment009"  # WARN: FeaturePython — macro-defined, semantics opaque (R4)
  Cascade = false
  Disabled = false
  Group = -> [ElementLink020,ElementLink021]
  Multiply = false
  _ConstraintType = 45
  _LinkVersion = 0
  _Parent = -> Constraints
FEATURE [App::FeaturePython] ElementLink020  label="_Element020"  # link proxy (typed FeaturePython)
  LinkTransform = true
  LinkedObject = -> _Element020
  _LinkVersion = 0
  _Parent = -> Constraint010
FEATURE [Part::FeaturePython] _Element020  # link proxy (typed FeaturePython)
  Detach = false
  LinkTransform = true
  LinkedObject = -> Link002 [3.Edge4]
  _LinkVersion = 0
  _Parent = -> Elements
FEATURE [App::FeaturePython] ElementLink021  label="_Element021"  # link proxy (typed FeaturePython)
  LinkTransform = true
  LinkedObject = -> _Element021
  _LinkVersion = 0
  _Parent = -> Constraint010
FEATURE [Part::FeaturePython] _Element021  # link proxy (typed FeaturePython)
  Detach = false
  LinkTransform = true
  LinkedObject = -> Link [Chamfer001.Edge43]
  _LinkVersion = 0
  _Parent = -> Elements
FEATURE [App::FeaturePython] Constraint011  label="Attachment010"  # WARN: FeaturePython — macro-defined, semantics opaque (R4)
  Cascade = false
  Disabled = false
  Group = -> [ElementLink022,ElementLink023]
  Multiply = false
  _ConstraintType = 45
  _LinkVersion = 0
  _Parent = -> Constraints
FEATURE [App::FeaturePython] ElementLink022  label="_Element022"  # link proxy (typed FeaturePython)
  LinkTransform = true
  LinkedObject = -> _Element022
  _LinkVersion = 0
  _Parent = -> Constraint011
FEATURE [Part::FeaturePython] _Element022  # link proxy (typed FeaturePython)
  Detach = false
  LinkTransform = true
  LinkedObject = -> Link002 [4.Edge4]
  _LinkVersion = 0
  _Parent = -> Elements
FEATURE [App::FeaturePython] ElementLink023  label="_Element023"  # link proxy (typed FeaturePython)
  LinkTransform = true
  LinkedObject = -> _Element023
  _LinkVersion = 0
  _Parent = -> Constraint011
FEATURE [Part::FeaturePython] _Element023  # link proxy (typed FeaturePython)
  Detach = false
  LinkTransform = true
  LinkedObject = -> Link [Chamfer001.Edge41]
  _LinkVersion = 0
  _Parent = -> Elements
FEATURE [App::FeaturePython] Constraint012  label="Attachment011"  # WARN: FeaturePython — macro-defined, semantics opaque (R4)
  Cascade = false
  Disabled = false
  Group = -> [ElementLink024,ElementLink025]
  Multiply = false
  _ConstraintType = 45
  _LinkVersion = 0
  _Parent = -> Constraints
FEATURE [App::FeaturePython] ElementLink024  label="_Element024"  # link proxy (typed FeaturePython)
  LinkTransform = true
  LinkedObject = -> _Element024
  _LinkVersion = 0
  _Parent = -> Constraint012
FEATURE [Part::FeaturePython] _Element024  # link proxy (typed FeaturePython)
  Detach = false
  LinkTransform = true
  LinkedObject = -> Link002 [5.Edge4]
  _LinkVersion = 0
  _Parent = -> Elements
FEATURE [App::FeaturePython] ElementLink025  label="_Element025"  # link proxy (typed FeaturePython)
  LinkTransform = true
  LinkedObject = -> _Element025
  _LinkVersion = 0
  _Parent = -> Constraint012
FEATURE [Part::FeaturePython] _Element025  # link proxy (typed FeaturePython)
  Detach = false
  LinkTransform = true
  LinkedObject = -> Link [Chamfer001.Edge42]
  _LinkVersion = 0
  _Parent = -> Elements
---- part parts/Ballscrew.FCStd = doc fcstd_904fc7d7aa5a (101767 chars; too large to inline — full recipe in that document) ----
---- part parts/Extrusion.FCStd = doc fcstd_ad510d6255d3 (60963 chars; too large to inline — full recipe in that document) ----
---- part parts/HGH20CA.FCStd = doc fcstd_d22bc38b7fa2 ----
FCSTD DOCUMENT  (FreeCAD 2021.614R24301 +3747 (Git))
Label: HGH20CA
License: Creative Commons Attribution
LicenseURL: http://creativecommons.org/licenses/by/4.0/
objects: Part::FeaturePython×21, App::FeaturePython×20, Sketcher::SketchObject×11, PartDesign::Pad×6, PartDesign::Pocket×4, App::Link×4, PartDesign::Plane×2, PartDesign::Body×2, App::DocumentObjectGroup×2, PartDesign::Mirrored×1, PartDesign::Fillet×1, PartDesign::Line×1, PartDesign::Revolution×1
note: 74 computed .brp shape members not serialized (recipe doc carries the construction recipe); baked Part::Feature solids carry a one-line shape summary decoded from their .brp

FEATURE [Sketcher::SketchObject] Sketch
  FullyConstrained = true
  MapMode = 5
  Placement = pos=(0,0,0) rot=(1,0,0;1.5708rad)
  Support = -> [XZ_Plane]
  sketch-geometry (20):
    g0: LineSegment StartX=-21 StartY=30 StartZ=0 EndX=-11.5 EndY=30 EndZ=0
    g1: LineSegment StartX=22 StartY=29 StartZ=0 EndX=22 EndY=6.1 EndZ=0
    g2: LineSegment StartX=20.5 StartY=4.6 StartZ=0 EndX=-20.5 EndY=4.6 EndZ=0
    g3: LineSegment StartX=-21.6 StartY=5.7 StartZ=0 EndX=-21.6 EndY=22 EndZ=0
    g4: GeomPoint [constr] X=0 Y=4.6 Z=0
    g5: LineSegment StartX=-20.5 StartY=4.6 StartZ=0 EndX=-21.6 EndY=5.7 EndZ=0
    g6: LineSegment StartX=20.5 StartY=4.6 StartZ=0 EndX=22 EndY=6.1 EndZ=0
    g7: LineSegment StartX=-22 StartY=29 StartZ=0 EndX=-21 EndY=30 EndZ=0
    g8: LineSegment StartX=21 StartY=30 StartZ=0 EndX=22 EndY=29 EndZ=0
    g9: LineSegment StartX=-11.5 StartY=30 StartZ=0 EndX=-11.5 EndY=29.6 EndZ=0
    g10: LineSegment StartX=-11.5 StartY=29.6 StartZ=0 EndX=-4.25 EndY=29.6 EndZ=0
    g11: LineSegment StartX=-4.25 StartY=29.6 StartZ=0 EndX=-4.25 EndY=30 EndZ=0
    g12: LineSegment StartX=4.25 StartY=30 StartZ=0 EndX=4.25 EndY=29.6 EndZ=0
    g13: LineSegment StartX=4.25 StartY=29.6 StartZ=0 EndX=11.5 EndY=29.6 EndZ=0
    g14: LineSegment StartX=11.5 StartY=29.6 StartZ=0 EndX=11.5 EndY=30 EndZ=0
    g15: LineSegment StartX=11.5 StartY=30 StartZ=0 EndX=21 EndY=30 EndZ=0
    g16: LineSegment StartX=-4.25 StartY=30 StartZ=0 EndX=4.25 EndY=30 EndZ=0
    g17: GeomPoint [constr] X=0 Y=30 Z=0
    g18: LineSegment StartX=-21.6 StartY=22 StartZ=0 EndX=-22 EndY=22 EndZ=0
    g19: LineSegment StartX=-22 StartY=22 StartZ=0 EndX=-22 EndY=29 EndZ=0
  constraints (54):
    c: Horizontal(g0)
    c: Horizontal(g2)
    c: Vertical(g1)
    c: Vertical(g3)
    c: PointOnObject(g4,g-2)
    c: Vertical(g9)
    c: Coincident(g10,g9)
    c: Horizontal(g10)
    c: Coincident(g11,g10)
    c: Vertical(g11)
    c: Vertical(g12)
    c: Coincident(g13,g12)
    c: Horizontal(g13)
    c: Coincident(g14,g13)
    c: Vertical(g14)
    c: Coincident(g0,g7)
    c: Coincident(g15,g8)
    c: Coincident(g1,g8)
    c: Coincident(g16,g12)
    c: Coincident(g15,g14)
    c: Tangent(g0,g15)
    c: Coincident(g0,g9)
    c: Coincident(g16,g11)
    c: Tangent(g0,g16)
    c: Coincident(g1,g6)
    c: Coincident(g2,g6)
    c: Coincident(g2,g5)
    c: Coincident(g3,g5)
    c: Symmetric(g2,g2,g4)
    c: PointOnObject(g17,g-2)
    c: Symmetric(g12,g11,g17)
    c: Equal(g13,g10)
    c: Symmetric(g8,g0,g17)
    c: Horizontal(g12,g10)
    c: DistanceX(g16,g16) = 8.5
    c: DistanceX(g2,g2) = 41
    c: DistanceY(g14,g14) = 0.4
    c: DistanceX(g14,g1) = 10.5
    c: DistanceY(g1,g8) = 1
    c: DistanceY(g-1,g2) = 4.6
    c: DistanceY(g-1,g8) = 30
    c: DistanceY(g2,g1) = 1.5
    c: Horizontal(g18)
    c: Coincident(g19,g18)
    c: Vertical(g19)
    c: DistanceX(g8,g1) = 1
    c: Coincident(g3,g18)
    c: Coincident(g7,g19)
    c: Horizontal(g1,g7)
    c: DistanceX(g7,g1) = 44
    c: DistanceX(g7,g0) = 10.5
    c: DistanceY(g18,g0) = 8
    c: DistanceX(g18,g3) = 0.4
    c: Angle(g2,g5) = 2.35619
FEATURE [PartDesign::Pad] Pad
  ClaimChildren = false
  Direction = (1,1,1)
  Fit = 0
  FitJoin = 0
  InnerFit = 0
  InnerFitJoin = 0
  InnerTaperAngle = 0
  InnerTaperAngleRev = 0
  Length = 50.5
  Length2 = 100
  Linearize = true
  Midplane = true
  NewSolid = false
  Placement = pos=(0,0,0) rot=(1,0,0;1.5708rad)
  Profile = -> Sketch
  Refine = true
  Suppress = false
  Type = 0
FEATURE [Sketcher::SketchObject] Sketch001
  ExternalGeometry = -> [Pad]
  FullyConstrained = true
  MapMode = 5
  Placement = pos=(0,1.32e-14,30) rot=(0,0,1;3.14159rad)
  Support = -> [Pad]
  sketch-geometry (4):
    g0: Circle CenterX=-16 CenterY=18 CenterZ=0 NormalX=0 NormalY=0 NormalZ=1 AngleXU=0 Radius=2.5
    g1: Circle CenterX=-16 CenterY=-18 CenterZ=0 NormalX=0 NormalY=0 NormalZ=1 AngleXU=0 Radius=2.5
    g2: Circle CenterX=16 CenterY=18 CenterZ=0 NormalX=0 NormalY=0 NormalZ=1 AngleXU=0 Radius=2.5
    g3: Circle CenterX=16 CenterY=-18 CenterZ=0 NormalX=0 NormalY=0 NormalZ=1 AngleXU=0 Radius=2.5
  constraints (12):
    c: Horizontal(g3,g1)
    c: Vertical(g1,g0)
    c: Vertical(g2,g3)
    c: Horizontal(g0,g2)
    c: DistanceX(g0,g2) = 32
    c: DistanceY(g3,g2) = 36
    c: Equal(g0,g2)
    c: Equal(g2,g3)
    c: Equal(g3,g1)
    c: Symmetric(g0,g3,g-1)
    c: DistanceX(g2,g-3) = 5.6
    c: Diameter(g2) = 5
FEATURE [Sketcher::SketchObject] Sketch002
  ExternalGeometry = -> [Pad]
  FullyConstrained = true
  MapMode = 5
  Placement = pos=(0,0,0) rot=(1,0,0;1.5708rad)
  Support = -> [XZ_Plane]
  sketch-geometry (8):
    g0: LineSegment StartX=-20.6 StartY=29.1 StartZ=0 EndX=20.4 EndY=29.1 EndZ=0
    g1: LineSegment StartX=21.4 StartY=28.1 StartZ=0 EndX=21.4 EndY=5.5 EndZ=0
    g2: LineSegment StartX=20.5 StartY=4.6 StartZ=0 EndX=-20.5 EndY=4.6 EndZ=0
    g3: LineSegment StartX=-21.6 StartY=5.7 StartZ=0 EndX=-21.6 EndY=28.1 EndZ=0
    g4: LineSegment StartX=-21.6 StartY=5.7 StartZ=0 EndX=-20.5 EndY=4.6 EndZ=0
    g5: LineSegment StartX=-21.6 StartY=28.1 StartZ=0 EndX=-20.6 EndY=29.1 EndZ=0
    g6: LineSegment StartX=20.4 StartY=29.1 StartZ=0 EndX=21.4 EndY=28.1 EndZ=0
    g7: LineSegment StartX=20.5 StartY=4.6 StartZ=0 EndX=21.4 EndY=5.5 EndZ=0
  constraints (22):
    c: Horizontal(g0)
    c: Horizontal(g2)
    c: Vertical(g1)
    c: Vertical(g3)
    c: Coincident(g3,g4)
    c: Coincident(g2,g4)
    c: Coincident(g2,g-7)
    c: Coincident(g3,g-7)
    c: Coincident(g0,g5)
    c: Coincident(g3,g5)
    c: Coincident(g0,g6)
    c: Coincident(g1,g6)
    c: Horizontal(g1,g3)
    c: DistanceX(g3,g0) = 1
    c: DistanceY(g3,g0) = 1
    c: DistanceX(g0,g1) = 1
    c: DistanceY(g2,g0) = 24.5
    c: DistanceX(g3,g1) = 43
    c: Coincident(g7,g-5)
    c: PointOnObject(g7,g-5)
    c: Coincident(g1,g7)
    c: PointOnObject(g2,g7)
FEATURE [PartDesign::Pad] Pad001
  BaseFeature = -> Pad
  ClaimChildren = false
  Direction = (1,1,1)
  Fit = 0
  FitJoin = 0
  InnerFit = 0
  InnerFitJoin = 0
  InnerTaperAngle = 0
  InnerTaperAngleRev = 0
  Length = 75.8
  Length2 = 100
  Linearize = true
  Midplane = true
  NewSolid = false
  Placement = pos=(0,0,0) rot=(1,0,0;1.5708rad)
  Profile = -> Sketch002
  Refine = true
  Suppress = false
  Type = 0
FEATURE [Sketcher::SketchObject] Sketch003
  ExternalGeometry = -> [Pad001]
  FullyConstrained = true
  MapMode = 5
  Placement = pos=(0,-37.9,8.3e-15) rot=(1,0,0;1.5708rad)
  Support = -> [Pad001]
  sketch-geometry (14):
    g0: ArcOfCircle CenterX=0 CenterY=24.1 CenterZ=0 NormalX=0 NormalY=0 NormalZ=1 AngleXU=0 Radius=5.25 StartAngle=3.14159 EndAngle=6.28319
    g1: ArcOfCircle CenterX=-19.35 CenterY=15.6 CenterZ=0 NormalX=0 NormalY=0 NormalZ=1 AngleXU=0 Radius=2.75 StartAngle=4.71239 EndAngle=7.85398
    g2: ArcOfCircle CenterX=19.35 CenterY=15.6 CenterZ=0 NormalX=0 NormalY=0 NormalZ=1 AngleXU=0 Radius=2.75 StartAngle=1.5708 EndAngle=4.71239
    g3: LineSegment StartX=-5.25 StartY=24.1 StartZ=0 EndX=-5.25 EndY=29.1 EndZ=0
    g4: LineSegment StartX=5.25 StartY=24.1 StartZ=0 EndX=5.25 EndY=29.1 EndZ=0
    g5: LineSegment StartX=-5.25 StartY=29.1 StartZ=0 EndX=5.25 EndY=29.1 EndZ=0
    g6: LineSegment StartX=-19.35 StartY=18.35 StartZ=0 EndX=-21.6 EndY=18.35 EndZ=0
    g7: LineSegment StartX=-19.35 StartY=12.85 StartZ=0 EndX=-21.6 EndY=12.85 EndZ=0
    g8: LineSegment [constr] StartX=-19.35 StartY=15.6 StartZ=0 EndX=0 EndY=15.6 EndZ=0
    g9: LineSegment [constr] StartX=0 StartY=15.6 StartZ=0 EndX=19.35 EndY=15.6 EndZ=0
    g10: LineSegment StartX=19.35 StartY=18.35 StartZ=0 EndX=21.4 EndY=18.35 EndZ=0
    g11: LineSegment StartX=19.35 StartY=12.85 StartZ=0 EndX=21.4 EndY=12.85 EndZ=0
    g12: LineSegment StartX=-21.6 StartY=18.35 StartZ=0 EndX=-21.6 EndY=12.85 EndZ=0
    g13: LineSegment StartX=21.4 StartY=18.35 StartZ=0 EndX=21.4 EndY=12.85 EndZ=0
  constraints (38):
    c: PointOnObject(g0,g-2)
    c: Horizontal(g1,g2)
    c: Equal(g1,g2)
    c: Diameter(g0) = 10.5
    c: DistanceY(g0,g-3) = 5
    c: PointOnObject(g3,g-3)
    c: Vertical(g3)
    c: PointOnObject(g4,g-3)
    c: Vertical(g4)
    c: Tangent(g0,g3) = 1.5708
    c: Tangent(g0,g4) = -1.5708
    c: Coincident(g5,g3)
    c: Coincident(g5,g4)
    c: PointOnObject(g6,g-4)
    c: Horizontal(g6)
    c: PointOnObject(g7,g-4)
    c: Horizontal(g7)
    c: Diameter(g1) = 5.5
    c: Coincident(g8,g1)
    c: Horizontal(g8)
    c: Coincident(g9,g8)
    c: Coincident(g9,g2)
    c: Equal(g9,g8)
    c: PointOnObject(g10,g-5)
    c: Horizontal(g10)
    c: PointOnObject(g11,g-5)
    c: Horizontal(g11)
    c: DistanceY(g2,g-3) = 13.5
    c: DistanceX(g-4,g1) = 2.25
    c: PointOnObject(g8,g-2)
    c: Tangent(g1,g7) = 1.5708
    c: Tangent(g1,g6) = -1.5708
    c: Tangent(g2,g10) = 1.5708
    c: Tangent(g2,g11) = -1.5708
    c: Coincident(g12,g6)
    c: Coincident(g12,g7)
    c: Coincident(g13,g10)
    c: Coincident(g13,g11)
FEATURE [PartDesign::Pocket] Pocket
  BaseFeature = -> Pad001
  ClaimChildren = false
  Fit = 0
  FitJoin = 0
  InnerFit = 0
  InnerFitJoin = 0
  InnerTaperAngle = 0
  InnerTaperAngleRev = 0
  Length = 1.5
  Length2 = 100
  Linearize = true
  NewSolid = false
  Placement = pos=(0,0,0) rot=(1,0,0;1.5708rad)
  Profile = -> Sketch003
  Refine = true
  Suppress = false
  Type = 0
FEATURE [Sketcher::SketchObject] Sketch004
  ExternalGeometry = -> [Pocket]
  FullyConstrained = true
  MapMode = 5
  Placement = pos=(0,-36.4,2.95e-14) rot=(1,0,0;1.5708rad)
  Support = -> [Pocket]
  sketch-geometry (3):
    g0: Circle CenterX=-19.35 CenterY=15.6 CenterZ=0 NormalX=0 NormalY=0 NormalZ=1 AngleXU=0 Radius=1.25
    g1: Circle CenterX=19.35 CenterY=15.6 CenterZ=0 NormalX=0 NormalY=0 NormalZ=1 AngleXU=0 Radius=1.25
    g2: Circle CenterX=0 CenterY=24.1 CenterZ=0 NormalX=0 NormalY=0 NormalZ=1 AngleXU=0 Radius=2.5
  constraints (6):
    c: Coincident(g0,g-3)
    c: Coincident(g1,g-5)
    c: Coincident(g2,g-4)
    c: Diameter(g2) = 5
    c: Diameter(g1) = 2.5
    c: Equal(g1,g0)
FEATURE [PartDesign::Pocket] Pocket001
  BaseFeature = -> Pocket
  ClaimChildren = false
  Fit = 0
  FitJoin = 0
  InnerFit = 0
  InnerFitJoin = 0
  InnerTaperAngle = 0
  InnerTaperAngleRev = 0
  Length = 8
  Length2 = 100
  Linearize = true
  NewSolid = false
  Placement = pos=(0,0,0) rot=(1,0,0;1.5708rad)
  Profile = -> Sketch004
  Refine = true
  Suppress = false
  Type = 0
FEATURE [PartDesign::Mirrored] Mirrored
  BaseFeature = -> Pocket001
  CopyShape = false
  MirrorPlane = -> XZ_Plane
  NewSolid = false
  OriginalSubs = -> [Pocket001,Pocket]
  Originals = -> [Pocket001,Pocket]
  ParallelTransform = true
  Placement = pos=(0,0,0) rot=(1,0,0;1.5708rad)
  Refine = true
  SubTransform = true
  Suppress = false
  _Version = 1
FEATURE [Sketcher::SketchObject] Sketch005
  FullyConstrained = true
  MapMode = 5
  Placement = pos=(0,0,0) rot=(1,0,0;1.5708rad)
  Support = -> [XZ_Plane001]
  sketch-geometry (1):
    g0: Circle CenterX=0 CenterY=0 CenterZ=0 NormalX=0 NormalY=0 NormalZ=1 AngleXU=0 Radius=3
  constraints (2):
    c: Coincident(g0,g-1)
    c: Radius(g0) = 3
FEATURE [PartDesign::Pad] Pad002
  ClaimChildren = false
  Direction = (1,1,1)
  Fit = 0
  FitJoin = 0
  InnerFit = 0
  InnerFitJoin = 0
  InnerTaperAngle = 0
  InnerTaperAngleRev = 0
  Length = 7
  Length2 = 100
  Linearize = true
  NewSolid = false
  Placement = pos=(0,0,0) rot=(1,0,0;1.5708rad)
  Profile = -> Sketch005
  Refine = true
  Suppress = false
  Type = 0
FEATURE [Sketcher::SketchObject] Sketch006
  FullyConstrained = true
  MapMode = 5
  Placement = pos=(0,0,0) rot=(-1,0,0;1.5708rad)
  Support = -> [Pad002]
  sketch-geometry (7):
    g0: LineSegment StartX=4 StartY=-2.3094 StartZ=0 EndX=4 EndY=2.3094 EndZ=0
    g1: LineSegment StartX=4 StartY=2.3094 StartZ=0 EndX=-4e-16 EndY=4.6188 EndZ=0
    g2: LineSegment StartX=-4e-16 StartY=4.6188 StartZ=0 EndX=-4 EndY=2.3094 EndZ=0
    g3: LineSegment StartX=-4 StartY=2.3094 StartZ=0 EndX=-4 EndY=-2.3094 EndZ=0
    g4: LineSegment StartX=-4 StartY=-2.3094 StartZ=0 EndX=4e-16 EndY=-4.6188 EndZ=0
    g5: LineSegment StartX=4e-16 StartY=-4.6188 StartZ=0 EndX=4 EndY=-2.3094 EndZ=0
    g6: Circle [constr] CenterX=0 CenterY=0 CenterZ=0 NormalX=0 NormalY=0 NormalZ=1 AngleXU=0 Radius=4.6188
  constraints (16):
    c: Coincident(g0,g1)
    c: Coincident(g1,g2)
    c: Coincident(g2,g3)
    c: Coincident(g3,g4)
    c: Coincident(g4,g5)
    c: Coincident(g5,g0)
    c: Equal(g0, g1-g5) x5
    c: PointOnObject(g0,g6)
    c: PointOnObject(g1,g6)
    c: PointOnObject(g2,g6)
    c: PointOnObject(g3,g6)
    c: PointOnObject(g4,g6)
    c: PointOnObject(g5,g6)
    c: Coincident(g6,g-1)
    c: Vertical(g0)
    c: DistanceX(g2,g0) = 8
FEATURE [PartDesign::Pad] Pad003
  BaseFeature = -> Pad002
  ClaimChildren = false
  Direction = (1,1,1)
  Fit = 0
  FitJoin = 0
  InnerFit = 0
  InnerFitJoin = 0
  InnerTaperAngle = 0
  InnerTaperAngleRev = 0
  Length = 3.5
  Length2 = 100
  Linearize = true
  NewSolid = false
  Placement = pos=(0,0,0) rot=(1,0,0;1.5708rad)
  Profile = -> Sketch006
  Refine = true
  Suppress = false
  Type = 0
FEATURE [Sketcher::SketchObject] Sketch007
  FullyConstrained = true
  MapMode = 5
  Placement = pos=(0,3.5,8e-16) rot=(-1,0,0;1.5708rad)
  Support = -> [Pad003]
  sketch-geometry (1):
    g0: Circle CenterX=0 CenterY=0 CenterZ=0 NormalX=0 NormalY=0 NormalZ=1 AngleXU=0 Radius=4
  constraints (2):
    c: Coincident(g0,g-1)
    c: Radius(g0) = 4
FEATURE [PartDesign::Pad] Pad004
  BaseFeature = -> Pad003
  ClaimChildren = false
  Direction = (1,1,1)
  Fit = 0
  FitJoin = 0
  InnerFit = 0
  InnerFitJoin = 0
  InnerTaperAngle = 0
  InnerTaperAngleRev = 0
  Length = 8
  Length2 = 100
  Linearize = true
  NewSolid = false
  Placement = pos=(0,0,0) rot=(1,0,0;1.5708rad)
  Profile = -> Sketch007
  Refine = true
  Suppress = false
  Type = 0
FEATURE [PartDesign::Fillet] Fillet
  Base = -> Pad004 [Edge35]
  BaseFeature = -> Pad004
  NewSolid = false
  Placement = pos=(0,0,0) rot=(1,0,0;1.5708rad)
  Radius = 3
  Refine = true
  SupportTransform = false
  Suppress = false
FEATURE [PartDesign::Plane] DatumPlane
  AttachmentOffset = pos=(0,0,0) rot=(1,0,0;0.785398rad)
  Length = 50
  MapMode = 5
  MinimumLength = 10
  MinimumWidth = 10
  Placement = pos=(0,11.5,3e-15) rot=(-1,0,0;0.785398rad)
  ResizeMode = 0
  Support = -> [Fillet]
  Width = 70.7107
FEATURE [Sketcher::SketchObject] Sketch008
  FullyConstrained = true
  MapMode = 5
  Placement = pos=(0,11.5,3.6e-15) rot=(-1,0,0;0.785398rad)
  Support = -> [DatumPlane]
  sketch-geometry (7):
    g0: LineSegment StartX=3.5 StartY=-4.62073 StartZ=0 EndX=3.5 EndY=-0.579274 EndZ=0
    g1: LineSegment StartX=3.5 StartY=-0.579274 StartZ=0 EndX=8.273e-13 EndY=1.44145 EndZ=0
    g2: LineSegment StartX=8.273e-13 StartY=1.44145 StartZ=0 EndX=-3.5 EndY=-0.579274 EndZ=0
    g3: LineSegment StartX=-3.5 StartY=-0.579274 StartZ=0 EndX=-3.5 EndY=-4.62073 EndZ=0
    g4: LineSegment StartX=-3.5 StartY=-4.62073 StartZ=0 EndX=-8.273e-13 EndY=-6.64145 EndZ=0
    g5: LineSegment StartX=-8.273e-13 StartY=-6.64145 StartZ=0 EndX=3.5 EndY=-4.62073 EndZ=0
    g6: Circle [constr] CenterX=0 CenterY=-2.6 CenterZ=0 NormalX=0 NormalY=0 NormalZ=1 AngleXU=0 Radius=4.04145
  constraints (17):
    c: Coincident(g0,g1)
    c: Coincident(g1,g2)
    c: Coincident(g2,g3)
    c: Coincident(g3,g4)
    c: Coincident(g4,g5)
    c: Coincident(g5,g0)
    c: Equal(g0, g1-g5) x5
    c: PointOnObject(g0,g6)
    c: PointOnObject(g1,g6)
    c: PointOnObject(g2,g6)
    c: PointOnObject(g3,g6)
    c: PointOnObject(g4,g6)
    c: PointOnObject(g5,g6)
    c: PointOnObject(g6,g-2)
    c: Vertical(g0)
    c: DistanceX(g2,g0) = 7
    c: DistanceY(g6,g-1) = 2.6
FEATURE [PartDesign::Pad] Pad005
  BaseFeature = -> Fillet
  ClaimChildren = false
  Direction = (1,1,1)
  Fit = 0
  FitJoin = 0
  InnerFit = 0
  InnerFitJoin = 0
  InnerTaperAngle = 0
  InnerTaperAngleRev = 0
  Length = 2.5
  Length2 = 100
  Linearize = true
  NewSolid = false
  Placement = pos=(0,0,0) rot=(1,0,0;1.5708rad)
  Profile = -> Sketch008
  Refine = true
  Suppress = false
  Type = 0
FEATURE [PartDesign::Plane] DatumPlane001
  AttachmentOffset = pos=(0,0,0) rot=(0,1,0;1.5708rad)
  Length = 70.7107
  MapMode = 5
  MinimumLength = 10
  MinimumWidth = 10
  Placement = pos=(2e-16,7.51777,7.51777) rot=(-0.357407,0.862856,-0.357407;1.71777rad)
  ResizeMode = 0
  Support = -> [Pad005]
  Width = 70.7107
FEATURE [Sketcher::SketchObject] Sketch009
  ExternalGeometry = -> [Pad005]
  FullyConstrained = true
  MapMode = 5
  Placement = pos=(2e-16,7.51777,7.51777) rot=(-0.357407,0.862856,-0.357407;1.71777rad)
  Support = -> [DatumPlane001]
  sketch-geometry (7):
    g0: LineSegment StartX=0 StartY=8.43173 StartZ=0 EndX=-2 EndY=7.78173 EndZ=0
    g1: LineSegment StartX=-4 StartY=8.78173 StartZ=0 EndX=-5.5 EndY=7.78173 EndZ=0
    g2: LineSegment StartX=-5.5 StartY=7.78173 StartZ=0 EndX=-5.5 EndY=5.53173 EndZ=0
    g3: LineSegment StartX=-5.5 StartY=5.53173 StartZ=0 EndX=1.8e-15 EndY=5.53173 EndZ=0
    g4: LineSegment StartX=1.8e-15 StartY=5.53173 StartZ=0 EndX=0 EndY=8.43173 EndZ=0
    g5: LineSegment StartX=-4 StartY=8.78173 StartZ=0 EndX=-3.5 EndY=8.78173 EndZ=0
    g6: LineSegment StartX=-3.5 StartY=8.78173 StartZ=0 EndX=-2 EndY=7.78173 EndZ=0
  constraints (20):
    c: PointOnObject(g0,g-2)
    c: Vertical(g2)
    c: Coincident(g3,g2)
    c: Horizontal(g3)
    c: Coincident(g4,g3)
    c: Coincident(g4,g0)
    c: Symmetric(g-3,g-4,g3)
    c: DistanceY(g4,g4) = 2.9
    c: DistanceX(g3,g3) = 5.5
    c: Coincident(g2,g1)
    c: DistanceX(g1,g1) = 1.5
    c: Coincident(g5,g1)
    c: Coincident(g6,g5)
    c: Coincident(g6,g0)
    c: Horizontal(g5)
    c: DistanceX(g5,g0) = 1.5
    c: Horizontal(g1,g0)
    c: DistanceX(g1,g0) = 3.5
    c: DistanceY(g2,g2) = 2.25
    c: DistanceY(g2,g1) = 3.25
FEATURE [PartDesign::Line] DatumLine
  AttacherType = Attacher::AttachEngineLine
  Length = 70.7107
  MapMode = 29
  MinimumLength = 10
  Placement = pos=(2e-16,11.4293,3.60624) rot=(1,0,0;2.35619rad)
  ResizeMode = 0
  Support = -> [Sketch009]
FEATURE [PartDesign::Revolution] Revolution
  Angle = 360
  Axis = (0,-0.707107,-0.707107)
  Base = (2e-16,11.4293,3.60624)
  BaseFeature = -> Pad005
  ClaimChildren = false
  Fit = 0
  FitJoin = 0
  InnerFit = 0
  InnerFitJoin = 0
  NewSolid = false
  Placement = pos=(0,0,0) rot=(1,0,0;1.5708rad)
  Profile = -> Sketch009
  ReferenceAxis = -> DatumLine
  Refine = true
  Suppress = false
FEATURE [PartDesign::Body] Body001  label="Greaser"
  AutoGroupSolids = false
  ExportMode = 0
  Group = -> [Sketch005,Pad002,Sketch006,Pad003,Sketch007,Pad004,Fillet,DatumPlane,Sketch008,Pad005,DatumPlane001,Sketch009,DatumLine,Revolution]
  Origin = -> Origin001
  Placement = pos=(0.291005,-51,25.9599) rot=(-0.793353,0,0.608761;3.14159rad)
  Tip = -> Revolution
  _ExportChildren = -> [Pad002,Pad003,Pad004,Fillet,DatumPlane,Pad005,DatumPlane001,DatumLine,Revolution]
  _GroupVersion = 1
FEATURE [App::Link] Link001  label="Link001(HGH20CA)"
  AutoLinkLabel = true
  LinkedObject = -> Body
  SyncGroupVisibility = false
  _LinkVersion = 1
FEATURE [App::Link] Link002  label="Link002(Greaser)"
  AutoLinkLabel = true
  LinkPlacement = pos=(-9e-16,36.4,24.1) rot=(0,-1,0;4.45059rad)
  LinkedObject = -> Body001
  Placement = pos=(-9e-16,36.4,24.1) rot=(0,-1,0;4.45059rad)
  SyncGroupVisibility = false
  _LinkVersion = 1
FEATURE [Part::FeaturePython] Screw  label="M6x8-Screw"  # Fasteners workbench fastener (typed FeaturePython)
  Placement = pos=(0,-36.4,24.1) rot=(1,0,0;1.5708rad)
  diameter = 4
  invert = false
  length = 13
  lengthCustom = 8
  matchOuter = false
  offset = 0
  thread = false
  type = 39
FEATURE [Part::FeaturePython] Parts  # WARN: FeaturePython — macro-defined, semantics opaque (R4)
  Group = -> [Link001,Link002,Screw]
  GroupMode = 0
  _LinkVersion = 1
FEATURE [App::Link] Link003  label="Link003(Greaser)"
  AutoLinkLabel = true
  LinkPlacement = pos=(-1e-16,-36.4,24.1) rot=(-0.793353,0,-0.608761;3.14159rad)
  LinkedObject = -> Body001
  Placement = pos=(-1e-16,-36.4,24.1) rot=(-0.793353,0,-0.608761;3.14159rad)
  SyncGroupVisibility = false
  _LinkVersion = 1
FEATURE [App::Link] Link004  label="Link004(HGH20CA)"
  AutoLinkLabel = true
  LinkedObject = -> Body
  SyncGroupVisibility = false
  _LinkVersion = 1
FEATURE [Part::FeaturePython] Screw001  label="M6x8-Screw001"  # Fasteners workbench fastener (typed FeaturePython)
  Placement = pos=(0,36.4,24.1) rot=(-1,0,0;1.5708rad)
  diameter = 4
  invert = false
  length = 13
  lengthCustom = 8
  matchOuter = false
  offset = 0
  thread = false
  type = 39
FEATURE [Part::FeaturePython] Parts001  # WARN: FeaturePython — macro-defined, semantics opaque (R4)
  Group = -> [Link003,Link004,Screw001]
  GroupMode = 0
  _LinkVersion = 1
FEATURE [Sketcher::SketchObject] Sketch010
  FullyConstrained = true
  MapMode = 5
  Placement = pos=(0,0,0) rot=(1,0,0;1.5708rad)
  Support = -> [XZ_Plane]
  sketch-geometry (29):
    g0: LineSegment StartX=-9 StartY=0 StartZ=0 EndX=-10 EndY=1 EndZ=0
    g1: LineSegment StartX=-10 StartY=1 StartZ=0 EndX=-10 EndY=4 EndZ=0
    g2: LineSegment StartX=-10 StartY=4 StartZ=0 EndX=-6.6 EndY=7.45 EndZ=0
    g3: LineSegment StartX=-6.6 StartY=7.45 StartZ=0 EndX=-6.6 EndY=9.95 EndZ=0
    g4: LineSegment StartX=-6.6 StartY=9.95 StartZ=0 EndX=-7.65996 EndY=11.05 EndZ=0
    g5: ArcOfCircle CenterX=-9.8 CenterY=10.8 CenterZ=0 NormalX=0 NormalY=0 NormalZ=1 AngleXU=0 Radius=2.15459 StartAngle=0.116293 EndAngle=1.47784
    g6: LineSegment StartX=-9.6 StartY=12.9453 StartZ=0 EndX=-10 EndY=13.3453 EndZ=0
    g7: LineSegment StartX=-10 StartY=13.3453 StartZ=0 EndX=-10 EndY=14.6953 EndZ=0
    g8: LineSegment StartX=-10 StartY=14.6953 StartZ=0 EndX=-9.6 EndY=15.0953 EndZ=0
    g9: ArcOfCircle CenterX=-9.8 CenterY=17.2406 CenterZ=0 NormalX=0 NormalY=0 NormalZ=1 AngleXU=0 Radius=2.15459 StartAngle=4.80535 EndAngle=6.21789
    g10: LineSegment StartX=-7.65 StartY=17.1 StartZ=0 EndX=-7.25 EndY=17.5 EndZ=0
    g11: LineSegment StartX=-7.25 StartY=17.5 StartZ=0 EndX=0 EndY=17.5 EndZ=0
    g12: LineSegment StartX=0 StartY=17.5 StartZ=0 EndX=7.25 EndY=17.5 EndZ=0
    g13: LineSegment StartX=7.25 StartY=17.5 StartZ=0 EndX=7.65 EndY=17.1 EndZ=0
    g14: ArcOfCircle CenterX=9.8 CenterY=17.2406 CenterZ=0 NormalX=0 NormalY=0 NormalZ=1 AngleXU=0 Radius=2.15459 StartAngle=3.20688 EndAngle=4.61943
    g15: LineSegment StartX=9.6 StartY=15.0953 StartZ=0 EndX=10 EndY=14.6953 EndZ=0
    g16: LineSegment StartX=10 StartY=14.6953 StartZ=0 EndX=10 EndY=13.3453 EndZ=0
    g17: LineSegment StartX=10 StartY=13.3453 StartZ=0 EndX=9.6 EndY=12.9453 EndZ=0
    g18: ArcOfCircle CenterX=9.8 CenterY=10.8 CenterZ=0 NormalX=0 NormalY=0 NormalZ=1 AngleXU=0 Radius=2.15459 StartAngle=1.66376 EndAngle=3.0253
    g19: LineSegment StartX=7.65996 StartY=11.05 StartZ=0 EndX=6.6 EndY=9.95 EndZ=0
    g20: LineSegment StartX=6.6 StartY=9.95 StartZ=0 EndX=6.6 EndY=7.45 EndZ=0
    g21: LineSegment StartX=6.6 StartY=7.45 StartZ=0 EndX=10 EndY=4 EndZ=0
    g22: LineSegment StartX=10 StartY=4 StartZ=0 EndX=10 EndY=1 EndZ=0
    g23: LineSegment StartX=10 StartY=1 StartZ=0 EndX=9 EndY=0 EndZ=0
    g24: LineSegment StartX=-4 StartY=0 StartZ=0 EndX=-4 EndY=0.4 EndZ=0
    g25: LineSegment StartX=-4 StartY=0.4 StartZ=0 EndX=4 EndY=0.4 EndZ=0
    g26: LineSegment StartX=4 StartY=0.4 StartZ=0 EndX=4 EndY=0 EndZ=0
    g27: LineSegment StartX=-9 StartY=0 StartZ=0 EndX=-4 EndY=0 EndZ=0
    g28: LineSegment StartX=4 StartY=0 StartZ=0 EndX=9 EndY=0 EndZ=0
  constraints (89):
    c: Coincident(g0,g1)
    c: Vertical(g1)
    c: Coincident(g1,g2)
    c: Coincident(g2,g3)
    c: Vertical(g3)
    c: Coincident(g3,g4)
    c: Coincident(g5,g4)
    c: Coincident(g6,g5)
    c: Coincident(g6,g7)
    c: Vertical(g7)
    c: Coincident(g7,g8)
    c: Coincident(g9,g8)
    c: Coincident(g9,g10)
    c: Coincident(g10,g11)
    c: PointOnObject(g11,g-2)
    c: Horizontal(g11)
    c: Coincident(g11,g12)
    c: Horizontal(g12)
    c: Coincident(g12,g13)
    c: Coincident(g14,g13)
    c: Coincident(g14,g15)
    c: Coincident(g15,g16)
    c: Coincident(g16,g17)
    c: Coincident(g18,g17)
    c: Coincident(g18,g19)
    c: Coincident(g19,g20)
    c: Vertical(g20)
    c: Coincident(g20,g21)
    c: Coincident(g21,g22)
    c: Vertical(g22)
    c: Coincident(g22,g23)
    c: PointOnObject(g23,g-1)
    c: Equal(g0,g23)
    c: Equal(g22,g1)
    c: Equal(g2,g21)
    c: Equal(g20,g3)
    c: Equal(g4,g19)
    c: Equal(g5,g18)
    c: Equal(g18,g14)
    c: Equal(g14,g9)
    c: Equal(g15,g17)
    c: Vertical(g16)
    c: Equal(g16,g7)
    c: Equal(g10,g13)
    c: Equal(g12,g11)
    c: DistanceX(g10,g12) = 14.5
    c: Horizontal(g22,g0)
    c: DistanceX(g0,g22) = 20
    c: Horizontal(g2,g20)
    c: DistanceX(g0,g23) = 18
    c: DistanceY(g23,g22) = 1
    c: DistanceY(g22,g22) = 3
    c: DistanceX(g2,g20) = 13.2
    c: DistanceY(g21,g20) = 3.45
    c: DistanceY(g20,g20) = 2.5
    c: Horizontal(g18,g5)
    c: Horizontal(g18,g4)
    c: Horizontal(g9,g13)
    c: Horizontal(g9,g14)
    c: Vertical(g9,g5)
    c: DistanceX(g9,g13) = 15.3
    c: DistanceY(g13,g12) = 0.4
    c: Vertical(g15,g21)
    c: Vertical(g7,g1)
    c: Equal(g13,g15)
    c: Equal(g17,g6)
    c: Equal(g6,g8)
    c: DistanceY(g19,g18) = 1.1
    c: DistanceY(g23,g18) = 10.8
    c: DistanceX(g5,g17) = 19.2
    c: DistanceY(g23,g12) = 17.5
    c: DistanceY(g17,g16) = 0.4
    c: DistanceY(g15,g14) = 0.4
    c: DistanceY(g7,g7) = 1.35
    c: DistanceX(g-1,g18) = 9.8
    c: Coincident(g24,g25)
    c: Horizontal(g25)
    c: Coincident(g25,g26)
    c: Vertical(g26)
    c: Vertical(g24)
    c: Symmetric(g26,g24,g-1)
    c: Coincident(g27,g0)
    c: Coincident(g27,g24)
    c: Horizontal(g27)
    c: Coincident(g28,g26)
    c: Coincident(g28,g23)
    c: DistanceX(g25,g25) = 8
    c: DistanceY(g26,g26) = 0.4
    c: Symmetric(g23,g0,g-1)
FEATURE [PartDesign::Pocket] Pocket002
  BaseFeature = -> Mirrored
  ClaimChildren = false
  Fit = 0
  FitJoin = 0
  InnerFit = 0
  InnerFitJoin = 0
  InnerTaperAngle = 0
  InnerTaperAngleRev = 0
  Length = 5
  Length2 = 100
  Linearize = true
  Midplane = true
  NewSolid = false
  Placement = pos=(0,0,0) rot=(1,0,0;1.5708rad)
  Profile = -> Sketch010
  Refine = true
  Suppress = false
  Type = 1
FEATURE [PartDesign::Pocket] Pocket003
  BaseFeature = -> Pocket002
  ClaimChildren = false
  Fit = 0
  FitJoin = 0
  InnerFit = 0
  InnerFitJoin = 0
  InnerTaperAngle = 0
  InnerTaperAngleRev = 0
  Length = 9
  Length2 = 100
  Linearize = true
  NewSolid = false
  Placement = pos=(0,0,0) rot=(1,0,0;1.5708rad)
  Profile = -> Sketch001
  Refine = true
  Suppress = false
  Type = 0
FEATURE [PartDesign::Body] Body  label="HGH20CA"
  AutoGroupSolids = false
  ExportMode = 0
  Group = -> [Sketch,Pad,Sketch001,Sketch002,Pad001,Sketch003,Pocket,Sketch004,Pocket001,Mirrored,Sketch010,Pocket002,Pocket003]
  Origin = -> Origin
  Tip = -> Pocket003
  _ExportChildren = -> [Pad,Pad001,Pocket,Pocket001,Mirrored,Pocket002,Pocket003]
  _GroupVersion = 1
FEATURE [App::DocumentObjectGroup] Group  label="Components"
  ExportMode = 1
  Group = -> [Body,Body001]
  _GroupVersion = 1
FEATURE [Part::FeaturePython] Assembly  label="HGH20CA-L-Assembly"  # WARN: FeaturePython — macro-defined, semantics opaque (R4)
  AutoRelax = true
  BuildShape = 0
  Freeze = false
  Group = -> [Constraints,Elements,Parts]
  Placement = pos=(0,54,-7.15256e-07) rot=(0,0,1;0rad)
  Verbose = false
  _LinkVersion = 1
  _SolverType = 1
  _Version = 1
FEATURE [App::FeaturePython] Constraints  # WARN: FeaturePython — macro-defined, semantics opaque (R4)
  Group = -> [Constraint,Constraint001,Constraint002]
  _LinkVersion = 1
  _Version = 1
FEATURE [App::FeaturePython] Elements  # WARN: FeaturePython — macro-defined, semantics opaque (R4)
  Group = -> [_Element,_Element001,_Element002,_Element003,_Element004,Element004]
  _LinkVersion = 1
FEATURE [App::FeaturePython] Constraint  label="Locked"  # WARN: FeaturePython — macro-defined, semantics opaque (R4)
  Disabled = false
  Group = -> [ElementLink]
  _ConstraintType = 0
  _LinkVersion = 1
  _Parent = -> Constraints
FEATURE [App::FeaturePython] ElementLink  label="_Element"  # link proxy (typed FeaturePython)
  LinkTransform = true
  LinkedObject = -> _Element
  _LinkVersion = 1
  _Parent = -> Constraint
FEATURE [Part::FeaturePython] _Element  # link proxy (typed FeaturePython)
  Detach = false
  LinkTransform = true
  LinkedObject = -> Link001 [Pocket003.Face62]
  _LinkVersion = 1
  _Parent = -> Elements
FEATURE [App::FeaturePython] Constraint001  label="Attachment"  # WARN: FeaturePython — macro-defined, semantics opaque (R4)
  Cascade = false
  Disabled = false
  Group = -> [ElementLink001,ElementLink002]
  Multiply = false
  _ConstraintType = 45
  _LinkVersion = 1
  _Parent = -> Constraints
FEATURE [App::FeaturePython] ElementLink001  label="_Element001"  # link proxy (typed FeaturePython)
  LinkTransform = true
  LinkedObject = -> _Element001
  Offset = pos=(0,0,0) rot=(0,0,1;1.8326rad)
  Placement = pos=(23.2788,-2.84e-14,30.3375) rot=(0,-1,0;1.8326rad)
  _LinkVersion = 1
  _Parent = -> Constraint001
FEATURE [Part::FeaturePython] _Element001  # link proxy (typed FeaturePython)
  Detach = false
  LinkTransform = true
  LinkedObject = -> Link002 [Revolution.Edge59]
  _LinkVersion = 1
  _Parent = -> Elements
FEATURE [App::FeaturePython] ElementLink002  label="_Element002"  # link proxy (typed FeaturePython)
  LinkTransform = true
  LinkedObject = -> _Element002
  _LinkVersion = 1
  _Parent = -> Constraint001
FEATURE [Part::FeaturePython] _Element002  # link proxy (typed FeaturePython)
  Detach = false
  LinkTransform = true
  LinkedObject = -> Link001 [Pocket003.Edge186]
  _LinkVersion = 1
  _Parent = -> Elements
FEATURE [App::FeaturePython] Constraint002  label="Attachment001"  # WARN: FeaturePython — macro-defined, semantics opaque (R4)
  Cascade = false
  Disabled = false
  Group = -> [ElementLink003,ElementLink004]
  Multiply = false
  _ConstraintType = 45
  _LinkVersion = 1
  _Parent = -> Constraints
FEATURE [App::FeaturePython] ElementLink003  label="_Element003"  # link proxy (typed FeaturePython)
  LinkTransform = true
  LinkedObject = -> _Element003
  _LinkVersion = 1
  _Parent = -> Constraint002
FEATURE [Part::FeaturePython] _Element003  # link proxy (typed FeaturePython)
  Detach = false
  LinkTransform = true
  LinkedObject = -> Screw [Edge4]
  _LinkVersion = 1
  _Parent = -> Elements
FEATURE [App::FeaturePython] ElementLink004  label="_Element004"  # link proxy (typed FeaturePython)
  LinkTransform = true
  LinkedObject = -> _Element004
  _LinkVersion = 1
  _Parent = -> Constraint002
FEATURE [Part::FeaturePython] _Element004  # link proxy (typed FeaturePython)
  Detach = false
  LinkTransform = true
  LinkedObject = -> Link001 [Pocket003.Edge234]
  _LinkVersion = 1
  _Parent = -> Elements
FEATURE [Part::FeaturePython] Assembly001  label="HGH20CA-R-Assembly"  # WARN: FeaturePython — macro-defined, semantics opaque (R4)
  AutoRelax = true
  BuildShape = 0
  Freeze = false
  Group = -> [Constraints001,Elements001,Parts001]
  Placement = pos=(0,-36,-7.15256e-07) rot=(0,0,1;0rad)
  Verbose = false
  _LinkVersion = 1
  _SolverType = 1
  _Version = 1
FEATURE [App::FeaturePython] Constraints001  # WARN: FeaturePython — macro-defined, semantics opaque (R4)
  Group = -> [Constraint003,Constraint004,Constraint005]
  _LinkVersion = 1
  _Version = 1
FEATURE [App::FeaturePython] Elements001  # WARN: FeaturePython — macro-defined, semantics opaque (R4)
  Group = -> [_Element005,_Element006,_Element007,_Element008,_Element009,Element,Element001,Element002,Element003]
  _LinkVersion = 1
FEATURE [App::FeaturePython] Constraint003  label="Locked001"  # WARN: FeaturePython — macro-defined, semantics opaque (R4)
  Disabled = false
  Group = -> [ElementLink005]
  _ConstraintType = 0
  _LinkVersion = 1
  _Parent = -> Constraints001
FEATURE [App::FeaturePython] ElementLink005  label="_Element005"  # link proxy (typed FeaturePython)
  LinkTransform = true
  LinkedObject = -> _Element005
  _LinkVersion = 1
  _Parent = -> Constraint003
FEATURE [Part::FeaturePython] _Element005  # link proxy (typed FeaturePython)
  Detach = false
  LinkTransform = true
  LinkedObject = -> Link004 [Pocket003.Face62]
  _LinkVersion = 1
  _Parent = -> Elements001
FEATURE [App::FeaturePython] Constraint004  label="Attachment002"  # WARN: FeaturePython — macro-defined, semantics opaque (R4)
  Cascade = false
  Disabled = false
  Group = -> [ElementLink006,ElementLink007]
  Multiply = false
  _ConstraintType = 45
  _LinkVersion = 1
  _Parent = -> Constraints001
FEATURE [App::FeaturePython] ElementLink006  label="_Element006"  # link proxy (typed FeaturePython)
  LinkTransform = true
  LinkedObject = -> _Element006
  Offset = pos=(0,0,0) rot=(1,0,0;3.14159rad)
  Placement = pos=(0,-72.8,48.2) rot=(1,0,0;3.14159rad)
  _LinkVersion = 1
  _Parent = -> Constraint004
FEATURE [Part::FeaturePython] _Element006  # link proxy (typed FeaturePython)
  Detach = false
  LinkTransform = true
  LinkedObject = -> Link004 [Pocket003.Edge234]
  _LinkVersion = 1
  _Parent = -> Elements001
FEATURE [App::FeaturePython] ElementLink007  label="_Element007"  # link proxy (typed FeaturePython)
  LinkTransform = true
  LinkedObject = -> _Element007
  Offset = pos=(0,0,0) rot=(0,0,1;1.309rad)
  Placement = pos=(-23.2788,2.13e-14,17.8625) rot=(0,1,0;1.309rad)
  _LinkVersion = 1
  _Parent = -> Constraint004
FEATURE [Part::FeaturePython] _Element007  # link proxy (typed FeaturePython)
  Detach = false
  LinkTransform = true
  LinkedObject = -> Link003 [Revolution.Edge59]
  _LinkVersion = 1
  _Parent = -> Elements001
FEATURE [App::FeaturePython] Constraint005  label="Attachment003"  # WARN: FeaturePython — macro-defined, semantics opaque (R4)
  Cascade = false
  Disabled = false
  Group = -> [ElementLink008,ElementLink009]
  Multiply = false
  _ConstraintType = 45
  _LinkVersion = 1
  _Parent = -> Constraints001
FEATURE [App::FeaturePython] ElementLink008  label="_Element008"  # link proxy (typed FeaturePython)
  LinkTransform = true
  LinkedObject = -> _Element008
  Offset = pos=(0,0,0) rot=(1,0,0;3.14159rad)
  Placement = pos=(0,72.8,48.2) rot=(1,0,0;3.14159rad)
  _LinkVersion = 1
  _Parent = -> Constraint005
FEATURE [Part::FeaturePython] _Element008  # link proxy (typed FeaturePython)
  Detach = false
  LinkTransform = true
  LinkedObject = -> Link004 [Pocket003.Edge186]
  _LinkVersion = 1
  _Parent = -> Elements001
FEATURE [App::FeaturePython] ElementLink009  label="_Element009"  # link proxy (typed FeaturePython)
  LinkTransform = true
  LinkedObject = -> _Element009
  _LinkVersion = 1
  _Parent = -> Constraint005
FEATURE [Part::FeaturePython] _Element009  # link proxy (typed FeaturePython)
  Detach = false
  LinkTransform = true
  LinkedObject = -> Screw001 [Edge4]
  _LinkVersion = 1
  _Parent = -> Elements001
FEATURE [App::DocumentObjectGroup] Group001  label="Assemblies"
  ExportMode = 1
  Group = -> [Assembly,Assembly001]
  _GroupVersion = 1
FEATURE [Part::FeaturePython] Element  label="top-mate"  # link proxy (typed FeaturePython)
  Detach = false
  LinkTransform = true
  LinkedObject = -> Link004 [Pocket003.Face13]
  _LinkVersion = 1
  _Parent = -> Elements001
FEATURE [Part::FeaturePython] Element001  label="side-mate"  # link proxy (typed FeaturePython)
  Detach = false
  LinkTransform = true
  LinkedObject = -> Link004 [Pocket003.Face17]
  _LinkVersion = 1
  _Parent = -> Elements001
FEATURE [Part::FeaturePython] Element002  label="point"  # link proxy (typed FeaturePython)
  Detach = false
  LinkTransform = true
  LinkedObject = -> Link004 [Pocket003.Vertex56]
  _LinkVersion = 1
  _Parent = -> Elements001
FEATURE [Part::FeaturePython] Element003  label="shim-br"  # link proxy (typed FeaturePython)
  Detach = false
  LinkTransform = true
  LinkedObject = -> Link004 [Pocket003.Edge212]
  _LinkVersion = 1
  _Parent = -> Elements001
FEATURE [Part::FeaturePython] Element004  label="shim-tr"  # link proxy (typed FeaturePython)
  Detach = false
  LinkTransform = true
  LinkedObject = -> Link001 [Pocket003.Edge213]
  _LinkVersion = 1
  _Parent = -> Elements
---- part parts/HGR20.FCStd = doc fcstd_98294569bf8e (65349 chars; too large to inline — full recipe in that document) ----
---- part parts/LimitSensor.FCStd = doc fcstd_3f7c24fee6a1 ----
FCSTD DOCUMENT  (FreeCAD 2021.717R24301 +3842 (Git))
Label: LimitSensor
License: Creative Commons Attribution
LicenseURL: http://creativecommons.org/licenses/by/4.0/
objects: App::FeaturePython×10, Part::FeaturePython×8, Sketcher::SketchObject×6, PartDesign::Pocket×4, App::Link×2, App::DocumentObjectGroup×2, App::LinkElement×2, PartDesign::Pad×1, PartDesign::Mirrored×1, PartDesign::Body×1
note: 32 computed .brp shape members not serialized (recipe doc carries the construction recipe); baked Part::Feature solids carry a one-line shape summary decoded from their .brp

FEATURE [Sketcher::SketchObject] Sketch
  FullyConstrained = true
  MapMode = 5
  Placement = pos=(0,0,0) rot=(1,0,0;1.5708rad)
  Support = -> [XZ_Plane]
  sketch-geometry (4):
    g0: LineSegment StartX=-9 StartY=15.25 StartZ=0 EndX=9 EndY=15.25 EndZ=0
    g1: LineSegment StartX=9 StartY=15.25 StartZ=0 EndX=9 EndY=-15.25 EndZ=0
    g2: LineSegment StartX=9 StartY=-15.25 StartZ=0 EndX=-9 EndY=-15.25 EndZ=0
    g3: LineSegment StartX=-9 StartY=-15.25 StartZ=0 EndX=-9 EndY=15.25 EndZ=0
  constraints (11):
    c: Coincident(g0,g1)
    c: Coincident(g1,g2)
    c: Coincident(g2,g3)
    c: Coincident(g3,g0)
    c: Horizontal(g0)
    c: Horizontal(g2)
    c: Vertical(g1)
    c: Vertical(g3)
    c: Symmetric(g1,g0,g-1)
    c: DistanceX(g0,g0) = 18
    c: DistanceY(g1,g1) = 30.5
FEATURE [PartDesign::Pad] Pad
  ClaimChildren = false
  Direction = (1,1,1)
  Fit = 0
  FitJoin = 0
  InnerFit = 0
  InnerFitJoin = 0
  InnerTaperAngle = 0
  InnerTaperAngleRev = 0
  Length = 10
  Length2 = 100
  Linearize = true
  NewSolid = false
  Placement = pos=(0,0,0) rot=(1,0,0;1.5708rad)
  Profile = -> Sketch
  Refine = true
  Suppress = false
  Type = 0
  _ProfileBasedVersion = 1
FEATURE [Sketcher::SketchObject] Sketch001
  FullyConstrained = true
  MapMode = 5
  Placement = pos=(0,-10,2.2e-15) rot=(1,0,0;1.5708rad)
  Support = -> [Pad]
  sketch-geometry (4):
    g0: LineSegment StartX=-9 StartY=15.25 StartZ=0 EndX=9 EndY=15.25 EndZ=0
    g1: LineSegment StartX=9 StartY=15.25 StartZ=0 EndX=9 EndY=7 EndZ=0
    g2: LineSegment StartX=9 StartY=7 StartZ=0 EndX=-9 EndY=7 EndZ=0
    g3: LineSegment StartX=-9 StartY=7 StartZ=0 EndX=-9 EndY=15.25 EndZ=0
  constraints (11):
    c: Coincident(g0,g1)
    c: Coincident(g1,g2)
    c: Coincident(g2,g3)
    c: Coincident(g3,g0)
    c: Horizontal(g0)
    c: Vertical(g1)
    c: Vertical(g3)
    c: Symmetric(g1,g2,g-2)
    c: DistanceX(g0,g0) = 18
    c: DistanceY(g1,g1) = 8.25
    c: DistanceY(g-1,g1) = 7
FEATURE [PartDesign::Pocket] Pocket
  BaseFeature = -> Pad
  ClaimChildren = false
  Fit = 0
  FitJoin = 0
  InnerFit = 0
  InnerFitJoin = 0
  InnerTaperAngle = 0
  InnerTaperAngleRev = 0
  Length = 2
  Length2 = 100
  Linearize = true
  NewSolid = false
  Placement = pos=(0,0,0) rot=(1,0,0;1.5708rad)
  Profile = -> Sketch001
  Refine = true
  Suppress = false
  Type = 0
  _ProfileBasedVersion = 1
FEATURE [Sketcher::SketchObject] Sketch002
  FullyConstrained = true
  MapMode = 5
  Placement = pos=(0,-8,6.9e-15) rot=(1,0,0;1.5708rad)
  Support = -> [Pocket]
  sketch-geometry (4):
    g0: ArcOfCircle CenterX=-6 CenterY=11.25 CenterZ=0 NormalX=0 NormalY=0 NormalZ=1 AngleXU=0 Radius=1.75 StartAngle=0 EndAngle=3.14159
    g1: ArcOfCircle CenterX=-6 CenterY=9.75 CenterZ=0 NormalX=0 NormalY=0 NormalZ=1 AngleXU=0 Radius=1.75 StartAngle=3.14159 EndAngle=6.28319
    g2: LineSegment StartX=-7.75 StartY=11.25 StartZ=0 EndX=-7.75 EndY=9.75 EndZ=0
    g3: LineSegment StartX=-4.25 StartY=11.25 StartZ=0 EndX=-4.25 EndY=9.75 EndZ=0
  constraints (10):
    c: Tangent(g0,g3) = 1.5708
    c: Tangent(g0,g2) = -1.5708
    c: Tangent(g2,g1) = -1.5708
    c: Tangent(g3,g1) = 1.5708
    c: Vertical(g2)
    c: Equal(g0,g1)
    c: DistanceY(g3,g3) = 1.5
    c: Diameter(g0) = 3.5
    c: DistanceY(g-1,g0) = 11.25
    c: DistanceX(g0,g-1) = 6
FEATURE [PartDesign::Pocket] Pocket001
  BaseFeature = -> Pocket
  ClaimChildren = false
  Fit = 0
  FitJoin = 0
  InnerFit = 0
  InnerFitJoin = 0
  InnerTaperAngle = 0
  InnerTaperAngleRev = 0
  Length = 5
  Length2 = 100
  Linearize = true
  NewSolid = false
  Placement = pos=(0,0,0) rot=(1,0,0;1.5708rad)
  Profile = -> Sketch002
  Refine = true
  Suppress = false
  Type = 1
  _ProfileBasedVersion = 1
FEATURE [Sketcher::SketchObject] Sketch003
  ExternalGeometry = -> [Pocket001]
  FullyConstrained = true
  MapMode = 5
  Placement = pos=(0,-8,6.9e-15) rot=(1,0,0;1.5708rad)
  Support = -> [Pocket001]
  sketch-geometry (6):
    g0: LineSegment StartX=-9 StartY=15.25 StartZ=0 EndX=-2 EndY=15.25 EndZ=0
    g1: LineSegment StartX=-2 StartY=15.25 StartZ=0 EndX=-2 EndY=9 EndZ=0
    g2: LineSegment StartX=-4 StartY=7 StartZ=0 EndX=-9 EndY=7 EndZ=0
    g3: LineSegment StartX=-9 StartY=7 StartZ=0 EndX=-9 EndY=15.25 EndZ=0
    g4: ArcOfCircle CenterX=-4 CenterY=9 CenterZ=0 NormalX=0 NormalY=0 NormalZ=1 AngleXU=0 Radius=2 StartAngle=4.71239 EndAngle=6.28319
    g5: GeomPoint [constr] X=-2 Y=7 Z=0
  constraints (16):
    c: Coincident(g0,g1)
    c: Coincident(g2,g3)
    c: Coincident(g3,g0)
    c: Horizontal(g0)
    c: Horizontal(g2)
    c: Vertical(g1)
    c: Vertical(g3)
    c: DistanceX(g2,g-1) = 9
    c: DistanceY(g-1,g0) = 15.25
    c: Horizontal(g-3,g2)
    c: DistanceX(g0,g0) = 7
    c: PointOnObject(g5,g1)
    c: PointOnObject(g5,g2)
    c: Tangent(g1,g4) = 1.5708
    c: Tangent(g2,g4) = 1.5708
    c: Radius(g4) = 2
FEATURE [PartDesign::Pocket] Pocket002
  BaseFeature = -> Pocket001
  ClaimChildren = false
  Fit = 0
  FitJoin = 0
  InnerFit = 0
  InnerFitJoin = 0
  InnerTaperAngle = 0
  InnerTaperAngleRev = 0
  Length = 1.5
  Length2 = 100
  Linearize = true
  NewSolid = false
  Placement = pos=(0,0,0) rot=(1,0,0;1.5708rad)
  Profile = -> Sketch003
  Refine = true
  Suppress = false
  Type = 0
  _ProfileBasedVersion = 1
FEATURE [PartDesign::Mirrored] Mirrored
  BaseFeature = -> Pocket002
  CopyShape = false
  MirrorPlane = -> Sketch003 [V_Axis]
  NewSolid = false
  OriginalSubs = -> [Pocket002,Pocket001]
  Originals = -> [Pocket002,Pocket001]
  ParallelTransform = true
  Placement = pos=(0,0,0) rot=(1,0,0;1.5708rad)
  Refine = true
  SubTransform = true
  Suppress = false
  _Version = 2
FEATURE [Sketcher::SketchObject] Sketch004
  FullyConstrained = false
  MapMode = 5
  Placement = pos=(0,-10,2.2e-15) rot=(1,0,0;1.5708rad)
  Support = -> [Mirrored]
  sketch-geometry (30):
    g0: LineSegment StartX=-7.75 StartY=5.75 StartZ=0 EndX=7.75 EndY=5.75 EndZ=0
    g1: LineSegment StartX=7.75 StartY=5.75 StartZ=0 EndX=7.75 EndY=0.25 EndZ=0
    g2: LineSegment StartX=7.75 StartY=0.25 StartZ=0 EndX=-7.75 EndY=0.25 EndZ=0
    g3: LineSegment StartX=-7.75 StartY=0.25 StartZ=0 EndX=-7.75 EndY=5.75 EndZ=0
    g4: Circle CenterX=0 CenterY=-7 CenterZ=0 NormalX=0 NormalY=0 NormalZ=1 AngleXU=0 Radius=6
    g5: ArcOfCircle CenterX=0 CenterY=-7 CenterZ=0 NormalX=0 NormalY=0 NormalZ=1 AngleXU=0 Radius=5.5 StartAngle=3.18706 EndAngle=4.66692
    g6: ArcOfCircle CenterX=0 CenterY=-7 CenterZ=0 NormalX=0 NormalY=0 NormalZ=1 AngleXU=0 Radius=3.175 StartAngle=3.22041 EndAngle=4.63357
    g7: ArcOfCircle CenterX=0 CenterY=-7 CenterZ=0 NormalX=0 NormalY=0 NormalZ=1 AngleXU=0 Radius=2.675 StartAngle=3.23519 EndAngle=4.61879
    g8: LineSegment StartX=-5.49432 StartY=-6.75 StartZ=0 EndX=-3.16514 EndY=-6.75 EndZ=0
    g9: LineSegment StartX=-5.49432 StartY=-7.25 StartZ=0 EndX=-3.16514 EndY=-7.25 EndZ=0
    g10: LineSegment StartX=0.25 StartY=-1.50568 StartZ=0 EndX=0.25 EndY=-3.83486 EndZ=0
    g11: LineSegment StartX=-0.25 StartY=-1.50568 StartZ=0 EndX=-0.25 EndY=-3.83486 EndZ=0
    g12: LineSegment [constr] StartX=-7.32001 StartY=-7 StartZ=0 EndX=7.24789 EndY=-7 EndZ=0
    g13: ArcOfCircle CenterX=0 CenterY=-7 CenterZ=0 NormalX=0 NormalY=0 NormalZ=1 AngleXU=0 Radius=2.675 StartAngle=0.0935945 EndAngle=1.4772
    g14: ArcOfCircle CenterX=0 CenterY=-7 CenterZ=0 NormalX=0 NormalY=0 NormalZ=1 AngleXU=0 Radius=3.175 StartAngle=0.0788218 EndAngle=1.49197
    g15: ArcOfCircle CenterX=0 CenterY=-7 CenterZ=0 NormalX=0 NormalY=0 NormalZ=1 AngleXU=0 Radius=5.5 StartAngle=0.0454702 EndAngle=1.52533
    g16: LineSegment StartX=3.16514 StartY=-7.25 StartZ=0 EndX=5.49432 EndY=-7.25 EndZ=0
    g17: LineSegment StartX=3.16514 StartY=-6.75 StartZ=0 EndX=5.49432 EndY=-6.75 EndZ=0
    g18: LineSegment StartX=-2.66329 StartY=-6.75 StartZ=0 EndX=2.66329 EndY=-6.75 EndZ=0
    g19: LineSegment StartX=-2.66329 StartY=-7.25 StartZ=0 EndX=2.66329 EndY=-7.25 EndZ=0
    g20: LineSegment StartX=-0.25 StartY=-4.33671 StartZ=0 EndX=-0.25 EndY=-9.66329 EndZ=0
    g21: LineSegment StartX=0.25 StartY=-4.33671 StartZ=0 EndX=0.25 EndY=-9.66329 EndZ=0
    g22: ArcOfCircle CenterX=0 CenterY=-7 CenterZ=0 NormalX=0 NormalY=0 NormalZ=1 AngleXU=0 Radius=2.675 StartAngle=1.66439 EndAngle=3.048
    g23: ArcOfCircle CenterX=0 CenterY=-7 CenterZ=0 NormalX=0 NormalY=0 NormalZ=1 AngleXU=0 Radius=2.675 StartAngle=4.80598 EndAngle=6.18959
    g24: ArcOfCircle CenterX=0 CenterY=-7 CenterZ=0 NormalX=0 NormalY=0 NormalZ=1 AngleXU=0 Radius=3.175 StartAngle=4.79121 EndAngle=6.20436
    g25: LineSegment StartX=0.25 StartY=-10.1651 StartZ=0 EndX=0.25 EndY=-12.4943 EndZ=0
    g26: LineSegment StartX=-0.25 StartY=-10.1651 StartZ=0 EndX=-0.25 EndY=-12.4943 EndZ=0
    g27: ArcOfCircle CenterX=0 CenterY=-7 CenterZ=0 NormalX=0 NormalY=0 NormalZ=1 AngleXU=0 Radius=5.5 StartAngle=4.75786 EndAngle=6.23772
    g28: ArcOfCircle CenterX=0 CenterY=-7 CenterZ=0 NormalX=0 NormalY=0 NormalZ=1 AngleXU=0 Radius=5.5 StartAngle=1.61627 EndAngle=3.09612
    g29: ArcOfCircle CenterX=0 CenterY=-7 CenterZ=0 NormalX=0 NormalY=0 NormalZ=1 AngleXU=0 Radius=3.175 StartAngle=1.64962 EndAngle=3.06277
  constraints (80):
    c: Coincident(g0,g1)
    c: Coincident(g1,g2)
    c: Coincident(g2,g3)
    c: Coincident(g3,g0)
    c: Horizontal(g2)
    c: Vertical(g1)
    c: Vertical(g3)
    c: Symmetric(g0,g0,g-2)
    c: DistanceX(g0,g0) = 15.5
    c: DistanceY(g1,g1) = 5.5
    c: PointOnObject(g4,g-2)
    c: Coincident(g5,g4)
    c: Coincident(g6,g4)
    c: Coincident(g7,g4)
    c: Diameter(g7) = 5.35
    c: Diameter(g6) = 6.35
    c: Diameter(g5) = 11
    c: Diameter(g4) = 12
    c: Horizontal(g8)
    c: Horizontal(g9)
    c: PointOnObject(g10,g5)
    c: Vertical(g10)
    c: Vertical(g11)
    c: Symmetric(g11,g10,g-2)
    c: DistanceX(g11,g10) = 0.5
    c: Horizontal(g12)
    c: Symmetric(g17,g16,g12)
    c: DistanceY(g16,g17) = 0.5
    c: Coincident(g28,g8)
    c: Coincident(g5,g9)
    c: Equal(g7,g13)
    c: Coincident(g7,g13)
    c: Equal(g6,g14)
    c: Coincident(g6,g14)
    c: Equal(g5,g15)
    c: Coincident(g15,g17)
    c: Coincident(g5,g15)
    c: Coincident(g27,g16)
    c: Coincident(g19,g23)
    c: Coincident(g16,g24)
    c: Tangent(g9,g16)
    c: Coincident(g18,g13)
    c: Coincident(g17,g14)
    c: Tangent(g8,g17)
    c: Coincident(g8,g29)
    c: Coincident(g18,g22)
    c: Tangent(g8,g18)
    c: Coincident(g9,g6)
    c: Coincident(g19,g7)
    c: Tangent(g9,g19)
    c: Tangent(g11,g20)
    c: Tangent(g10,g21)
    c: Equal(g13,g22)
    c: Coincident(g13,g21)
    c: Coincident(g22,g20)
    c: Coincident(g13,g22)
    c: Equal(g7,g23)
    c: Coincident(g7,g23)
    c: Equal(g6,g24)
    c: Coincident(g6,g24)
    c: Coincident(g21,g23)
    c: Coincident(g25,g24)
    c: Tangent(g21,g25)
    c: Coincident(g20,g7)
    c: Coincident(g26,g6)
    c: Tangent(g20,g26)
    c: Equal(g5,g27)
    c: Coincident(g5,g26)
    c: Coincident(g27,g25)
    c: Coincident(g5,g27)
    c: Equal(g15,g28)
    c: PointOnObject(g15,g10)
    c: PointOnObject(g28,g11)
    c: Coincident(g15,g28)
    c: DistanceY(g4,g-1) = 7
    c: DistanceY(g-1,g1) = 0.25
    c: Equal(g14,g29)
    c: Coincident(g14,g10)
    c: Coincident(g29,g11)
    c: Coincident(g14,g29)
FEATURE [PartDesign::Pocket] Pocket003
  BaseFeature = -> Mirrored
  ClaimChildren = false
  Fit = 0
  FitJoin = 0
  InnerFit = 0
  InnerFitJoin = 0
  InnerTaperAngle = 0
  InnerTaperAngleRev = 0
  Length = 0.2
  Length2 = 100
  Linearize = true
  NewSolid = false
  Placement = pos=(0,0,0) rot=(1,0,0;1.5708rad)
  Profile = -> Sketch004
  Refine = true
  Suppress = false
  Type = 0
  _ProfileBasedVersion = 1
FEATURE [App::Link] Link  label="Link(Limit sensor)"
  AutoLinkLabel = true
  AutoPlacement = true
  LinkedObject = -> Body
  SyncGroupVisibility = false
  _LinkVersion = 1
FEATURE [Sketcher::SketchObject] Sketch005
  ExternalGeometry = -> [Pocket003]
  FullyConstrained = true
  MapMode = 5
  Placement = pos=(0,0,0) rot=(-1,0,0;1.5708rad)
  Support = -> [Pocket003]
  sketch-geometry (2):
    g0: Circle CenterX=-6 CenterY=-10.5 CenterZ=0 NormalX=0 NormalY=0 NormalZ=1 AngleXU=0 Radius=1.5
    g1: Circle CenterX=6 CenterY=-10.5 CenterZ=0 NormalX=0 NormalY=0 NormalZ=1 AngleXU=0 Radius=1.5
  constraints (4):
    c: Symmetric(g-3,g-4,g0)
    c: Symmetric(g-5,g-6,g1)
    c: Equal(g1,g0)
    c: Diameter(g1) = 3
FEATURE [PartDesign::Body] Body  label="Limit sensor"
  AutoGroupSolids = false
  ExportMode = 0
  Group = -> [Sketch,Pad,Sketch001,Pocket,Sketch002,Pocket001,Sketch003,Pocket002,Mirrored,Sketch004,Pocket003,Sketch005]
  Origin = -> Origin
  Tip = -> Pocket003
  _ExportChildren = -> [Pad,Pocket,Pocket001,Pocket002,Mirrored,Pocket003,Sketch005]
  _GroupVersion = 1
FEATURE [Part::FeaturePython] Screw  label="M3x12-Screw"  # Fasteners workbench fastener (typed FeaturePython)
  Placement = pos=(15,-17,-3.8e-15) rot=(1,0,0;1.5708rad)
  diameter = 4
  invert = false
  length = 10
  lengthCustom = 12
  matchOuter = false
  offset = 0
  thread = false
  type = 33
FEATURE [App::DocumentObjectGroup] Group  label="Components"
  ExportMode = 1
  Group = -> [Body,Screw]
  _GroupVersion = 1
FEATURE [App::LinkElement] Link001_i0
  LinkPlacement = pos=(-9,10.5,-10.5) rot=(0,0,1;0rad)
  LinkedObject = -> Screw
  Placement = pos=(-9,10.5,-10.5) rot=(0,0,1;0rad)
  _LinkVersion = 0
FEATURE [App::LinkElement] Link001_i1
  LinkPlacement = pos=(-21,10.5,-10.5) rot=(0,0,1;0rad)
  LinkedObject = -> Screw
  Placement = pos=(-21,10.5,-10.5) rot=(0,0,1;0rad)
  _LinkVersion = 0
FEATURE [App::Link] Link001  label="M3x12-Screw 2pc"
  AutoLinkLabel = true
  AutoPlacement = true
  ElementCount = 2
  ElementList = -> [Link001_i0,Link001_i1]
  LinkPlacement = pos=(15,-17,-3.8e-15) rot=(1,0,0;1.5708rad)
  LinkedObject = -> Screw
  Placement = pos=(15,-17,-3.8e-15) rot=(1,0,0;1.5708rad)
  SyncGroupVisibility = false
  _LinkVersion = 1
FEATURE [Part::FeaturePython] Parts  # WARN: FeaturePython — macro-defined, semantics opaque (R4)
  Group = -> [Link,Link001]
  GroupMode = 0
  _LinkVersion = 1
FEATURE [App::DocumentObjectGroup] Group001  label="Assemblies"
  ExportMode = 1
  Group = -> [Assembly]
  _GroupVersion = 1
FEATURE [Part::FeaturePython] Assembly  label="Limit sensor Assembly"  # WARN: FeaturePython — macro-defined, semantics opaque (R4)
  AutoRelax = true
  BuildShape = 0
  Freeze = false
  Group = -> [Constraints,Elements,Parts]
  Verbose = false
  _LinkVersion = 1
  _SolverType = 1
  _Version = 1
FEATURE [App::FeaturePython] Constraints  # WARN: FeaturePython — macro-defined, semantics opaque (R4)
  Group = -> [Constraint,Constraint001,Constraint002]
  _LinkVersion = 1
  _Version = 1
FEATURE [App::FeaturePython] Elements  # WARN: FeaturePython — macro-defined, semantics opaque (R4)
  Group = -> [_Element,Element,Element001,_Element001,_Element002]
  _LinkVersion = 1
FEATURE [App::FeaturePython] Constraint  label="Locked"  # WARN: FeaturePython — macro-defined, semantics opaque (R4)
  Disabled = false
  Group = -> [ElementLink]
  _ConstraintType = 0
  _LinkVersion = 1
  _Parent = -> Constraints
FEATURE [App::FeaturePython] ElementLink  label="_Element"  # link proxy (typed FeaturePython)
  LinkTransform = true
  LinkedObject = -> _Element
  _LinkVersion = 1
  _Parent = -> Constraint
FEATURE [Part::FeaturePython] _Element  # link proxy (typed FeaturePython)
  Detach = false
  LinkTransform = true
  LinkedObject = -> Link [Pocket003.Face2]
  _LinkVersion = 1
  _Parent = -> Elements
FEATURE [Part::FeaturePython] Element  label="mate l"  # link proxy (typed FeaturePython)
  Detach = false
  LinkTransform = true
  LinkedObject = -> Link [Sketch005.Edge1]
  _LinkVersion = 1
  _Parent = -> Elements
FEATURE [Part::FeaturePython] Element001  label="mate r"  # link proxy (typed FeaturePython)
  Detach = false
  LinkTransform = true
  LinkedObject = -> Link [Sketch005.Edge2]
  _LinkVersion = 1
  _Parent = -> Elements
FEATURE [App::FeaturePython] Constraint001  label="Attachment"  # WARN: FeaturePython — macro-defined, semantics opaque (R4)
  Cascade = false
  Disabled = false
  Group = -> [ElementLink001,ElementLink002]
  Multiply = false
  _ConstraintType = 45
  _LinkVersion = 0
  _Parent = -> Constraints
FEATURE [App::FeaturePython] ElementLink001  label="_Element001"  # link proxy (typed FeaturePython)
  LinkTransform = true
  LinkedObject = -> _Element001
  Offset = pos=(0,0,-6.5) rot=(1,0,0;3.14159rad)
  Placement = pos=(-9e-16,-6.5,21) rot=(1,0,0;3.14159rad)
  _LinkVersion = 0
  _Parent = -> Constraint001
FEATURE [Part::FeaturePython] _Element001  # link proxy (typed FeaturePython)
  Detach = false
  LinkTransform = true
  LinkedObject = -> Link001 [0.Edge9]
  _LinkVersion = 0
  _Parent = -> Elements
FEATURE [App::FeaturePython] ElementLink002  label="mate r"  # link proxy (typed FeaturePython)
  LinkTransform = true
  LinkedObject = -> Element001
  _LinkVersion = 0
  _Parent = -> Constraint001
FEATURE [App::FeaturePython] Constraint002  label="Attachment001"  # WARN: FeaturePython — macro-defined, semantics opaque (R4)
  Cascade = false
  Disabled = false
  Group = -> [ElementLink003,ElementLink004]
  Multiply = false
  _ConstraintType = 45
  _LinkVersion = 0
  _Parent = -> Constraints
FEATURE [App::FeaturePython] ElementLink003  label="_Element002"  # link proxy (typed FeaturePython)
  LinkTransform = true
  LinkedObject = -> _Element002
  Offset = pos=(0,0,-6.5) rot=(1,0,0;3.14159rad)
  Placement = pos=(9e-16,-6.5,21) rot=(1,0,0;3.14159rad)
  _LinkVersion = 0
  _Parent = -> Constraint002
FEATURE [Part::FeaturePython] _Element002  # link proxy (typed FeaturePython)
  Detach = false
  LinkTransform = true
  LinkedObject = -> Link001 [1.Edge9]
  _LinkVersion = 0
  _Parent = -> Elements
FEATURE [App::FeaturePython] ElementLink004  label="mate l"  # link proxy (typed FeaturePython)
  LinkTransform = true
  LinkedObject = -> Element
  _LinkVersion = 0
  _Parent = -> Constraint002
---- part parts/NEMA23-76.FCStd = doc fcstd_c19784181319 ----
FCSTD DOCUMENT  (FreeCAD 2021.614R24301 +3747 (Git))
Label: NEMA23-76
License: Creative Commons Attribution
LicenseURL: http://creativecommons.org/licenses/by/4.0/
objects: App::FeaturePython×32, Part::FeaturePython×28, Sketcher::SketchObject×14, PartDesign::Pad×5, App::Link×5, PartDesign::Pocket×4, PartDesign::Hole×4, App::LinkElement×4, PartDesign::Body×2, PartDesign::Fillet×1, PartDesign::Line×1, PartDesign::SubtractiveHelix×1, PartDesign::Chamfer×1, App::DocumentObjectGroup×1
note: 91 computed .brp shape members not serialized (recipe doc carries the construction recipe); baked Part::Feature solids carry a one-line shape summary decoded from their .brp

FEATURE [Sketcher::SketchObject] Sketch
  FullyConstrained = true
  MapMode = 5
  Support = -> [XY_Plane]
  sketch-geometry (16):
    g0: LineSegment StartX=-23.55 StartY=28.2 StartZ=0 EndX=23.55 EndY=28.2 EndZ=0
    g1: LineSegment StartX=28.2 StartY=23.55 StartZ=0 EndX=28.2 EndY=-23.55 EndZ=0
    g2: LineSegment StartX=23.55 StartY=-28.2 StartZ=0 EndX=-23.55 EndY=-28.2 EndZ=0
    g3: LineSegment StartX=-28.2 StartY=-23.55 StartZ=0 EndX=-28.2 EndY=23.55 EndZ=0
    g4: ArcOfCircle CenterX=-23.55 CenterY=23.55 CenterZ=0 NormalX=0 NormalY=0 NormalZ=1 AngleXU=0 Radius=4.65 StartAngle=1.5708 EndAngle=3.14159
    g5: GeomPoint [constr] X=-28.2 Y=28.2 Z=0
    g6: ArcOfCircle CenterX=23.55 CenterY=23.55 CenterZ=0 NormalX=0 NormalY=0 NormalZ=1 AngleXU=0 Radius=4.65 StartAngle=0 EndAngle=1.5708
    g7: GeomPoint [constr] X=28.2 Y=28.2 Z=0
    g8: ArcOfCircle CenterX=23.55 CenterY=-23.55 CenterZ=0 NormalX=0 NormalY=0 NormalZ=1 AngleXU=0 Radius=4.65 StartAngle=4.71239 EndAngle=6.28319
    g9: GeomPoint [constr] X=28.2 Y=-28.2 Z=0
    g10: ArcOfCircle CenterX=-23.55 CenterY=-23.55 CenterZ=0 NormalX=0 NormalY=0 NormalZ=1 AngleXU=0 Radius=4.65 StartAngle=3.14159 EndAngle=4.71239
    g11: GeomPoint [constr] X=-28.2 Y=-28.2 Z=0
    g12: Circle CenterX=-23.55 CenterY=23.55 CenterZ=0 NormalX=0 NormalY=0 NormalZ=1 AngleXU=0 Radius=2.55
    g13: Circle CenterX=23.55 CenterY=23.55 CenterZ=0 NormalX=0 NormalY=0 NormalZ=1 AngleXU=0 Radius=2.55
    g14: Circle CenterX=23.55 CenterY=-23.55 CenterZ=0 NormalX=0 NormalY=0 NormalZ=1 AngleXU=0 Radius=2.55
    g15: Circle CenterX=-23.55 CenterY=-23.55 CenterZ=0 NormalX=0 NormalY=0 NormalZ=1 AngleXU=0 Radius=2.55
  constraints (35):
    c: Horizontal(g0)
    c: Horizontal(g2)
    c: Vertical(g1)
    c: Vertical(g3)
    c: Symmetric(g9,g5,g-1)
    c: PointOnObject(g5,g0)
    c: PointOnObject(g5,g3)
    c: Tangent(g0,g4) = 1.5708
    c: Tangent(g3,g4) = 1.5708
    c: PointOnObject(g7,g0)
    c: PointOnObject(g7,g1)
    c: Tangent(g0,g6) = 1.5708
    c: Tangent(g1,g6) = 1.5708
    c: PointOnObject(g9,g1)
    c: PointOnObject(g9,g2)
    c: Tangent(g1,g8) = 1.5708
    c: Tangent(g2,g8) = 1.5708
    c: PointOnObject(g11,g2)
    c: PointOnObject(g11,g3)
    c: Tangent(g2,g10) = 1.5708
    c: Tangent(g3,g10) = 1.5708
    c: Equal(g10,g8)
    c: Equal(g8,g6)
    c: Equal(g6,g4)
    c: Equal(g0,g1)
    c: DistanceX(g3,g1) = 56.4
    c: Coincident(g12,g4)
    c: Coincident(g13,g6)
    c: Coincident(g14,g8)
    c: Coincident(g15,g10)
    c: Equal(g15,g14)
    c: Equal(g14,g13)
    c: Equal(g13,g12)
    c: Diameter(g12) = 5.1
    c: DistanceX(g4,g6) = 47.1
FEATURE [PartDesign::Pad] Pad
  ClaimChildren = false
  Direction = (1,1,1)
  Fit = 0
  FitJoin = 0
  InnerFit = 0
  InnerFitJoin = 0
  InnerTaperAngle = 0
  InnerTaperAngleRev = 0
  Length = 6
  Length2 = 100
  Linearize = true
  NewSolid = false
  Profile = -> Sketch
  Refine = true
  Suppress = false
  Type = 0
FEATURE [Sketcher::SketchObject] Sketch001
  ExternalGeometry = -> [Pad]
  FullyConstrained = true
  MapMode = 5
  Placement = pos=(0,0,6) rot=(0,0,1;0rad)
  Support = -> [Pad]
  sketch-geometry (16):
    g0: LineSegment StartX=-18.55 StartY=28.2 StartZ=0 EndX=18.55 EndY=28.2 EndZ=0
    g1: LineSegment StartX=28.2 StartY=18.55 StartZ=0 EndX=28.2 EndY=-18.55 EndZ=0
    g2: LineSegment StartX=18.55 StartY=-28.2 StartZ=0 EndX=-18.55 EndY=-28.2 EndZ=0
    g3: LineSegment StartX=-28.2 StartY=-18.55 StartZ=0 EndX=-28.2 EndY=18.55 EndZ=0
    g4: ArcOfCircle CenterX=-23.55 CenterY=23.55 CenterZ=0 NormalX=0 NormalY=0 NormalZ=1 AngleXU=0 Radius=5 StartAngle=4.71239 EndAngle=6.28319
    g5: ArcOfCircle CenterX=23.55 CenterY=23.55 CenterZ=0 NormalX=0 NormalY=0 NormalZ=1 AngleXU=0 Radius=5 StartAngle=3.14159 EndAngle=4.71239
    g6: ArcOfCircle CenterX=23.55 CenterY=-23.55 CenterZ=0 NormalX=0 NormalY=0 NormalZ=1 AngleXU=0 Radius=5 StartAngle=1.5708 EndAngle=3.14159
    g7: ArcOfCircle CenterX=-23.55 CenterY=-23.55 CenterZ=0 NormalX=0 NormalY=0 NormalZ=1 AngleXU=0 Radius=5 StartAngle=1e-16 EndAngle=1.5708
    g8: LineSegment StartX=-18.55 StartY=28.2 StartZ=0 EndX=-18.55 EndY=23.55 EndZ=0
    g9: LineSegment StartX=-23.55 StartY=18.55 StartZ=0 EndX=-28.2 EndY=18.55 EndZ=0
    g10: LineSegment StartX=18.55 StartY=23.55 StartZ=0 EndX=18.55 EndY=28.2 EndZ=0
    g11: LineSegment StartX=23.55 StartY=18.55 StartZ=0 EndX=28.2 EndY=18.55 EndZ=0
    g12: LineSegment StartX=23.55 StartY=-18.55 StartZ=0 EndX=28.2 EndY=-18.55 EndZ=0
    g13: LineSegment StartX=18.55 StartY=-23.55 StartZ=0 EndX=18.55 EndY=-28.2 EndZ=0
    g14: LineSegment StartX=-18.55 StartY=-23.55 StartZ=0 EndX=-18.55 EndY=-28.2 EndZ=0
    g15: LineSegment StartX=-23.55 StartY=-18.55 StartZ=0 EndX=-28.2 EndY=-18.55 EndZ=0
  constraints (40):
    c: Horizontal(g0)
    c: Horizontal(g2)
    c: Vertical(g1)
    c: Vertical(g3)
    c: Coincident(g4,g-4)
    c: Vertical(g7,g4)
    c: Horizontal(g4,g5)
    c: Vertical(g5,g6)
    c: Horizontal(g7,g6)
    c: Symmetric(g6,g4,g-1)
    c: Equal(g5,g4)
    c: Equal(g4,g7)
    c: Equal(g7,g6)
    c: Diameter(g4) = 10
    c: Vertical(g10)
    c: Horizontal(g11)
    c: Horizontal(g12)
    c: Vertical(g14)
    c: Vertical(g8)
    c: Horizontal(g9)
    c: Coincident(g0,g8)
    c: Coincident(g3,g9)
    c: Coincident(g0,g10)
    c: Coincident(g1,g11)
    c: Coincident(g1,g12)
    c: Coincident(g2,g13)
    c: Tangent(g6,g13) = -1.5708
    c: Coincident(g3,g15)
    c: Tangent(g7,g14) = 1.5708
    c: Coincident(g2,g14)
    c: Tangent(g7,g15) = -1.5708
    c: Tangent(g6,g12) = 1.5708
    c: Tangent(g5,g10) = 1.5708
    c: Tangent(g5,g11) = -1.5708
    c: Tangent(g4,g8) = 1.5708
    c: Tangent(g4,g9) = 1.5708
    c: Horizontal(g0,g-4)
    c: Vertical(g3,g-4)
    c: Symmetric(g2,g0,g-1)
    c: Symmetric(g1,g3,g-2)
FEATURE [PartDesign::Pad] Pad001
  BaseFeature = -> Pad
  ClaimChildren = false
  Direction = (1,1,1)
  Fit = 0
  FitJoin = 0
  InnerFit = 0
  InnerFitJoin = 0
  InnerTaperAngle = 0
  InnerTaperAngleRev = 0
  Length = 70
  Length2 = 100
  Linearize = true
  NewSolid = false
  Profile = -> Sketch001
  Refine = true
  Suppress = false
  Type = 0
FEATURE [Sketcher::SketchObject] Sketch002
  FullyConstrained = true
  MapMode = 5
  Placement = pos=(0,0,0) rot=(1,0,0;3.14159rad)
  Support = -> [Pad001]
  sketch-geometry (1):
    g0: Circle CenterX=0 CenterY=0 CenterZ=0 NormalX=0 NormalY=0 NormalZ=1 AngleXU=0 Radius=19.05
  constraints (2):
    c: Coincident(g0,g-1)
    c: Diameter(g0) = 38.1
FEATURE [PartDesign::Pad] Pad002
  BaseFeature = -> Pad001
  ClaimChildren = false
  Direction = (1,1,1)
  Fit = 0
  FitJoin = 0
  InnerFit = 0
  InnerFitJoin = 0
  InnerTaperAngle = 0
  InnerTaperAngleRev = 0
  Length = 1.6
  Length2 = 100
  Linearize = true
  NewSolid = false
  Profile = -> Sketch002
  Refine = true
  Suppress = false
  Type = 0
FEATURE [Sketcher::SketchObject] Sketch003
  FullyConstrained = true
  MapMode = 5
  Placement = pos=(0,0,-1.6) rot=(1,0,0;3.14159rad)
  Support = -> [Pad002]
  sketch-geometry (1):
    g0: Circle CenterX=0 CenterY=0 CenterZ=0 NormalX=0 NormalY=0 NormalZ=1 AngleXU=0 Radius=3.175
  constraints (2):
    c: Coincident(g0,g-1)
    c: Diameter(g0) = 6.35
FEATURE [PartDesign::Pad] Pad003
  BaseFeature = -> Pad002
  ClaimChildren = false
  Direction = (1,1,1)
  Fit = 0
  FitJoin = 0
  InnerFit = 0
  InnerFitJoin = 0
  InnerTaperAngle = 0
  InnerTaperAngleRev = 0
  Length = 20
  Length2 = 100
  Linearize = true
  NewSolid = false
  Profile = -> Sketch003
  Refine = true
  Suppress = false
  Type = 0
FEATURE [PartDesign::Fillet] Fillet
  Base = -> Pad003 [Edge71,Edge8,Edge6,Edge16,Edge14,Edge68,Edge67,Edge72,Edge39,Edge40,Edge43,Edge44,Edge15,Edge47,Edge7,Edge36]
  BaseFeature = -> Pad003
  NewSolid = false
  Radius = 1.5
  Refine = true
  SupportTransform = false
  Suppress = false
FEATURE [App::Link] Link  label="Link(Nema23)"
  AutoLinkLabel = true
  LinkedObject = -> Body
  SyncGroupVisibility = false
  _LinkVersion = 1
FEATURE [PartDesign::Line] DatumLine
  AttacherType = Attacher::AttachEngineLine
  Length = 97.6
  MapMode = 19
  MinimumLength = 10
  Placement = pos=(0,0,-21.6) rot=(-1,0,0;3.14159rad)
  ResizeMode = 0
  Support = -> [Fillet]
FEATURE [PartDesign::Body] Body  label="Nema23"
  AutoGroupSolids = false
  ExportMode = 0
  Group = -> [Sketch,Pad,Sketch001,Pad001,Sketch002,Pad002,Sketch003,Pad003,Fillet,DatumLine]
  Origin = -> Origin
  Tip = -> Fillet
  _ExportChildren = -> [Pad,Pad001,Pad002,Pad003,Fillet,DatumLine]
  _GroupVersion = 1
FEATURE [Sketcher::SketchObject] Sketch004
  FullyConstrained = true
  MapMode = 5
  Support = -> [XY_Plane001]
  sketch-geometry (1):
    g0: Circle CenterX=0 CenterY=0 CenterZ=0 NormalX=0 NormalY=0 NormalZ=1 AngleXU=0 Radius=12.5
  constraints (2):
    c: Coincident(g0,g-1)
    c: Diameter(g0) = 25
FEATURE [PartDesign::Pad] Pad004
  ClaimChildren = false
  Direction = (1,1,1)
  Fit = 0
  FitJoin = 0
  InnerFit = 0
  InnerFitJoin = 0
  InnerTaperAngle = 0
  InnerTaperAngleRev = 0
  Length = 30
  Length2 = 100
  Linearize = true
  Midplane = true
  NewSolid = false
  Profile = -> Sketch004
  Refine = true
  Suppress = false
  Type = 0
FEATURE [Sketcher::SketchObject] Sketch005
  FullyConstrained = true
  MapMode = 5
  Placement = pos=(0,0,15) rot=(0,0,1;0rad)
  Support = -> [Pad004]
  sketch-geometry (1):
    g0: Circle CenterX=0 CenterY=0 CenterZ=0 NormalX=0 NormalY=0 NormalZ=1 AngleXU=0 Radius=3.175
  constraints (2):
    c: Coincident(g0,g-1)
    c: Diameter(g0) = 6.35
FEATURE [PartDesign::Pocket] Pocket
  BaseFeature = -> Pad004
  ClaimChildren = false
  Fit = 0
  FitJoin = 0
  InnerFit = 0
  InnerFitJoin = 0
  InnerTaperAngle = 0
  InnerTaperAngleRev = 0
  Length = 5
  Length2 = 100
  Linearize = true
  NewSolid = false
  Profile = -> Sketch005
  Refine = true
  Suppress = false
  Type = 1
FEATURE [Sketcher::SketchObject] Sketch006
  FullyConstrained = true
  MapMode = 5
  Placement = pos=(0,0,15) rot=(0,0,1;0rad)
  Support = -> [Pocket]
  sketch-geometry (1):
    g0: Circle CenterX=0 CenterY=0 CenterZ=0 NormalX=0 NormalY=0 NormalZ=1 AngleXU=0 Radius=5
  constraints (2):
    c: Coincident(g0,g-1)
    c: Diameter(g0) = 10
FEATURE [PartDesign::Pocket] Pocket001
  BaseFeature = -> Pocket
  ClaimChildren = false
  Fit = 0
  FitJoin = 0
  InnerFit = 0
  InnerFitJoin = 0
  InnerTaperAngle = 0
  InnerTaperAngleRev = 0
  Length = 21.5
  Length2 = 100
  Linearize = true
  NewSolid = false
  Profile = -> Sketch006
  Refine = true
  Suppress = false
  Type = 0
FEATURE [Sketcher::SketchObject] Sketch007
  FullyConstrained = true
  MapMode = 5
  Placement = pos=(0,0,15) rot=(0,0,1;0rad)
  Support = -> [Pocket001]
  sketch-geometry (4):
    g0: LineSegment StartX=-11.5 StartY=0.5 StartZ=0 EndX=13.5 EndY=0.5 EndZ=0
    g1: LineSegment StartX=13.5 StartY=0.5 StartZ=0 EndX=13.5 EndY=-0.5 EndZ=0
    g2: LineSegment StartX=13.5 StartY=-0.5 StartZ=0 EndX=-11.5 EndY=-0.5 EndZ=0
    g3: LineSegment StartX=-11.5 StartY=-0.5 StartZ=0 EndX=-11.5 EndY=0.5 EndZ=0
  constraints (11):
    c: Coincident(g0,g1)
    c: Coincident(g1,g2)
    c: Coincident(g2,g3)
    c: Coincident(g3,g0)
    c: Horizontal(g0)
    c: Horizontal(g2)
    c: DistanceY(g1,g1) = 1
    c: Symmetric(g1,g0,g-1)
    c: DistanceX(g2,g2) = 25
    c: Vertical(g3)
    c: DistanceX(g2,g-1) = 11.5
FEATURE [Sketcher::SketchObject] Sketch008
  FullyConstrained = true
  MapMode = 5
  Placement = pos=(0,0,0) rot=(1,0,0;1.5708rad)
  Support = -> [XZ_Plane001]
  sketch-geometry (2):
    g0: Circle CenterX=0 CenterY=10 CenterZ=0 NormalX=0 NormalY=0 NormalZ=1 AngleXU=0 Radius=1.75
    g1: Circle CenterX=0 CenterY=-10 CenterZ=0 NormalX=0 NormalY=0 NormalZ=1 AngleXU=0 Radius=1.75
  constraints (5):
    c: PointOnObject(g0,g-2)
    c: Equal(g1,g0)
    c: Symmetric(g0,g1,g-1)
    c: DistanceY(g1,g0) = 20
    c: Diameter(g0) = 3.5
FEATURE [PartDesign::Hole] Hole
  BaseFeature = -> Pocket001
  ClaimChildren = false
  CustomThreadClearance = 0
  Depth = 25
  DepthType = 1
  Diameter = 4.5
  DrillForDepth = false
  DrillPoint = 1
  DrillPointAngle = 118
  Fit = 0
  FitJoin = 0
  HoleCutCountersinkAngle = 90
  HoleCutCustomValues = false
  HoleCutDepth = 0
  HoleCutDiameter = 6.1
  HoleCutType = 0
  InnerFit = 0
  InnerFitJoin = 0
  ModelThread = false
  NewSolid = false
  Profile = -> Sketch008
  Refine = true
  Reversed = true
  Suppress = false
  Tapered = false
  TaperedAngle = 90
  ThreadClass = 0
  ThreadDepth = 93.5288
  ThreadDepthType = 0
  ThreadDirection = 0
  ThreadFit = 0
  ThreadSize = 0
  ThreadType = 0
  Threaded = false
  UseCustomThreadClearance = false
FEATURE [Sketcher::SketchObject] Sketch009
  FullyConstrained = true
  MapMode = 5
  Placement = pos=(0,0,0) rot=(1,0,0;1.5708rad)
  Support = -> [XZ_Plane001]
  sketch-geometry (2):
    g0: Circle CenterX=8 CenterY=10 CenterZ=0 NormalX=0 NormalY=0 NormalZ=1 AngleXU=0 Radius=1.25
    g1: Circle CenterX=8 CenterY=-10 CenterZ=0 NormalX=0 NormalY=0 NormalZ=1 AngleXU=0 Radius=1.25
  constraints (5):
    c: Symmetric(g0,g1,g-1)
    c: DistanceX(g-1,g0) = 8
    c: DistanceY(g1,g0) = 20
    c: Equal(g0,g1)
    c: Diameter(g0) = 2.5
FEATURE [Sketcher::SketchObject] Sketch010
  FullyConstrained = true
  MapMode = 5
  Placement = pos=(0,0,0) rot=(1,0,0;1.5708rad)
  Support = -> [XZ_Plane001]
  sketch-geometry (2):
    g0: Circle CenterX=8 CenterY=10 CenterZ=0 NormalX=0 NormalY=0 NormalZ=1 AngleXU=0 Radius=1.25
    g1: Circle CenterX=8 CenterY=-10 CenterZ=0 NormalX=0 NormalY=0 NormalZ=1 AngleXU=0 Radius=1.25
  constraints (5):
    c: Symmetric(g0,g1,g-1)
    c: DistanceX(g-1,g0) = 8
    c: DistanceY(g1,g0) = 20
    c: Equal(g0,g1)
    c: Diameter(g0) = 2.5
FEATURE [Sketcher::SketchObject] Sketch011
  AttachmentOffset = pos=(0,0,-4) rot=(0,0,1;0rad)
  FullyConstrained = true
  MapMode = 5
  Placement = pos=(0,4,9e-16) rot=(1,0,0;1.5708rad)
  Support = -> [XZ_Plane001]
  sketch-geometry (2):
    g0: Circle CenterX=8 CenterY=10 CenterZ=0 NormalX=0 NormalY=0 NormalZ=1 AngleXU=0 Radius=1.25
    g1: Circle CenterX=8 CenterY=-10 CenterZ=0 NormalX=0 NormalY=0 NormalZ=1 AngleXU=0 Radius=1.25
  constraints (5):
    c: Symmetric(g0,g1,g-1)
    c: DistanceX(g-1,g0) = 8
    c: DistanceY(g1,g0) = 20
    c: Equal(g0,g1)
    c: Diameter(g0) = 2.5
FEATURE [PartDesign::Hole] Hole001
  BaseFeature = -> Hole
  ClaimChildren = false
  CustomThreadClearance = 0
  Depth = 25
  DepthType = 1
  Diameter = 2.5
  DrillForDepth = false
  DrillPoint = 1
  DrillPointAngle = 118
  Fit = 0
  FitJoin = 0
  HoleCutCountersinkAngle = 90
  HoleCutCustomValues = false
  HoleCutDepth = 0
  HoleCutDiameter = 6.1
  HoleCutType = 0
  InnerFit = 0
  InnerFitJoin = 0
  ModelThread = false
  NewSolid = false
  Profile = -> Sketch009
  Refine = true
  Reversed = true
  Suppress = false
  Tapered = false
  TaperedAngle = 90
  ThreadClass = 0
  ThreadDepth = 93.5621
  ThreadDepthType = 0
  ThreadDirection = 0
  ThreadFit = 0
  ThreadSize = 0
  ThreadType = 0
  Threaded = false
  UseCustomThreadClearance = false
FEATURE [PartDesign::Hole] Hole002
  BaseFeature = -> Hole001
  ClaimChildren = false
  CustomThreadClearance = 0
  Depth = 25
  DepthType = 1
  Diameter = 3.1
  DrillForDepth = false
  DrillPoint = 1
  DrillPointAngle = 118
  Fit = 0
  FitJoin = 0
  HoleCutCountersinkAngle = 90
  HoleCutCustomValues = false
  HoleCutDepth = 0
  HoleCutDiameter = 6.1
  HoleCutType = 0
  InnerFit = 0
  InnerFitJoin = 0
  ModelThread = false
  NewSolid = false
  Profile = -> Sketch010
  Refine = true
  Suppress = false
  Tapered = false
  TaperedAngle = 90
  ThreadClass = 0
  ThreadDepth = 93.56
  ThreadDepthType = 0
  ThreadDirection = 0
  ThreadFit = 0
  ThreadSize = 0
  ThreadType = 0
  Threaded = false
  UseCustomThreadClearance = false
FEATURE [PartDesign::Hole] Hole003
  BaseFeature = -> Hole002
  ClaimChildren = false
  CustomThreadClearance = 0
  Depth = 25
  DepthType = 1
  Diameter = 6
  DrillForDepth = false
  DrillPoint = 1
  DrillPointAngle = 118
  Fit = 0
  FitJoin = 0
  HoleCutCountersinkAngle = 90
  HoleCutCustomValues = false
  HoleCutDepth = 0
  HoleCutDiameter = 6.1
  HoleCutType = 0
  InnerFit = 0
  InnerFitJoin = 0
  ModelThread = false
  NewSolid = false
  Profile = -> Sketch011
  Refine = true
  Suppress = false
  Tapered = false
  TaperedAngle = 90
  ThreadClass = 0
  ThreadDepth = 93.56
  ThreadDepthType = 0
  ThreadDirection = 0
  ThreadFit = 0
  ThreadSize = 0
  ThreadType = 0
  Threaded = false
  UseCustomThreadClearance = false
FEATURE [Sketcher::SketchObject] Sketch012
  AttachmentOffset = pos=(0,0,0) rot=(0,1,0;0.349066rad)
  ExternalGeometry = -> [Hole003]
  FullyConstrained = true
  MapMode = 5
  Placement = pos=(0,0,0) rot=(0.443713,0.633687,0.633687;2.30637rad)
  Support = -> [YZ_Plane001]
  sketch-geometry (4):
    g0: LineSegment StartX=4 StartY=-6.25 StartZ=0 EndX=14 EndY=-6.25 EndZ=0
    g1: LineSegment StartX=14 StartY=-6.25 StartZ=0 EndX=14 EndY=-6.75 EndZ=0
    g2: LineSegment StartX=14 StartY=-6.75 StartZ=0 EndX=4 EndY=-6.75 EndZ=0
    g3: LineSegment StartX=4 StartY=-6.75 StartZ=0 EndX=4 EndY=-6.25 EndZ=0
  constraints (12):
    c: Coincident(g0,g1)
    c: Coincident(g1,g2)
    c: Coincident(g2,g3)
    c: Coincident(g3,g0)
    c: Horizontal(g0)
    c: Horizontal(g2)
    c: Vertical(g1)
    c: Vertical(g3)
    c: DistanceY(g1,g1) = 0.5
    c: DistanceX(g2,g2) = 10
    c: DistanceX(g-1,g0) = 4
    c: DistanceY(g-3,g2) = 8.25
FEATURE [PartDesign::SubtractiveHelix] SubtractiveHelix
  Angle = 0
  Axis = (-2e-16,2e-16,1)
  Base = (0,0,0)
  BaseFeature = -> Hole003
  ClaimChildren = false
  Fit = 0
  FitJoin = 0
  HasBeenEdited = true
  Height = 13
  InnerFit = 0
  InnerFitJoin = 0
  LeftHanded = false
  Mode = 0
  NewSolid = false
  Outside = false
  Pitch = 3
  Profile = -> Sketch012
  ReferenceAxis = -> Sketch012 [V_Axis]
  Refine = true
  Suppress = false
  Turns = 3
FEATURE [PartDesign::Pocket] Pocket002
  BaseFeature = -> SubtractiveHelix
  ClaimChildren = false
  Fit = 0
  FitJoin = 0
  InnerFit = 0
  InnerFitJoin = 0
  InnerTaperAngle = 0
  InnerTaperAngleRev = 0
  Length = 10.5
  Length2 = 100
  Linearize = true
  NewSolid = false
  Profile = -> Sketch007
  Refine = true
  Suppress = false
  Type = 0
FEATURE [Sketcher::SketchObject] Sketch013
  FullyConstrained = true
  MapMode = 5
  Placement = pos=(0,0,-15) rot=(1,0,0;3.14159rad)
  Support = -> [Pocket002]
  sketch-geometry (4):
    g0: LineSegment StartX=-11.5 StartY=0.5 StartZ=0 EndX=13.5 EndY=0.5 EndZ=0
    g1: LineSegment StartX=13.5 StartY=0.5 StartZ=0 EndX=13.5 EndY=-0.5 EndZ=0
    g2: LineSegment StartX=13.5 StartY=-0.5 StartZ=0 EndX=-11.5 EndY=-0.5 EndZ=0
    g3: LineSegment StartX=-11.5 StartY=-0.5 StartZ=0 EndX=-11.5 EndY=0.5 EndZ=0
  constraints (11):
    c: Coincident(g0,g1)
    c: Coincident(g1,g2)
    c: Coincident(g2,g3)
    c: Coincident(g3,g0)
    c: Horizontal(g0)
    c: Horizontal(g2)
    c: Vertical(g3)
    c: DistanceY(g1,g1) = 1
    c: Symmetric(g1,g0,g-1)
    c: DistanceX(g2,g2) = 25
    c: DistanceX(g2,g-1) = 11.5
FEATURE [PartDesign::Pocket] Pocket003
  BaseFeature = -> Pocket002
  ClaimChildren = false
  Fit = 0
  FitJoin = 0
  InnerFit = 0
  InnerFitJoin = 0
  InnerTaperAngle = 0
  InnerTaperAngleRev = 0
  Length = 10
  Length2 = 100
  Linearize = true
  NewSolid = false
  Profile = -> Sketch013
  Refine = true
  Suppress = false
  Type = 0
FEATURE [App::Link] Link001  label="Link001(Coupling)"
  AutoLinkLabel = true
  LinkedObject = -> Body001
  SyncGroupVisibility = false
  _LinkVersion = 1
FEATURE [Part::FeaturePython] Screw  label="M3x12-Screw"  # Fasteners workbench fastener (typed FeaturePython)
  Placement = pos=(8,4,-10) rot=(0,0.707107,0.707107;3.14159rad)
  diameter = 4
  invert = false
  length = 4
  lengthCustom = 12
  matchOuter = false
  offset = 0
  thread = false
  type = 33
FEATURE [Part::FeaturePython] Screw001  label="M4x8-Screw"  # Fasteners workbench fastener (typed FeaturePython)
  Placement = pos=(0,-10.23,-10) rot=(1,0,0;1.5708rad)
  diameter = 7
  invert = false
  length = 3
  lengthCustom = 8
  matchOuter = false
  offset = 0
  thread = false
  type = 29
FEATURE [App::Link] Link002  label="Link002(M4x8-Screw)"
  AutoLinkLabel = true
  LinkPlacement = pos=(0,-12.23,10) rot=(1,0,0;1.5708rad)
  LinkedObject = -> Screw001
  Placement = pos=(0,-12.23,10) rot=(1,0,0;1.5708rad)
  SyncGroupVisibility = false
  _LinkVersion = 1
FEATURE [App::Link] Link003  label="Link003(M3x12-Screw)"
  AutoLinkLabel = true
  LinkPlacement = pos=(8,4,10) rot=(0,0.707107,0.707107;3.14159rad)
  LinkedObject = -> Screw
  Placement = pos=(8,4,10) rot=(0,0.707107,0.707107;3.14159rad)
  SyncGroupVisibility = false
  _LinkVersion = 1
FEATURE [Part::FeaturePython] Parts001  # WARN: FeaturePython — macro-defined, semantics opaque (R4)
  Group = -> [Link001,Screw,Screw001,Link002,Link003]
  GroupMode = 0
  _LinkVersion = 1
FEATURE [PartDesign::Chamfer] Chamfer
  Angle = 45
  Base = -> Pocket003 [Edge115,Edge1,Edge17,Edge21,Edge138,Edge143]
  BaseFeature = -> Pocket003
  ChamferType = 0
  FlipDirection = false
  NewSolid = false
  Refine = true
  Size = 0.5
  Size2 = 1
  SupportTransform = false
  Suppress = false
FEATURE [PartDesign::Body] Body001  label="Coupling"
  AutoGroupSolids = false
  ExportMode = 0
  Group = -> [Sketch004,Pad004,Sketch005,Pocket,Sketch006,Pocket001,Sketch007,Sketch008,Hole,Sketch009,Sketch010,Sketch011,Hole001,Hole002,Hole003,Sketch012,SubtractiveHelix,Pocket002,Sketch013,Pocket003,Chamfer]
  Origin = -> Origin001
  Placement = pos=(0,0,-51) rot=(0,0,1;0rad)
  Tip = -> Chamfer
  _ExportChildren = -> [Pad004,Pocket,Pocket001,Hole,Hole001,Hole002,Hole003,SubtractiveHelix,Pocket002,Pocket003,Chamfer]
  _GroupVersion = 1
FEATURE [Part::FeaturePython] Screw002  label="M5x16-Screw"  # Fasteners workbench fastener (typed FeaturePython)
  diameter = 6
  invert = false
  length = 4
  lengthCustom = 16
  matchOuter = false
  offset = 0
  thread = false
  type = 33
FEATURE [App::DocumentObjectGroup] Group  label="Components"
  ExportMode = 1
  Group = -> [Body001,Body,Screw002]
  _GroupVersion = 1
FEATURE [App::LinkElement] Link004_i0
  LinkPlacement = pos=(23.55,67.55,6) rot=(0,0,1;0rad)
  LinkedObject = -> Screw002
  Placement = pos=(23.55,67.55,6) rot=(0,0,1;0rad)
  _LinkVersion = 1
FEATURE [App::LinkElement] Link004_i1
  LinkPlacement = pos=(-23.55,67.55,6) rot=(0,0,1;0rad)
  LinkedObject = -> Screw002
  Placement = pos=(-23.55,67.55,6) rot=(0,0,1;0rad)
  _LinkVersion = 1
FEATURE [App::LinkElement] Link004_i2
  LinkPlacement = pos=(-23.55,20.45,6) rot=(0,0,1;0rad)
  LinkedObject = -> Screw002
  Placement = pos=(-23.55,20.45,6) rot=(0,0,1;0rad)
  _LinkVersion = 1
FEATURE [App::LinkElement] Link004_i3
  LinkPlacement = pos=(23.55,20.45,6) rot=(0,0,1;0rad)
  LinkedObject = -> Screw002
  Placement = pos=(23.55,20.45,6) rot=(0,0,1;0rad)
  _LinkVersion = 1
FEATURE [App::Link] Link004  label="M5x16-Screw 4ct"
  AutoLinkLabel = true
  ElementCount = 4
  ElementList = -> [Link004_i0,Link004_i1,Link004_i2,Link004_i3]
  LinkPlacement = pos=(0,-44,0) rot=(0,0,1;0rad)
  LinkedObject = -> Screw002
  Placement = pos=(0,-44,0) rot=(0,0,1;0rad)
  SyncGroupVisibility = false
  _LinkVersion = 1
FEATURE [Part::FeaturePython] Parts  # WARN: FeaturePython — macro-defined, semantics opaque (R4)
  Group = -> [Link,Link004]
  GroupMode = 0
  _LinkVersion = 1
FEATURE [Part::FeaturePython] Assembly  label="NEMA23-76-Assembly"  # WARN: FeaturePython — macro-defined, semantics opaque (R4)
  AutoRelax = true
  BuildShape = 0
  Freeze = false
  Group = -> [Constraints,Elements,Parts]
  Verbose = false
  _LinkVersion = 1
  _SolverType = 1
  _Version = 1
FEATURE [App::FeaturePython] Constraints  # WARN: FeaturePython — macro-defined, semantics opaque (R4)
  Group = -> [Constraint004,Constraint006,Constraint007,Constraint008,Constraint009]
  _LinkVersion = 1
  _Version = 1
FEATURE [App::FeaturePython] Elements  # WARN: FeaturePython — macro-defined, semantics opaque (R4)
  Group = -> [Element,Element001,Element002,Element003,Element004,Element005,Element010,_Element006,_Element007,_Element008,_Element009]
  _LinkVersion = 1
FEATURE [Part::FeaturePython] Element  # link proxy (typed FeaturePython)
  Detach = false
  LinkTransform = true
  LinkedObject = -> Link [Fillet.Edge19]
  _LinkVersion = 1
  _Parent = -> Elements
FEATURE [Part::FeaturePython] Element001  # link proxy (typed FeaturePython)
  Detach = false
  LinkTransform = true
  LinkedObject = -> Link [Fillet.Edge49]
  _LinkVersion = 1
  _Parent = -> Elements
FEATURE [Part::FeaturePython] Element002  # link proxy (typed FeaturePython)
  Detach = false
  LinkTransform = true
  LinkedObject = -> Link [Fillet.Edge101]
  _LinkVersion = 1
  _Parent = -> Elements
FEATURE [Part::FeaturePython] Element003  # link proxy (typed FeaturePython)
  Detach = false
  LinkTransform = true
  LinkedObject = -> Link [Fillet.Edge103]
  _LinkVersion = 1
  _Parent = -> Elements
FEATURE [Part::FeaturePython] Element004  label="bracket-mate"  # link proxy (typed FeaturePython)
  Detach = false
  LinkTransform = true
  LinkedObject = -> Link [Fillet.Edge36]
  _LinkVersion = 1
  _Parent = -> Elements
FEATURE [Part::FeaturePython] Element005  label="Axis"  # link proxy (typed FeaturePython)
  Detach = false
  LinkTransform = true
  LinkedObject = -> Link [DatumLine.]
  _LinkVersion = 1
  _Parent = -> Elements
FEATURE [Part::FeaturePython] Assembly001  label="Coupling-Assembly"  # WARN: FeaturePython — macro-defined, semantics opaque (R4)
  AutoRelax = true
  BuildShape = 0
  Freeze = false
  Group = -> [Constraints001,Elements001,Parts001]
  Placement = pos=(0,5.84137e-06,-49) rot=(0,0,1;0rad)
  Verbose = false
  _LinkVersion = 1
  _SolverType = 1
  _Version = 1
FEATURE [App::FeaturePython] Constraints001  # WARN: FeaturePython — macro-defined, semantics opaque (R4)
  Group = -> [Constraint,Constraint001,Constraint002,Constraint003,Constraint005]
  _LinkVersion = 1
  _Version = 1
FEATURE [App::FeaturePython] Elements001  # WARN: FeaturePython — macro-defined, semantics opaque (R4)
  Group = -> [Element006,Element007,_Element,_Element001,_Element002,_Element003,_Element004,_Element005,Element008,Element009]
  _LinkVersion = 1
FEATURE [Part::FeaturePython] Element006  # link proxy (typed FeaturePython)
  Detach = false
  LinkTransform = true
  LinkedObject = -> Link001 [Hole.Sketch008.Edge2]
  Offset = pos=(0,0,3) rot=(0,0,1;0rad)
  Placement = pos=(0,-3,0) rot=(0,0,1;0rad)
  _LinkVersion = 1
  _Parent = -> Elements001
FEATURE [Part::FeaturePython] Element007  # link proxy (typed FeaturePython)
  Detach = false
  LinkTransform = true
  LinkedObject = -> Link001 [Hole.Sketch008.Edge1]
  Offset = pos=(0,0,5) rot=(0,0,1;0rad)
  Placement = pos=(0,-5,1.8e-15) rot=(0,0,1;0rad)
  _LinkVersion = 1
  _Parent = -> Elements001
FEATURE [App::FeaturePython] Constraint  label="Attachment"  # WARN: FeaturePython — macro-defined, semantics opaque (R4)
  Cascade = false
  Disabled = false
  Group = -> [ElementLink,ElementLink001]
  Multiply = false
  _ConstraintType = 45
  _LinkVersion = 1
  _Parent = -> Constraints001
FEATURE [App::FeaturePython] ElementLink  label="_Element"  # link proxy (typed FeaturePython)
  LinkTransform = true
  LinkedObject = -> _Element
  _LinkVersion = 1
  _Parent = -> Constraint
FEATURE [Part::FeaturePython] _Element  # link proxy (typed FeaturePython)
  Detach = false
  LinkTransform = true
  LinkedObject = -> Link001 [Pocket003.Edge106]
  _LinkVersion = 1
  _Parent = -> Elements001
FEATURE [App::FeaturePython] ElementLink001  label="_Element001"  # link proxy (typed FeaturePython)
  LinkTransform = true
  LinkedObject = -> _Element001
  _LinkVersion = 1
  _Parent = -> Constraint
FEATURE [Part::FeaturePython] _Element001  # link proxy (typed FeaturePython)
  Detach = false
  LinkTransform = true
  LinkedObject = -> Screw [Edge9]
  _LinkVersion = 1
  _Parent = -> Elements001
FEATURE [App::FeaturePython] Constraint001  label="Attachment001"  # WARN: FeaturePython — macro-defined, semantics opaque (R4)
  Cascade = false
  Disabled = false
  Group = -> [ElementLink002,ElementLink003]
  Multiply = false
  _ConstraintType = 45
  _LinkVersion = 1
  _Parent = -> Constraints001
FEATURE [App::FeaturePython] ElementLink002  label="_Element002"  # link proxy (typed FeaturePython)
  LinkTransform = true
  LinkedObject = -> _Element002
  _LinkVersion = 1
  _Parent = -> Constraint001
FEATURE [Part::FeaturePython] _Element002  # link proxy (typed FeaturePython)
  Detach = false
  LinkTransform = true
  LinkedObject = -> Link001 [Pocket003.Edge174]
  _LinkVersion = 1
  _Parent = -> Elements001
FEATURE [App::FeaturePython] ElementLink003  label="_Element003"  # link proxy (typed FeaturePython)
  LinkTransform = true
  LinkedObject = -> _Element003
  _LinkVersion = 1
  _Parent = -> Constraint001
FEATURE [Part::FeaturePython] _Element003  # link proxy (typed FeaturePython)
  Detach = false
  LinkTransform = true
  LinkedObject = -> Link003 [Edge9]
  _LinkVersion = 1
  _Parent = -> Elements001
FEATURE [App::FeaturePython] Constraint002  label="Attachment002"  # WARN: FeaturePython — macro-defined, semantics opaque (R4)
  Cascade = false
  Disabled = false
  Group = -> [ElementLink004,ElementLink005]
  Multiply = false
  _ConstraintType = 45
  _LinkVersion = 1
  _Parent = -> Constraints001
FEATURE [App::FeaturePython] ElementLink004  label="Element006"  # link proxy (typed FeaturePython)
  LinkTransform = true
  LinkedObject = -> Element006
  _LinkVersion = 1
  _Parent = -> Constraint002
FEATURE [App::FeaturePython] ElementLink005  label="_Element004"  # link proxy (typed FeaturePython)
  LinkTransform = true
  LinkedObject = -> _Element004
  _LinkVersion = 1
  _Parent = -> Constraint002
FEATURE [Part::FeaturePython] _Element004  # link proxy (typed FeaturePython)
  Detach = false
  LinkTransform = true
  LinkedObject = -> Screw001 [Edge10]
  _LinkVersion = 1
  _Parent = -> Elements001
FEATURE [App::FeaturePython] Constraint003  label="Attachment003"  # WARN: FeaturePython — macro-defined, semantics opaque (R4)
  Cascade = false
  Disabled = false
  Group = -> [ElementLink006,ElementLink007]
  Multiply = false
  _ConstraintType = 45
  _LinkVersion = 1
  _Parent = -> Constraints001
FEATURE [App::FeaturePython] ElementLink006  label="Element007"  # link proxy (typed FeaturePython)
  LinkTransform = true
  LinkedObject = -> Element007
  _LinkVersion = 1
  _Parent = -> Constraint003
FEATURE [App::FeaturePython] ElementLink007  label="_Element005"  # link proxy (typed FeaturePython)
  LinkTransform = true
  LinkedObject = -> _Element005
  _LinkVersion = 1
  _Parent = -> Constraint003
FEATURE [Part::FeaturePython] _Element005  # link proxy (typed FeaturePython)
  Detach = false
  LinkTransform = true
  LinkedObject = -> Link002 [Edge10]
  _LinkVersion = 1
  _Parent = -> Elements001
FEATURE [Part::FeaturePython] Element008  label="motor-mate"  # link proxy (typed FeaturePython)
  Detach = false
  LinkTransform = true
  LinkedObject = -> Link001 [Pocket.Sketch005.]
  Offset = pos=(0,0,-21) rot=(0,0,1;0rad)
  Placement = pos=(0,0,-21) rot=(0,0,1;0rad)
  _LinkVersion = 1
  _Parent = -> Elements001
FEATURE [Part::FeaturePython] Element009  label="screw-mate"  # link proxy (typed FeaturePython)
  Detach = false
  LinkTransform = true
  LinkedObject = -> Link001 [Pocket.Sketch005.]
  Offset = pos=(0,0,-10) rot=(0,0,1;0rad)
  Placement = pos=(0,0,-10) rot=(0,0,1;0rad)
  _LinkVersion = 1
  _Parent = -> Elements001
FEATURE [Part::FeaturePython] Element010  label="coupling-mate"  # link proxy (typed FeaturePython)
  Detach = false
  LinkTransform = true
  LinkedObject = -> Link [Fillet.Edge170]
  _LinkVersion = 1
  _Parent = -> Elements
FEATURE [App::FeaturePython] Constraint004  label="Locked"  # WARN: FeaturePython — macro-defined, semantics opaque (R4)
  Disabled = false
  Group = -> [ElementLink008]
  _ConstraintType = 0
  _LinkVersion = 1
  _Parent = -> Constraints
FEATURE [App::FeaturePython] ElementLink008  label="coupling-mate"  # link proxy (typed FeaturePython)
  LinkTransform = true
  LinkedObject = -> Element010
  _LinkVersion = 1
  _Parent = -> Constraint004
FEATURE [App::FeaturePython] Constraint005  label="Locked001"  # WARN: FeaturePython — macro-defined, semantics opaque (R4)
  Disabled = false
  Group = -> [ElementLink009]
  _ConstraintType = 0
  _LinkVersion = 1
  _Parent = -> Constraints001
FEATURE [App::FeaturePython] ElementLink009  label="motor-mate"  # link proxy (typed FeaturePython)
  LinkTransform = true
  LinkedObject = -> Element008
  _LinkVersion = 1
  _Parent = -> Constraint005
FEATURE [App::FeaturePython] Constraint006  label="Attachment004"  # WARN: FeaturePython — macro-defined, semantics opaque (R4)
  Cascade = false
  Disabled = false
  Group = -> [ElementLink010,ElementLink011]
  Multiply = false
  _ConstraintType = 45
  _LinkVersion = 1
  _Parent = -> Constraints
FEATURE [App::FeaturePython] ElementLink010  label="_Element006"  # link proxy (typed FeaturePython)
  LinkTransform = true
  LinkedObject = -> _Element006
  _LinkVersion = 1
  _Parent = -> Constraint006
FEATURE [Part::FeaturePython] _Element006  # link proxy (typed FeaturePython)
  Detach = false
  LinkTransform = true
  LinkedObject = -> Link004 [0.Edge9]
  _LinkVersion = 1
  _Parent = -> Elements
FEATURE [App::FeaturePython] ElementLink011  label="Element"  # link proxy (typed FeaturePython)
  LinkTransform = true
  LinkedObject = -> Element
  _LinkVersion = 1
  _Parent = -> Constraint006
FEATURE [App::FeaturePython] Constraint007  label="Attachment005"  # WARN: FeaturePython — macro-defined, semantics opaque (R4)
  Cascade = false
  Disabled = false
  Group = -> [ElementLink012,ElementLink013]
  Multiply = false
  _ConstraintType = 45
  _LinkVersion = 1
  _Parent = -> Constraints
FEATURE [App::FeaturePython] ElementLink012  label="_Element007"  # link proxy (typed FeaturePython)
  LinkTransform = true
  LinkedObject = -> _Element007
  _LinkVersion = 1
  _Parent = -> Constraint007
FEATURE [Part::FeaturePython] _Element007  # link proxy (typed FeaturePython)
  Detach = false
  LinkTransform = true
  LinkedObject = -> Link004 [1.Edge9]
  _LinkVersion = 1
  _Parent = -> Elements
FEATURE [App::FeaturePython] ElementLink013  label="Element001"  # link proxy (typed FeaturePython)
  LinkTransform = true
  LinkedObject = -> Element001
  _LinkVersion = 1
  _Parent = -> Constraint007
FEATURE [App::FeaturePython] Constraint008  label="Attachment006"  # WARN: FeaturePython — macro-defined, semantics opaque (R4)
  Cascade = false
  Disabled = false
  Group = -> [ElementLink014,ElementLink015]
  Multiply = false
  _ConstraintType = 45
  _LinkVersion = 1
  _Parent = -> Constraints
FEATURE [App::FeaturePython] ElementLink014  label="_Element008"  # link proxy (typed FeaturePython)
  LinkTransform = true
  LinkedObject = -> _Element008
  _LinkVersion = 1
  _Parent = -> Constraint008
FEATURE [Part::FeaturePython] _Element008  # link proxy (typed FeaturePython)
  Detach = false
  LinkTransform = true
  LinkedObject = -> Link004 [2.Edge9]
  _LinkVersion = 1
  _Parent = -> Elements
FEATURE [App::FeaturePython] ElementLink015  label="Element002"  # link proxy (typed FeaturePython)
  LinkTransform = true
  LinkedObject = -> Element002
  _LinkVersion = 1
  _Parent = -> Constraint008
FEATURE [App::FeaturePython] Constraint009  label="Attachment007"  # WARN: FeaturePython — macro-defined, semantics opaque (R4)
  Cascade = false
  Disabled = false
  Group = -> [ElementLink016,ElementLink017]
  Multiply = false
  _ConstraintType = 45
  _LinkVersion = 1
  _Parent = -> Constraints
FEATURE [App::FeaturePython] ElementLink016  label="_Element009"  # link proxy (typed FeaturePython)
  LinkTransform = true
  LinkedObject = -> _Element009
  _LinkVersion = 1
  _Parent = -> Constraint009
FEATURE [Part::FeaturePython] _Element009  # link proxy (typed FeaturePython)
  Detach = false
  LinkTransform = true
  LinkedObject = -> Link004 [3.Edge9]
  _LinkVersion = 1
  _Parent = -> Elements
FEATURE [App::FeaturePython] ElementLink017  label="Element003"  # link proxy (typed FeaturePython)
  LinkTransform = true
  LinkedObject = -> Element003
  _LinkVersion = 1
  _Parent = -> Constraint009
